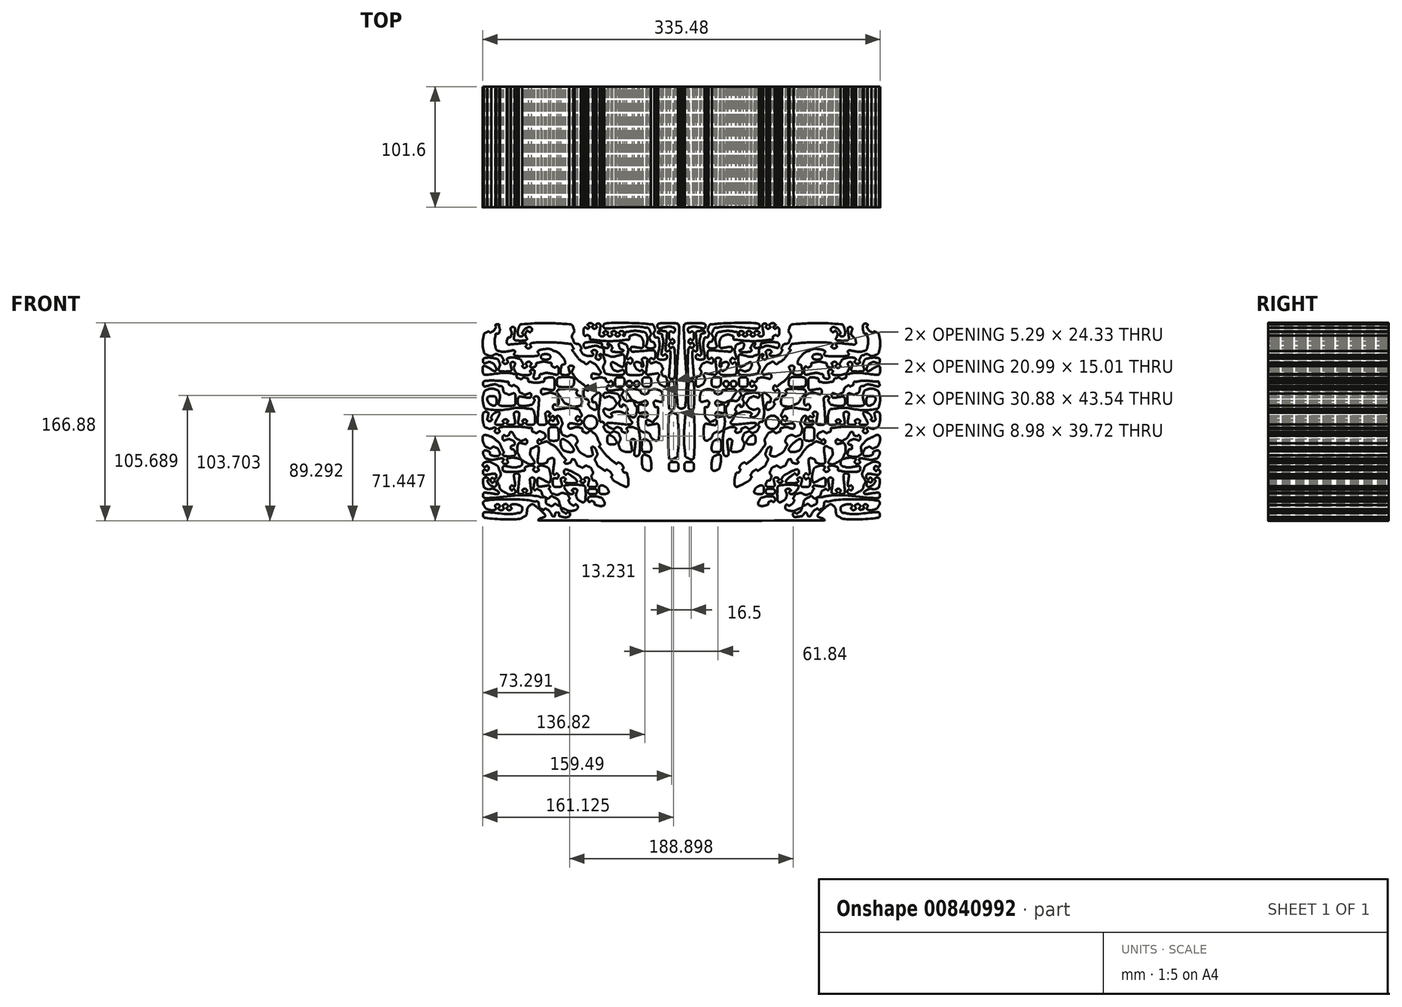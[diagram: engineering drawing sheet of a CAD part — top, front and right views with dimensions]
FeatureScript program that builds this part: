
annotation { "Feature Type Name" : "Feature", "Feature Type Description" : "" }
export const myFeature = defineFeature(function(context is Context, id is Id, definition is map)
    precondition{}
    {
        {
            var Q0;
            Q0=qCreatedBy(makeId("Front.planeOp"),FACE);
            var sketch = newSketch(context, id + "F0", { "sketchPlane" : qUnion([Q0])});
            skCircle(sketch, "E0", {"center": v(-76.75, -0.34) * mm, "radius": 5.68 * mm});
            skCircle(sketch, "E1", {"center": v(76.75, -0.34) * mm, "radius": 5.68 * mm});
            skLineSegment(sketch, "E2", {"start": v(-153.75, 82.4) * mm, "end": v(-156.25, 82.4) * mm});
            skFitSpline(sketch, "E3", {"points": [v(-156.25, 82.4) * mm, v(-156.45, 82.3) * mm, v(-156.71, 82.14) * mm, v(-156.75, 81.9) * mm]});
            skFitSpline(sketch, "E4", {"points": [v(-156.75, 81.9) * mm, v(-156.89, 81.09) * mm, v(-156.33, 80.13) * mm, v(-156.75, 79.4) * mm]});
            skFitSpline(sketch, "E5", {"points": [v(-156.75, 79.4) * mm, v(-157.58, 77.98) * mm, v(-158.77, 76.65) * mm, v(-160.25, 75.9) * mm]});
            skFitSpline(sketch, "E6", {"points": [v(-160.25, 75.9) * mm, v(-161.3, 75.39) * mm, v(-162.7, 76.4) * mm, v(-163.75, 75.9) * mm]});
            skFitSpline(sketch, "E7", {"points": [v(-163.75, 75.9) * mm, v(-165.03, 75.32) * mm, v(-166.49, 74.3) * mm, v(-166.75, 72.9) * mm]});
            skFitSpline(sketch, "E8", {"points": [v(-166.75, 72.9) * mm, v(-167.55, 68.65) * mm, v(-167.65, 64.15) * mm, v(-166.75, 59.9) * mm]});
            skFitSpline(sketch, "E9", {"points": [v(-166.75, 59.9) * mm, v(-166.4, 58.3) * mm, v(-164.84, 56.84) * mm, v(-163.25, 56.4) * mm]});
            skFitSpline(sketch, "E10", {"points": [v(-163.25, 56.4) * mm, v(-160.2, 55.59) * mm, v(-156.8, 57.23) * mm, v(-153.75, 56.4) * mm]});
            skFitSpline(sketch, "E11", {"points": [v(-153.75, 56.4) * mm, v(-152.16, 55.98) * mm, v(-151.03, 54.36) * mm, v(-150.25, 52.9) * mm]});
            skFitSpline(sketch, "E12", {"points": [v(-150.25, 52.9) * mm, v(-149.78, 52.03) * mm, v(-151, 50.56) * mm, v(-150.25, 49.9) * mm]});
            skFitSpline(sketch, "E13", {"points": [v(-150.25, 49.9) * mm, v(-149.36, 49.15) * mm, v(-147.26, 49.4) * mm, v(-146.75, 49.9) * mm]});
            skFitSpline(sketch, "E14", {"points": [v(-146.75, 49.9) * mm, v(-146.24, 50.42) * mm, v(-147.26, 52.9) * mm, v(-146.75, 53.4) * mm]});
            skFitSpline(sketch, "E15", {"points": [v(-146.75, 53.4) * mm, v(-146.24, 53.92) * mm, v(-140.62, 54.3) * mm, v(-137.75, 53.4) * mm]});
            skFitSpline(sketch, "E16", {"points": [v(-137.75, 53.4) * mm, v(-135.95, 52.85) * mm, v(-134.69, 51.05) * mm, v(-133.75, 49.4) * mm]});
            skFitSpline(sketch, "E17", {"points": [v(-133.75, 49.4) * mm, v(-133.25, 48.54) * mm, v(-134.46, 47.12) * mm, v(-133.75, 46.4) * mm]});
            skFitSpline(sketch, "E18", {"points": [v(-133.75, 46.4) * mm, v(-133.04, 45.7) * mm, v(-131.26, 45.9) * mm, v(-130.75, 46.4) * mm]});
            skFitSpline(sketch, "E19", {"points": [v(-130.75, 46.4) * mm, v(-130.24, 46.92) * mm, v(-131.26, 49.4) * mm, v(-130.75, 49.9) * mm]});
            skFitSpline(sketch, "E20", {"points": [v(-130.75, 49.9) * mm, v(-130.24, 50.42) * mm, v(-128.07, 50.73) * mm, v(-127.25, 49.9) * mm]});
            skFitSpline(sketch, "E21", {"points": [v(-127.25, 49.9) * mm, v(-126.42, 49.08) * mm, v(-127.76, 46.92) * mm, v(-127.25, 46.4) * mm]});
            skFitSpline(sketch, "E22", {"points": [v(-127.25, 46.4) * mm, v(-126.74, 45.9) * mm, v(-125.13, 45.93) * mm, v(-124.25, 46.4) * mm]});
            skFitSpline(sketch, "E23", {"points": [v(-124.25, 46.4) * mm, v(-122.8, 47.2) * mm, v(-122.34, 49.48) * mm, v(-120.75, 49.9) * mm]});
            skFitSpline(sketch, "E24", {"points": [v(-120.75, 49.9) * mm, v(-117.7, 50.73) * mm, v(-114.3, 50.73) * mm, v(-111.25, 49.9) * mm]});
            skFitSpline(sketch, "E25", {"points": [v(-111.25, 49.9) * mm, v(-109.66, 49.48) * mm, v(-109.23, 47.15) * mm, v(-107.75, 46.4) * mm]});
            skFitSpline(sketch, "E26", {"points": [v(-107.75, 46.4) * mm, v(-106.7, 45.89) * mm, v(-104.76, 46.92) * mm, v(-104.25, 46.4) * mm]});
            skFitSpline(sketch, "E27", {"points": [v(-104.25, 46.4) * mm, v(-103.74, 45.9) * mm, v(-103.74, 40.92) * mm, v(-104.25, 40.4) * mm]});
            skFitSpline(sketch, "E28", {"points": [v(-104.25, 40.4) * mm, v(-104.76, 39.9) * mm, v(-113.34, 41.32) * mm, v(-117.75, 40.4) * mm]});
            skFitSpline(sketch, "E29", {"points": [v(-117.75, 40.4) * mm, v(-119.37, 40.08) * mm, v(-119.8, 37.7) * mm, v(-121.25, 36.9) * mm]});
            skFitSpline(sketch, "E30", {"points": [v(-121.25, 36.9) * mm, v(-122.13, 36.43) * mm, v(-123.74, 36.4) * mm, v(-124.25, 36.9) * mm]});
            skFitSpline(sketch, "E31", {"points": [v(-124.25, 36.9) * mm, v(-124.76, 37.42) * mm, v(-123.74, 42.9) * mm, v(-124.25, 43.4) * mm]});
            skFitSpline(sketch, "E32", {"points": [v(-124.25, 43.4) * mm, v(-124.76, 43.92) * mm, v(-126.74, 43.92) * mm, v(-127.25, 43.4) * mm]});
            skFitSpline(sketch, "E33", {"points": [v(-127.25, 43.4) * mm, v(-127.76, 42.9) * mm, v(-126.74, 40.92) * mm, v(-127.25, 40.4) * mm]});
            skFitSpline(sketch, "E34", {"points": [v(-127.25, 40.4) * mm, v(-127.76, 39.9) * mm, v(-134.02, 39.57) * mm, v(-137.25, 40.4) * mm]});
            skFitSpline(sketch, "E35", {"points": [v(-137.25, 40.4) * mm, v(-138.85, 40.82) * mm, v(-140.18, 42.36) * mm, v(-140.75, 43.9) * mm]});
            skFitSpline(sketch, "E36", {"points": [v(-140.75, 43.9) * mm, v(-141.44, 45.79) * mm, v(-140.24, 49.4) * mm, v(-140.75, 49.9) * mm]});
            skFitSpline(sketch, "E37", {"points": [v(-140.75, 49.9) * mm, v(-141.26, 50.42) * mm, v(-143.24, 50.42) * mm, v(-143.75, 49.9) * mm]});
            skFitSpline(sketch, "E38", {"points": [v(-143.75, 49.9) * mm, v(-144.26, 49.4) * mm, v(-143.24, 43.92) * mm, v(-143.75, 43.4) * mm]});
            skFitSpline(sketch, "E39", {"points": [v(-143.75, 43.4) * mm, v(-144.26, 42.9) * mm, v(-153.24, 42.9) * mm, v(-153.75, 43.4) * mm]});
            skFitSpline(sketch, "E40", {"points": [v(-153.75, 43.4) * mm, v(-154.26, 43.92) * mm, v(-153.08, 48.17) * mm, v(-153.75, 50.4) * mm]});
            skFitSpline(sketch, "E41", {"points": [v(-153.75, 50.4) * mm, v(-154.16, 51.76) * mm, v(-155.37, 53.1) * mm, v(-156.75, 53.4) * mm]});
            skFitSpline(sketch, "E42", {"points": [v(-156.75, 53.4) * mm, v(-160, 54.16) * mm, v(-166.24, 53.92) * mm, v(-166.75, 53.4) * mm]});
            skFitSpline(sketch, "E43", {"points": [v(-166.75, 53.4) * mm, v(-167.26, 52.9) * mm, v(-167.26, 50.42) * mm, v(-166.75, 49.9) * mm]});
            skFitSpline(sketch, "E44", {"points": [v(-166.75, 49.9) * mm, v(-166.24, 49.4) * mm, v(-162.3, 50.62) * mm, v(-160.25, 49.9) * mm]});
            skFitSpline(sketch, "E45", {"points": [v(-160.25, 49.9) * mm, v(-158.7, 49.36) * mm, v(-157.51, 47.87) * mm, v(-156.75, 46.4) * mm]});
            skFitSpline(sketch, "E46", {"points": [v(-156.75, 46.4) * mm, v(-156.26, 45.47) * mm, v(-156.15, 43.62) * mm, v(-156.75, 43.21) * mm]});
            skFitSpline(sketch, "E47", {"points": [v(-156.75, 43.21) * mm, v(-157.35, 42.8) * mm, v(-166.15, 47.51) * mm, v(-166.75, 47.1) * mm]});
            skFitSpline(sketch, "E48", {"points": [v(-166.75, 47.1) * mm, v(-167.35, 46.7) * mm, v(-167.26, 40.92) * mm, v(-166.75, 40.4) * mm]});
            skFitSpline(sketch, "E49", {"points": [v(-166.75, 40.4) * mm, v(-166.24, 39.9) * mm, v(-149.36, 41.43) * mm, v(-140.75, 40.4) * mm]});
            skFitSpline(sketch, "E50", {"points": [v(-140.75, 40.4) * mm, v(-139.11, 40.21) * mm, v(-138.8, 37.45) * mm, v(-137.25, 36.9) * mm]});
            skFitSpline(sketch, "E51", {"points": [v(-137.25, 36.9) * mm, v(-135.2, 36.2) * mm, v(-132.82, 37.56) * mm, v(-130.75, 36.9) * mm]});
            skFitSpline(sketch, "E52", {"points": [v(-130.75, 36.9) * mm, v(-129.4, 36.48) * mm, v(-129.13, 34.22) * mm, v(-127.75, 33.9) * mm]});
            skFitSpline(sketch, "E53", {"points": [v(-127.75, 33.9) * mm, v(-124.33, 33.15) * mm, v(-120.67, 33.15) * mm, v(-117.25, 33.9) * mm]});
            skFitSpline(sketch, "E54", {"points": [v(-117.25, 33.9) * mm, v(-115.87, 34.22) * mm, v(-115.6, 36.48) * mm, v(-114.25, 36.9) * mm]});
            skFitSpline(sketch, "E55", {"points": [v(-114.25, 36.9) * mm, v(-112.18, 37.56) * mm, v(-108.26, 37.42) * mm, v(-107.75, 36.9) * mm]});
            skFitSpline(sketch, "E56", {"points": [v(-107.75, 36.9) * mm, v(-107.24, 36.4) * mm, v(-107.24, 27.92) * mm, v(-107.75, 27.4) * mm]});
            skFitSpline(sketch, "E57", {"points": [v(-107.75, 27.4) * mm, v(-108.26, 26.9) * mm, v(-117.24, 27.92) * mm, v(-117.75, 27.4) * mm]});
            skFitSpline(sketch, "E58", {"points": [v(-117.75, 27.4) * mm, v(-118.26, 26.9) * mm, v(-118.26, 24.42) * mm, v(-117.75, 23.9) * mm]});
            skFitSpline(sketch, "E59", {"points": [v(-117.75, 23.9) * mm, v(-117.24, 23.4) * mm, v(-110.98, 24.75) * mm, v(-107.75, 23.9) * mm]});
            skFitSpline(sketch, "E60", {"points": [v(-107.75, 23.9) * mm, v(-106.15, 23.5) * mm, v(-104.82, 21.96) * mm, v(-104.25, 20.4) * mm]});
            skFitSpline(sketch, "E61", {"points": [v(-104.25, 20.4) * mm, v(-103.56, 18.53) * mm, v(-103.74, 14.92) * mm, v(-104.25, 14.4) * mm]});
            skFitSpline(sketch, "E62", {"points": [v(-104.25, 14.4) * mm, v(-104.76, 13.9) * mm, v(-107.24, 14.92) * mm, v(-107.75, 14.4) * mm]});
            skFitSpline(sketch, "E63", {"points": [v(-107.75, 14.4) * mm, v(-108.26, 13.9) * mm, v(-108.26, 11.42) * mm, v(-107.75, 10.9) * mm]});
            skFitSpline(sketch, "E64", {"points": [v(-107.75, 10.9) * mm, v(-107.24, 10.4) * mm, v(-94.68, 11.89) * mm, v(-88.25, 10.9) * mm]});
            skFitSpline(sketch, "E65", {"points": [v(-88.25, 10.9) * mm, v(-86.62, 10.66) * mm, v(-85.53, 8.86) * mm, v(-84.75, 7.4) * mm]});
            skFitSpline(sketch, "E66", {"points": [v(-84.75, 7.4) * mm, v(-84.28, 6.53) * mm, v(-84.24, 4.92) * mm, v(-84.75, 4.4) * mm]});
            skFitSpline(sketch, "E67", {"points": [v(-84.75, 4.4) * mm, v(-85.26, 3.9) * mm, v(-87.74, 4.92) * mm, v(-88.25, 4.4) * mm]});
            skFitSpline(sketch, "E68", {"points": [v(-88.25, 4.4) * mm, v(-88.76, 3.9) * mm, v(-89, 2.06) * mm, v(-88.25, 1.4) * mm]});
            skFitSpline(sketch, "E69", {"points": [v(-88.25, 1.4) * mm, v(-87.36, 0.65) * mm, v(-85.64, 2.17) * mm, v(-84.75, 1.4) * mm]});
            skFitSpline(sketch, "E70", {"points": [v(-84.75, 1.4) * mm, v(-84, 0.76) * mm, v(-84.24, -1.08) * mm, v(-84.75, -1.6) * mm]});
            skFitSpline(sketch, "E71", {"points": [v(-84.75, -1.6) * mm, v(-85.26, -2.1) * mm, v(-94.24, -1.08) * mm, v(-94.75, -1.6) * mm]});
            skFitSpline(sketch, "E72", {"points": [v(-94.75, -1.6) * mm, v(-95.26, -2.1) * mm, v(-95.26, -4.58) * mm, v(-94.75, -5.1) * mm]});
            skFitSpline(sketch, "E73", {"points": [v(-94.75, -5.1) * mm, v(-94.24, -5.6) * mm, v(-88.3, -4.27) * mm, v(-85.25, -5.1) * mm]});
            skFitSpline(sketch, "E74", {"points": [v(-85.25, -5.1) * mm, v(-83.66, -5.52) * mm, v(-83.3, -8.05) * mm, v(-81.75, -8.6) * mm]});
            skFitSpline(sketch, "E75", {"points": [v(-81.75, -8.6) * mm, v(-79.7, -9.3) * mm, v(-77, -7.31) * mm, v(-75.25, -8.6) * mm]});
            skFitSpline(sketch, "E76", {"points": [v(-75.25, -8.6) * mm, v(-72.15, -10.85) * mm, v(-70.47, -14.66) * mm, v(-68.75, -18.1) * mm]});
            skFitSpline(sketch, "E77", {"points": [v(-68.75, -18.1) * mm, v(-68.23, -19.13) * mm, v(-69.47, -20.67) * mm, v(-68.75, -21.6) * mm]});
            skFitSpline(sketch, "E78", {"points": [v(-68.75, -21.6) * mm, v(-64.96, -26.4) * mm, v(-60.56, -30.8) * mm, v(-55.75, -34.6) * mm]});
            skFitSpline(sketch, "E79", {"points": [v(-55.75, -34.6) * mm, v(-54.83, -35.31) * mm, v(-53.3, -34.1) * mm, v(-52.25, -34.6) * mm]});
            skFitSpline(sketch, "E80", {"points": [v(-52.25, -34.6) * mm, v(-50.97, -35.18) * mm, v(-49.84, -36.3) * mm, v(-49.25, -37.6) * mm]});
            skFitSpline(sketch, "E81", {"points": [v(-49.25, -37.6) * mm, v(-48.76, -38.65) * mm, v(-49.77, -40.05) * mm, v(-49.25, -41.1) * mm]});
            skFitSpline(sketch, "E82", {"points": [v(-49.25, -41.1) * mm, v(-48.51, -42.57) * mm, v(-46.17, -43) * mm, v(-45.75, -44.6) * mm]});
            skFitSpline(sketch, "E83", {"points": [v(-45.75, -44.6) * mm, v(-44.92, -47.71) * mm, v(-45.15, -53.88) * mm, v(-45.75, -54.29) * mm]});
            skFitSpline(sketch, "E84", {"points": [v(-45.75, -54.29) * mm, v(-46.35, -54.7) * mm, v(-52.28, -52.24) * mm, v(-55.25, -50.6) * mm]});
            skFitSpline(sketch, "E85", {"points": [v(-55.25, -50.6) * mm, v(-56.7, -49.8) * mm, v(-57.97, -48.54) * mm, v(-58.75, -47.1) * mm]});
            skFitSpline(sketch, "E86", {"points": [v(-58.75, -47.1) * mm, v(-59.22, -46.21) * mm, v(-58.28, -44.97) * mm, v(-58.75, -44.1) * mm]});
            skFitSpline(sketch, "E87", {"points": [v(-58.75, -44.1) * mm, v(-59.53, -42.64) * mm, v(-60.8, -41.37) * mm, v(-62.25, -40.6) * mm]});
            skFitSpline(sketch, "E88", {"points": [v(-62.25, -40.6) * mm, v(-63.13, -40.12) * mm, v(-64.42, -41.16) * mm, v(-65.25, -40.6) * mm]});
            skFitSpline(sketch, "E89", {"points": [v(-65.25, -40.6) * mm, v(-67.78, -38.86) * mm, v(-70.6, -36.93) * mm, v(-71.75, -34.1) * mm]});
            skFitSpline(sketch, "E90", {"points": [v(-71.75, -34.1) * mm, v(-72.94, -31.16) * mm, v(-70.93, -27.65) * mm, v(-71.75, -24.6) * mm]});
            skFitSpline(sketch, "E91", {"points": [v(-71.75, -24.6) * mm, v(-72.18, -23) * mm, v(-74.58, -20.81) * mm, v(-75.25, -21.1) * mm]});
            skFitSpline(sketch, "E92", {"points": [v(-75.25, -21.1) * mm, v(-75.92, -21.37) * mm, v(-74.74, -27.58) * mm, v(-75.25, -28.1) * mm]});
            skFitSpline(sketch, "E93", {"points": [v(-75.25, -28.1) * mm, v(-75.76, -28.6) * mm, v(-79.49, -29.04) * mm, v(-81.25, -28.1) * mm]});
            skFitSpline(sketch, "E94", {"points": [v(-81.25, -28.1) * mm, v(-84.16, -26.53) * mm, v(-86.73, -24.02) * mm, v(-88.25, -21.1) * mm]});
            skFitSpline(sketch, "E95", {"points": [v(-88.25, -21.1) * mm, v(-89.25, -19.17) * mm, v(-87.6, -16.66) * mm, v(-88.25, -14.6) * mm]});
            skFitSpline(sketch, "E96", {"points": [v(-88.25, -14.6) * mm, v(-88.68, -13.24) * mm, v(-89.9, -12) * mm, v(-91.25, -11.6) * mm]});
            skFitSpline(sketch, "E97", {"points": [v(-91.25, -11.6) * mm, v(-93.48, -10.92) * mm, v(-96.01, -12.26) * mm, v(-98.25, -11.6) * mm]});
            skFitSpline(sketch, "E98", {"points": [v(-98.25, -11.6) * mm, v(-99.6, -11.18) * mm, v(-100.93, -9.97) * mm, v(-101.25, -8.6) * mm]});
            skFitSpline(sketch, "E99", {"points": [v(-101.25, -8.6) * mm, v(-102, -5.34) * mm, v(-100.4, -1.81) * mm, v(-101.25, 1.4) * mm]});
            skFitSpline(sketch, "E100", {"points": [v(-101.25, 1.4) * mm, v(-101.69, 3.05) * mm, v(-104.2, 5.33) * mm, v(-104.86, 5.02) * mm]});
            skFitSpline(sketch, "E101", {"points": [v(-104.86, 5.02) * mm, v(-105.52, 4.7) * mm, v(-103.71, -1.05) * mm, v(-104.2, -1.6) * mm]});
            skFitSpline(sketch, "E102", {"points": [v(-104.2, -1.6) * mm, v(-104.69, -2.13) * mm, v(-110.74, -2.1) * mm, v(-111.25, -1.6) * mm]});
            skFitSpline(sketch, "E103", {"points": [v(-111.25, -1.6) * mm, v(-111.76, -1.08) * mm, v(-111.76, 0.9) * mm, v(-111.25, 1.4) * mm]});
            skFitSpline(sketch, "E104", {"points": [v(-111.25, 1.4) * mm, v(-110.74, 1.92) * mm, v(-108.26, 0.9) * mm, v(-107.75, 1.4) * mm]});
            skFitSpline(sketch, "E105", {"points": [v(-107.75, 1.4) * mm, v(-107.24, 1.92) * mm, v(-107, 3.76) * mm, v(-107.75, 4.4) * mm]});
            skFitSpline(sketch, "E106", {"points": [v(-107.75, 4.4) * mm, v(-108.64, 5.17) * mm, v(-110.42, 3.58) * mm, v(-111.25, 4.4) * mm]});
            skFitSpline(sketch, "E107", {"points": [v(-111.25, 4.4) * mm, v(-112.07, 5.23) * mm, v(-110.5, 7.02) * mm, v(-111.25, 7.9) * mm]});
            skFitSpline(sketch, "E108", {"points": [v(-111.25, 7.9) * mm, v(-111.9, 8.67) * mm, v(-113.74, 8.42) * mm, v(-114.25, 7.9) * mm]});
            skFitSpline(sketch, "E109", {"points": [v(-114.25, 7.9) * mm, v(-114.76, 7.4) * mm, v(-113.74, -1.08) * mm, v(-114.25, -1.6) * mm]});
            skFitSpline(sketch, "E110", {"points": [v(-114.25, -1.6) * mm, v(-114.76, -2.1) * mm, v(-120.24, -2.1) * mm, v(-120.75, -1.6) * mm]});
            skFitSpline(sketch, "E111", {"points": [v(-120.75, -1.6) * mm, v(-121.26, -1.08) * mm, v(-120.24, 20.4) * mm, v(-120.75, 20.9) * mm]});
            skFitSpline(sketch, "E112", {"points": [v(-120.75, 20.9) * mm, v(-121.26, 21.42) * mm, v(-123.74, 21.42) * mm, v(-124.25, 20.9) * mm]});
            skFitSpline(sketch, "E113", {"points": [v(-124.25, 20.9) * mm, v(-124.76, 20.4) * mm, v(-123.76, 18.47) * mm, v(-124.25, 17.4) * mm]});
            skFitSpline(sketch, "E114", {"points": [v(-124.25, 17.4) * mm, v(-124.84, 16.13) * mm, v(-125.87, 14.73) * mm, v(-127.25, 14.4) * mm]});
            skFitSpline(sketch, "E115", {"points": [v(-127.25, 14.4) * mm, v(-130.5, 13.66) * mm, v(-136.74, 13.9) * mm, v(-137.25, 14.4) * mm]});
            skFitSpline(sketch, "E116", {"points": [v(-137.25, 14.4) * mm, v(-137.76, 14.92) * mm, v(-137.76, 20.4) * mm, v(-137.25, 20.9) * mm]});
            skFitSpline(sketch, "E117", {"points": [v(-137.25, 20.9) * mm, v(-136.74, 21.42) * mm, v(-127.76, 20.4) * mm, v(-127.25, 20.9) * mm]});
            skFitSpline(sketch, "E118", {"points": [v(-127.25, 20.9) * mm, v(-126.74, 21.42) * mm, v(-126.74, 23.4) * mm, v(-127.25, 23.9) * mm]});
            skFitSpline(sketch, "E119", {"points": [v(-127.25, 23.9) * mm, v(-127.76, 24.42) * mm, v(-131.81, 22.94) * mm, v(-133.75, 23.9) * mm]});
            skFitSpline(sketch, "E120", {"points": [v(-133.75, 23.9) * mm, v(-136.5, 25.28) * mm, v(-137.7, 28.7) * mm, v(-140.25, 30.4) * mm]});
            skFitSpline(sketch, "E121", {"points": [v(-140.25, 30.4) * mm, v(-141.37, 31.15) * mm, v(-143.05, 30.3) * mm, v(-144.25, 30.9) * mm]});
            skFitSpline(sketch, "E122", {"points": [v(-144.25, 30.9) * mm, v(-145.51, 31.54) * mm, v(-145.85, 33.72) * mm, v(-147.25, 33.9) * mm]});
            skFitSpline(sketch, "E123", {"points": [v(-147.25, 33.9) * mm, v(-153.7, 34.77) * mm, v(-166.24, 34.42) * mm, v(-166.75, 33.9) * mm]});
            skFitSpline(sketch, "E124", {"points": [v(-166.75, 33.9) * mm, v(-167.26, 33.4) * mm, v(-167.26, 30.92) * mm, v(-166.75, 30.4) * mm]});
            skFitSpline(sketch, "E125", {"points": [v(-166.75, 30.4) * mm, v(-166.24, 29.9) * mm, v(-157.86, 31.78) * mm, v(-153.75, 30.4) * mm]});
            skFitSpline(sketch, "E126", {"points": [v(-153.75, 30.4) * mm, v(-150.84, 29.44) * mm, v(-150, 25.28) * mm, v(-147.25, 23.9) * mm]});
            skFitSpline(sketch, "E127", {"points": [v(-147.25, 23.9) * mm, v(-145.31, 22.94) * mm, v(-141.26, 24.42) * mm, v(-140.75, 23.9) * mm]});
            skFitSpline(sketch, "E128", {"points": [v(-140.75, 23.9) * mm, v(-140.24, 23.4) * mm, v(-140.24, 14.92) * mm, v(-140.75, 14.4) * mm]});
            skFitSpline(sketch, "E129", {"points": [v(-140.75, 14.4) * mm, v(-141.26, 13.9) * mm, v(-153.24, 13.9) * mm, v(-153.75, 14.4) * mm]});
            skFitSpline(sketch, "E130", {"points": [v(-153.75, 14.4) * mm, v(-154.26, 14.92) * mm, v(-153, 21.16) * mm, v(-153.75, 24.4) * mm]});
            skFitSpline(sketch, "E131", {"points": [v(-153.75, 24.4) * mm, v(-154.07, 25.79) * mm, v(-155.4, 26.98) * mm, v(-156.75, 27.4) * mm]});
            skFitSpline(sketch, "E132", {"points": [v(-156.75, 27.4) * mm, v(-158.82, 28.06) * mm, v(-161.2, 28.12) * mm, v(-163.25, 27.4) * mm]});
            skFitSpline(sketch, "E133", {"points": [v(-163.25, 27.4) * mm, v(-164.8, 26.86) * mm, v(-166.34, 25.5) * mm, v(-166.75, 23.9) * mm]});
            skFitSpline(sketch, "E134", {"points": [v(-166.75, 23.9) * mm, v(-167.59, 20.68) * mm, v(-167.5, 17.16) * mm, v(-166.75, 13.9) * mm]});
            skFitSpline(sketch, "E135", {"points": [v(-166.75, 13.9) * mm, v(-166.43, 12.53) * mm, v(-165.16, 11.02) * mm, v(-163.75, 10.9) * mm]});
            skFitSpline(sketch, "E136", {"points": [v(-163.75, 10.9) * mm, v(-151.62, 9.99) * mm, v(-139.38, 11.83) * mm, v(-127.25, 10.9) * mm]});
            skFitSpline(sketch, "E137", {"points": [v(-127.25, 10.9) * mm, v(-125.84, 10.8) * mm, v(-124.58, 9.28) * mm, v(-124.25, 7.9) * mm]});
            skFitSpline(sketch, "E138", {"points": [v(-124.25, 7.9) * mm, v(-123.51, 4.83) * mm, v(-123.74, -1.08) * mm, v(-124.25, -1.6) * mm]});
            skFitSpline(sketch, "E139", {"points": [v(-124.25, -1.6) * mm, v(-124.76, -2.1) * mm, v(-130.24, -2.1) * mm, v(-130.75, -1.6) * mm]});
            skFitSpline(sketch, "E140", {"points": [v(-130.75, -1.6) * mm, v(-131.26, -1.08) * mm, v(-130.04, 0.7) * mm, v(-130.75, 1.4) * mm]});
            skFitSpline(sketch, "E141", {"points": [v(-130.75, 1.4) * mm, v(-131.46, 2.12) * mm, v(-133.24, 1.92) * mm, v(-133.75, 1.4) * mm]});
            skFitSpline(sketch, "E142", {"points": [v(-133.75, 1.4) * mm, v(-134.26, 0.9) * mm, v(-133, -0.94) * mm, v(-133.75, -1.6) * mm]});
            skFitSpline(sketch, "E143", {"points": [v(-133.75, -1.6) * mm, v(-134.64, -2.35) * mm, v(-136.74, -2.1) * mm, v(-137.25, -1.6) * mm]});
            skFitSpline(sketch, "E144", {"points": [v(-137.25, -1.6) * mm, v(-137.76, -1.08) * mm, v(-136.74, 7.4) * mm, v(-137.25, 7.9) * mm]});
            skFitSpline(sketch, "E145", {"points": [v(-137.25, 7.9) * mm, v(-137.76, 8.42) * mm, v(-140.24, 8.42) * mm, v(-140.75, 7.9) * mm]});
            skFitSpline(sketch, "E146", {"points": [v(-140.75, 7.9) * mm, v(-141.26, 7.4) * mm, v(-140.24, -1.08) * mm, v(-140.75, -1.6) * mm]});
            skFitSpline(sketch, "E147", {"points": [v(-140.75, -1.6) * mm, v(-141.26, -2.1) * mm, v(-144.96, -2.49) * mm, v(-146.75, -1.6) * mm]});
            skFitSpline(sketch, "E148", {"points": [v(-146.75, -1.6) * mm, v(-147.64, -1.14) * mm, v(-146, 0.76) * mm, v(-146.75, 1.4) * mm]});
            skFitSpline(sketch, "E149", {"points": [v(-146.75, 1.4) * mm, v(-147.64, 2.17) * mm, v(-149.74, 1.92) * mm, v(-150.25, 1.4) * mm]});
            skFitSpline(sketch, "E150", {"points": [v(-150.25, 1.4) * mm, v(-150.76, 0.9) * mm, v(-149.74, -1.08) * mm, v(-150.25, -1.6) * mm]});
            skFitSpline(sketch, "E151", {"points": [v(-150.25, -1.6) * mm, v(-150.76, -2.1) * mm, v(-156.5, -2.18) * mm, v(-156.93, -1.6) * mm]});
            skFitSpline(sketch, "E152", {"points": [v(-156.93, -1.6) * mm, v(-157.35, -1) * mm, v(-153.15, 7.32) * mm, v(-153.57, 7.9) * mm]});
            skFitSpline(sketch, "E153", {"points": [v(-153.57, 7.9) * mm, v(-154, 8.5) * mm, v(-155.81, 8.4) * mm, v(-156.75, 7.9) * mm]});
            skFitSpline(sketch, "E154", {"points": [v(-156.75, 7.9) * mm, v(-158.21, 7.14) * mm, v(-159.47, 5.86) * mm, v(-160.25, 4.4) * mm]});
            skFitSpline(sketch, "E155", {"points": [v(-160.25, 4.4) * mm, v(-160.72, 3.53) * mm, v(-159.54, 2.12) * mm, v(-160.25, 1.4) * mm]});
            skFitSpline(sketch, "E156", {"points": [v(-160.25, 1.4) * mm, v(-160.96, 0.7) * mm, v(-162.74, 0.9) * mm, v(-163.25, 1.4) * mm]});
            skFitSpline(sketch, "E157", {"points": [v(-163.25, 1.4) * mm, v(-163.76, 1.92) * mm, v(-162.74, 7.4) * mm, v(-163.25, 7.9) * mm]});
            skFitSpline(sketch, "E158", {"points": [v(-163.25, 7.9) * mm, v(-163.76, 8.42) * mm, v(-166.24, 8.42) * mm, v(-166.75, 7.9) * mm]});
            skFitSpline(sketch, "E159", {"points": [v(-166.75, 7.9) * mm, v(-167.26, 7.4) * mm, v(-167.5, 1.16) * mm, v(-166.75, -2.1) * mm]});
            skFitSpline(sketch, "E160", {"points": [v(-166.75, -2.1) * mm, v(-166.43, -3.47) * mm, v(-165.1, -4.68) * mm, v(-163.75, -5.1) * mm]});
            skFitSpline(sketch, "E161", {"points": [v(-163.75, -5.1) * mm, v(-161.51, -5.76) * mm, v(-157.26, -4.58) * mm, v(-156.75, -5.1) * mm]});
            skFitSpline(sketch, "E162", {"points": [v(-156.75, -5.1) * mm, v(-156.24, -5.6) * mm, v(-157.5, -7.7) * mm, v(-156.75, -8.6) * mm]});
            skFitSpline(sketch, "E163", {"points": [v(-156.75, -8.6) * mm, v(-156.1, -9.35) * mm, v(-154.26, -9.1) * mm, v(-153.75, -8.6) * mm]});
            skFitSpline(sketch, "E164", {"points": [v(-153.75, -8.6) * mm, v(-153.24, -8.08) * mm, v(-154.26, -5.6) * mm, v(-153.75, -5.1) * mm]});
            skFitSpline(sketch, "E165", {"points": [v(-153.75, -5.1) * mm, v(-153.24, -4.58) * mm, v(-136.36, -4.07) * mm, v(-127.75, -5.1) * mm]});
            skFitSpline(sketch, "E166", {"points": [v(-127.75, -5.1) * mm, v(-126.11, -5.29) * mm, v(-125.8, -8.05) * mm, v(-124.25, -8.6) * mm]});
            skFitSpline(sketch, "E167", {"points": [v(-124.25, -8.6) * mm, v(-122.2, -9.3) * mm, v(-119.82, -7.94) * mm, v(-117.75, -8.6) * mm]});
            skFitSpline(sketch, "E168", {"points": [v(-117.75, -8.6) * mm, v(-116.4, -9.02) * mm, v(-114.8, -10.51) * mm, v(-114.75, -11.6) * mm]});
            skFitSpline(sketch, "E169", {"points": [v(-114.75, -11.6) * mm, v(-114.7, -12.67) * mm, v(-116.42, -14.32) * mm, v(-117.75, -15.1) * mm]});
            skFitSpline(sketch, "E170", {"points": [v(-117.75, -15.1) * mm, v(-118.61, -15.6) * mm, v(-120.24, -14.58) * mm, v(-120.75, -15.1) * mm]});
            skFitSpline(sketch, "E171", {"points": [v(-120.75, -15.1) * mm, v(-121.26, -15.6) * mm, v(-121.26, -17.58) * mm, v(-120.75, -18.1) * mm]});
            skFitSpline(sketch, "E172", {"points": [v(-120.75, -18.1) * mm, v(-120.24, -18.6) * mm, v(-114, -16.5) * mm, v(-111.25, -18.1) * mm]});
            skFitSpline(sketch, "E173", {"points": [v(-111.25, -18.1) * mm, v(-105.94, -21.16) * mm, v(-102.04, -26.28) * mm, v(-98.25, -31.1) * mm]});
            skFitSpline(sketch, "E174", {"points": [v(-98.25, -31.1) * mm, v(-97.53, -32) * mm, v(-98.76, -34.08) * mm, v(-98.25, -34.6) * mm]});
            skFitSpline(sketch, "E175", {"points": [v(-98.25, -34.6) * mm, v(-97.74, -35.1) * mm, v(-95.82, -35.05) * mm, v(-94.75, -34.6) * mm]});
            skFitSpline(sketch, "E176", {"points": [v(-94.75, -34.6) * mm, v(-93.34, -33.99) * mm, v(-92.33, -31.55) * mm, v(-91.25, -31.6) * mm]});
            skFitSpline(sketch, "E177", {"points": [v(-91.25, -31.6) * mm, v(-90.17, -31.63) * mm, v(-87.8, -36.37) * mm, v(-85.25, -37.6) * mm]});
            skFitSpline(sketch, "E178", {"points": [v(-85.25, -37.6) * mm, v(-83.3, -38.53) * mm, v(-80.8, -36.88) * mm, v(-78.75, -37.6) * mm]});
            skFitSpline(sketch, "E179", {"points": [v(-78.75, -37.6) * mm, v(-77.2, -38.14) * mm, v(-75.8, -39.53) * mm, v(-75.25, -41.1) * mm]});
            skFitSpline(sketch, "E180", {"points": [v(-75.25, -41.1) * mm, v(-74.53, -43.14) * mm, v(-75.97, -45.55) * mm, v(-75.25, -47.6) * mm]});
            skFitSpline(sketch, "E181", {"points": [v(-75.25, -47.6) * mm, v(-74.7, -49.15) * mm, v(-72.53, -49.64) * mm, v(-71.75, -51.1) * mm]});
            skFitSpline(sketch, "E182", {"points": [v(-71.75, -51.1) * mm, v(-71.28, -51.97) * mm, v(-71.24, -53.58) * mm, v(-71.75, -54.1) * mm]});
            skFitSpline(sketch, "E183", {"points": [v(-71.75, -54.1) * mm, v(-72.26, -54.6) * mm, v(-77.74, -54.6) * mm, v(-78.25, -54.1) * mm]});
            skFitSpline(sketch, "E184", {"points": [v(-78.25, -54.1) * mm, v(-78.76, -53.58) * mm, v(-77.74, -48.1) * mm, v(-78.25, -47.6) * mm]});
            skFitSpline(sketch, "E185", {"points": [v(-78.25, -47.6) * mm, v(-78.76, -47.08) * mm, v(-81.24, -47.08) * mm, v(-81.75, -47.6) * mm]});
            skFitSpline(sketch, "E186", {"points": [v(-81.75, -47.6) * mm, v(-82.26, -48.1) * mm, v(-81.24, -50.08) * mm, v(-81.75, -50.6) * mm]});
            skFitSpline(sketch, "E187", {"points": [v(-81.75, -50.6) * mm, v(-82.26, -51.1) * mm, v(-84.24, -51.1) * mm, v(-84.75, -50.6) * mm]});
            skFitSpline(sketch, "E188", {"points": [v(-84.75, -50.6) * mm, v(-85.26, -50.08) * mm, v(-84.28, -48.47) * mm, v(-84.75, -47.6) * mm]});
            skFitSpline(sketch, "E189", {"points": [v(-84.75, -47.6) * mm, v(-85.53, -46.14) * mm, v(-86.8, -44.87) * mm, v(-88.25, -44.1) * mm]});
            skFitSpline(sketch, "E190", {"points": [v(-88.25, -44.1) * mm, v(-91.39, -42.42) * mm, v(-97.65, -40) * mm, v(-98.25, -40.4) * mm]});
            skFitSpline(sketch, "E191", {"points": [v(-98.25, -40.4) * mm, v(-98.85, -40.82) * mm, v(-98.76, -43.58) * mm, v(-98.25, -44.1) * mm]});
            skFitSpline(sketch, "E192", {"points": [v(-98.25, -44.1) * mm, v(-97.74, -44.6) * mm, v(-95.73, -43.45) * mm, v(-94.75, -44.1) * mm]});
            skFitSpline(sketch, "E193", {"points": [v(-94.75, -44.1) * mm, v(-92.18, -45.76) * mm, v(-87.97, -49.92) * mm, v(-88.25, -50.6) * mm]});
            skFitSpline(sketch, "E194", {"points": [v(-88.25, -50.6) * mm, v(-88.53, -51.26) * mm, v(-97.74, -51.1) * mm, v(-98.25, -50.6) * mm]});
            skFitSpline(sketch, "E195", {"points": [v(-98.25, -50.6) * mm, v(-98.76, -50.08) * mm, v(-97.54, -48.3) * mm, v(-98.25, -47.6) * mm]});
            skFitSpline(sketch, "E196", {"points": [v(-98.25, -47.6) * mm, v(-98.96, -46.88) * mm, v(-100.74, -47.08) * mm, v(-101.25, -47.6) * mm]});
            skFitSpline(sketch, "E197", {"points": [v(-101.25, -47.6) * mm, v(-101.76, -48.1) * mm, v(-100.74, -53.58) * mm, v(-101.25, -54.1) * mm]});
            skFitSpline(sketch, "E198", {"points": [v(-101.25, -54.1) * mm, v(-101.76, -54.6) * mm, v(-107.24, -54.6) * mm, v(-107.75, -54.1) * mm]});
            skFitSpline(sketch, "E199", {"points": [v(-107.75, -54.1) * mm, v(-108.26, -53.58) * mm, v(-108.26, -48.1) * mm, v(-107.75, -47.6) * mm]});
            skFitSpline(sketch, "E200", {"points": [v(-107.75, -47.6) * mm, v(-107.24, -47.08) * mm, v(-105.42, -47.6) * mm, v(-104.25, -47.6) * mm]});
            skFitSpline(sketch, "E201", {"points": [v(-107.75, -47.6) * mm, v(-106.58, -47.6) * mm, v(-105.41, -47.6) * mm, v(-104.25, -47.6) * mm]});
            skFitSpline(sketch, "E202", {"points": [v(-104.25, -47.6) * mm, v(-103.9, -46.48) * mm, v(-103.42, -44.92) * mm, v(-104.25, -44.1) * mm]});
            skFitSpline(sketch, "E203", {"points": [v(-104.25, -44.1) * mm, v(-105.07, -43.27) * mm, v(-107.24, -44.6) * mm, v(-107.75, -44.1) * mm]});
            skFitSpline(sketch, "E204", {"points": [v(-107.75, -44.1) * mm, v(-108.26, -43.58) * mm, v(-107.24, -31.6) * mm, v(-107.75, -31.1) * mm]});
            skFitSpline(sketch, "E205", {"points": [v(-107.75, -31.1) * mm, v(-108.26, -30.58) * mm, v(-110.2, -30.57) * mm, v(-111.25, -31.1) * mm]});
            skFitSpline(sketch, "E206", {"points": [v(-111.25, -31.1) * mm, v(-112.73, -31.83) * mm, v(-113.2, -34.02) * mm, v(-114.75, -34.6) * mm]});
            skFitSpline(sketch, "E207", {"points": [v(-114.75, -34.6) * mm, v(-116.63, -35.28) * mm, v(-120.24, -35.1) * mm, v(-120.75, -34.6) * mm]});
            skFitSpline(sketch, "E208", {"points": [v(-120.75, -34.6) * mm, v(-121.26, -34.08) * mm, v(-120.24, -21.6) * mm, v(-120.75, -21.1) * mm]});
            skFitSpline(sketch, "E209", {"points": [v(-120.75, -21.1) * mm, v(-121.26, -20.58) * mm, v(-122.87, -20.62) * mm, v(-123.75, -21.1) * mm]});
            skFitSpline(sketch, "E210", {"points": [v(-123.75, -21.1) * mm, v(-125.2, -21.87) * mm, v(-127.2, -22.94) * mm, v(-127.25, -24.6) * mm]});
            skFitSpline(sketch, "E211", {"points": [v(-127.25, -24.6) * mm, v(-127.34, -28.09) * mm, v(-123.66, -34) * mm, v(-124.1, -34.6) * mm]});
            skFitSpline(sketch, "E212", {"points": [v(-124.1, -34.6) * mm, v(-124.52, -35.18) * mm, v(-128.44, -35.55) * mm, v(-130.25, -34.6) * mm]});
            skFitSpline(sketch, "E213", {"points": [v(-130.25, -34.6) * mm, v(-133.16, -33.04) * mm, v(-135.96, -30.63) * mm, v(-137.25, -27.6) * mm]});
            skFitSpline(sketch, "E214", {"points": [v(-137.25, -27.6) * mm, v(-138.49, -24.68) * mm, v(-137.76, -18.6) * mm, v(-137.25, -18.1) * mm]});
            skFitSpline(sketch, "E215", {"points": [v(-137.25, -18.1) * mm, v(-136.74, -17.58) * mm, v(-131.26, -18.6) * mm, v(-130.75, -18.1) * mm]});
            skFitSpline(sketch, "E216", {"points": [v(-130.75, -18.1) * mm, v(-130.24, -17.58) * mm, v(-130.24, -15.6) * mm, v(-130.75, -15.1) * mm]});
            skFitSpline(sketch, "E217", {"points": [v(-130.75, -15.1) * mm, v(-131.26, -14.58) * mm, v(-134.96, -15.99) * mm, v(-136.75, -15.1) * mm]});
            skFitSpline(sketch, "E218", {"points": [v(-136.75, -15.1) * mm, v(-139.6, -13.67) * mm, v(-142.85, -8.57) * mm, v(-143.75, -8.6) * mm]});
            skFitSpline(sketch, "E219", {"points": [v(-143.75, -8.6) * mm, v(-144.65, -8.6) * mm, v(-145.47, -11) * mm, v(-146.75, -11.6) * mm]});
            skFitSpline(sketch, "E220", {"points": [v(-146.75, -11.6) * mm, v(-147.8, -12.08) * mm, v(-149.74, -11.08) * mm, v(-150.25, -11.6) * mm]});
            skFitSpline(sketch, "E221", {"points": [v(-150.25, -11.6) * mm, v(-150.76, -12.1) * mm, v(-150.76, -14.58) * mm, v(-150.25, -15.1) * mm]});
            skFitSpline(sketch, "E222", {"points": [v(-150.25, -15.1) * mm, v(-149.74, -15.6) * mm, v(-145.82, -14.44) * mm, v(-143.75, -15.1) * mm]});
            skFitSpline(sketch, "E223", {"points": [v(-143.75, -15.1) * mm, v(-142.4, -15.52) * mm, v(-140.8, -17.01) * mm, v(-140.75, -18.1) * mm]});
            skFitSpline(sketch, "E224", {"points": [v(-140.75, -18.1) * mm, v(-140.7, -19.17) * mm, v(-143.8, -20.51) * mm, v(-143.75, -21.6) * mm]});
            skFitSpline(sketch, "E225", {"points": [v(-143.75, -21.6) * mm, v(-143.7, -22.67) * mm, v(-141.34, -23.3) * mm, v(-140.75, -24.6) * mm]});
            skFitSpline(sketch, "E226", {"points": [v(-140.75, -24.6) * mm, v(-140.26, -25.65) * mm, v(-140.24, -27.58) * mm, v(-140.75, -28.1) * mm]});
            skFitSpline(sketch, "E227", {"points": [v(-140.75, -28.1) * mm, v(-141.26, -28.6) * mm, v(-149.74, -28.6) * mm, v(-150.25, -28.1) * mm]});
            skFitSpline(sketch, "E228", {"points": [v(-150.25, -28.1) * mm, v(-150.76, -27.58) * mm, v(-149.73, -25.63) * mm, v(-150.25, -24.6) * mm]});
            skFitSpline(sketch, "E229", {"points": [v(-150.25, -24.6) * mm, v(-151.97, -21.16) * mm, v(-153.75, -17.49) * mm, v(-156.75, -15.1) * mm]});
            skFitSpline(sketch, "E230", {"points": [v(-156.75, -15.1) * mm, v(-159.52, -12.87) * mm, v(-166.15, -11) * mm, v(-166.75, -11.4) * mm]});
            skFitSpline(sketch, "E231", {"points": [v(-166.75, -11.4) * mm, v(-167.35, -11.82) * mm, v(-167.47, -15.98) * mm, v(-166.75, -18.1) * mm]});
            skFitSpline(sketch, "E232", {"points": [v(-166.75, -18.1) * mm, v(-166.21, -19.65) * mm, v(-164.8, -21.05) * mm, v(-163.25, -21.6) * mm]});
            skFitSpline(sketch, "E233", {"points": [v(-163.25, -21.6) * mm, v(-161.2, -22.3) * mm, v(-158.82, -20.94) * mm, v(-156.75, -21.6) * mm]});
            skFitSpline(sketch, "E234", {"points": [v(-156.75, -21.6) * mm, v(-155.4, -22.02) * mm, v(-154.34, -23.3) * mm, v(-153.75, -24.6) * mm]});
            skFitSpline(sketch, "E235", {"points": [v(-153.75, -24.6) * mm, v(-153.26, -25.65) * mm, v(-153.24, -27.58) * mm, v(-153.75, -28.1) * mm]});
            skFitSpline(sketch, "E236", {"points": [v(-153.75, -28.1) * mm, v(-154.26, -28.6) * mm, v(-157.87, -28.78) * mm, v(-159.75, -28.1) * mm]});
            skFitSpline(sketch, "E237", {"points": [v(-159.75, -28.1) * mm, v(-161.3, -27.52) * mm, v(-161.77, -25.33) * mm, v(-163.25, -24.6) * mm]});
            skFitSpline(sketch, "E238", {"points": [v(-163.25, -24.6) * mm, v(-164.3, -24.07) * mm, v(-166.24, -24.08) * mm, v(-166.75, -24.6) * mm]});
            skFitSpline(sketch, "E239", {"points": [v(-166.75, -24.6) * mm, v(-167.26, -25.1) * mm, v(-167.24, -27.03) * mm, v(-166.75, -28.1) * mm]});
            skFitSpline(sketch, "E240", {"points": [v(-166.75, -28.1) * mm, v(-166.16, -29.37) * mm, v(-165.14, -30.84) * mm, v(-163.75, -31.1) * mm]});
            skFitSpline(sketch, "E241", {"points": [v(-163.75, -31.1) * mm, v(-159.32, -31.9) * mm, v(-150.76, -30.58) * mm, v(-150.25, -31.1) * mm]});
            skFitSpline(sketch, "E242", {"points": [v(-150.25, -31.1) * mm, v(-149.74, -31.6) * mm, v(-151.07, -33.77) * mm, v(-150.25, -34.6) * mm]});
            skFitSpline(sketch, "E243", {"points": [v(-150.25, -34.6) * mm, v(-149.42, -35.42) * mm, v(-147.26, -35.1) * mm, v(-146.75, -34.6) * mm]});
            skFitSpline(sketch, "E244", {"points": [v(-146.75, -34.6) * mm, v(-146.24, -34.08) * mm, v(-147.26, -31.6) * mm, v(-146.75, -31.1) * mm]});
            skFitSpline(sketch, "E245", {"points": [v(-146.75, -31.1) * mm, v(-146.24, -30.58) * mm, v(-140.3, -30.24) * mm, v(-137.25, -31.1) * mm]});
            skFitSpline(sketch, "E246", {"points": [v(-137.25, -31.1) * mm, v(-135.77, -31.5) * mm, v(-134.2, -33.51) * mm, v(-134.25, -34.6) * mm]});
            skFitSpline(sketch, "E247", {"points": [v(-134.25, -34.6) * mm, v(-134.3, -35.67) * mm, v(-135.86, -37.33) * mm, v(-137.25, -37.6) * mm]});
            skFitSpline(sketch, "E248", {"points": [v(-137.25, -37.6) * mm, v(-141.5, -38.39) * mm, v(-149.74, -37.08) * mm, v(-150.25, -37.6) * mm]});
            skFitSpline(sketch, "E249", {"points": [v(-150.25, -37.6) * mm, v(-150.76, -38.1) * mm, v(-150.76, -40.58) * mm, v(-150.25, -41.1) * mm]});
            skFitSpline(sketch, "E250", {"points": [v(-150.25, -41.1) * mm, v(-149.74, -41.6) * mm, v(-139.17, -42.04) * mm, v(-133.75, -41.1) * mm]});
            skFitSpline(sketch, "E251", {"points": [v(-133.75, -41.1) * mm, v(-132.12, -40.8) * mm, v(-131.8, -38.16) * mm, v(-130.25, -37.6) * mm]});
            skFitSpline(sketch, "E252", {"points": [v(-130.25, -37.6) * mm, v(-128.37, -36.9) * mm, v(-124.76, -37.08) * mm, v(-124.25, -37.6) * mm]});
            skFitSpline(sketch, "E253", {"points": [v(-124.25, -37.6) * mm, v(-123.74, -38.1) * mm, v(-125.07, -40.27) * mm, v(-124.25, -41.1) * mm]});
            skFitSpline(sketch, "E254", {"points": [v(-124.25, -41.1) * mm, v(-123.42, -41.92) * mm, v(-121.26, -41.6) * mm, v(-120.75, -41.1) * mm]});
            skFitSpline(sketch, "E255", {"points": [v(-120.75, -41.1) * mm, v(-120.24, -40.58) * mm, v(-121.26, -38.1) * mm, v(-120.75, -37.6) * mm]});
            skFitSpline(sketch, "E256", {"points": [v(-120.75, -37.6) * mm, v(-120.24, -37.08) * mm, v(-116.63, -36.9) * mm, v(-114.75, -37.6) * mm]});
            skFitSpline(sketch, "E257", {"points": [v(-114.75, -37.6) * mm, v(-113.2, -38.16) * mm, v(-111.67, -39.5) * mm, v(-111.25, -41.1) * mm]});
            skFitSpline(sketch, "E258", {"points": [v(-111.25, -41.1) * mm, v(-110.42, -44.2) * mm, v(-110.66, -50.35) * mm, v(-111.25, -50.77) * mm]});
            skFitSpline(sketch, "E259", {"points": [v(-111.25, -50.77) * mm, v(-111.84, -51.19) * mm, v(-120.16, -47) * mm, v(-120.75, -47.41) * mm]});
            skFitSpline(sketch, "E260", {"points": [v(-120.75, -47.41) * mm, v(-121.34, -47.83) * mm, v(-121.26, -53.58) * mm, v(-120.75, -54.1) * mm]});
            skFitSpline(sketch, "E261", {"points": [v(-120.75, -54.1) * mm, v(-120.24, -54.6) * mm, v(-111.76, -53.58) * mm, v(-111.25, -54.1) * mm]});
            skFitSpline(sketch, "E262", {"points": [v(-111.25, -54.1) * mm, v(-110.74, -54.6) * mm, v(-111.72, -56.21) * mm, v(-111.25, -57.1) * mm]});
            skFitSpline(sketch, "E263", {"points": [v(-111.25, -57.1) * mm, v(-110.47, -58.54) * mm, v(-109.35, -60.18) * mm, v(-107.75, -60.6) * mm]});
            skFitSpline(sketch, "E264", {"points": [v(-107.75, -60.6) * mm, v(-104.52, -61.43) * mm, v(-101, -59.84) * mm, v(-97.75, -60.6) * mm]});
            skFitSpline(sketch, "E265", {"points": [v(-97.75, -60.6) * mm, v(-96.37, -60.9) * mm, v(-95.34, -62.3) * mm, v(-94.75, -63.6) * mm]});
            skFitSpline(sketch, "E266", {"points": [v(-94.75, -63.6) * mm, v(-94.26, -64.65) * mm, v(-95.24, -66.03) * mm, v(-94.75, -67.1) * mm]});
            skFitSpline(sketch, "E267", {"points": [v(-94.75, -67.1) * mm, v(-94.16, -68.37) * mm, v(-93.03, -69.5) * mm, v(-91.75, -70.1) * mm]});
            skFitSpline(sketch, "E268", {"points": [v(-91.75, -70.1) * mm, v(-90.7, -70.58) * mm, v(-89.07, -69.27) * mm, v(-88.25, -70.1) * mm]});
            skFitSpline(sketch, "E269", {"points": [v(-88.25, -70.1) * mm, v(-87.42, -70.92) * mm, v(-87.74, -73.08) * mm, v(-88.25, -73.6) * mm]});
            skFitSpline(sketch, "E270", {"points": [v(-88.25, -73.6) * mm, v(-88.76, -74.1) * mm, v(-94.93, -75.04) * mm, v(-97.75, -73.6) * mm]});
            skFitSpline(sketch, "E271", {"points": [v(-97.75, -73.6) * mm, v(-101.94, -71.44) * mm, v(-103.72, -66.03) * mm, v(-107.75, -63.6) * mm]});
            skFitSpline(sketch, "E272", {"points": [v(-107.75, -63.6) * mm, v(-109.6, -62.47) * mm, v(-112.31, -64.56) * mm, v(-114.25, -63.6) * mm]});
            skFitSpline(sketch, "E273", {"points": [v(-114.25, -63.6) * mm, v(-117, -62.22) * mm, v(-118.18, -58.76) * mm, v(-120.75, -57.1) * mm]});
            skFitSpline(sketch, "E274", {"points": [v(-120.75, -57.1) * mm, v(-121.73, -56.45) * mm, v(-123.74, -57.6) * mm, v(-124.25, -57.1) * mm]});
            skFitSpline(sketch, "E275", {"points": [v(-124.25, -57.1) * mm, v(-124.76, -56.58) * mm, v(-123.74, -48.1) * mm, v(-124.25, -47.6) * mm]});
            skFitSpline(sketch, "E276", {"points": [v(-124.25, -47.6) * mm, v(-124.76, -47.08) * mm, v(-126.74, -47.08) * mm, v(-127.25, -47.6) * mm]});
            skFitSpline(sketch, "E277", {"points": [v(-127.25, -47.6) * mm, v(-127.76, -48.1) * mm, v(-126.74, -59.58) * mm, v(-127.25, -60.1) * mm]});
            skFitSpline(sketch, "E278", {"points": [v(-127.25, -60.1) * mm, v(-127.76, -60.6) * mm, v(-130.24, -60.6) * mm, v(-130.75, -60.1) * mm]});
            skFitSpline(sketch, "E279", {"points": [v(-130.75, -60.1) * mm, v(-131.26, -59.58) * mm, v(-130.04, -57.8) * mm, v(-130.75, -57.1) * mm]});
            skFitSpline(sketch, "E280", {"points": [v(-130.75, -57.1) * mm, v(-131.46, -56.38) * mm, v(-133.24, -56.58) * mm, v(-133.75, -57.1) * mm]});
            skFitSpline(sketch, "E281", {"points": [v(-133.75, -57.1) * mm, v(-134.26, -57.6) * mm, v(-133, -59.44) * mm, v(-133.75, -60.1) * mm]});
            skFitSpline(sketch, "E282", {"points": [v(-133.75, -60.1) * mm, v(-134.64, -60.85) * mm, v(-136.74, -60.6) * mm, v(-137.25, -60.1) * mm]});
            skFitSpline(sketch, "E283", {"points": [v(-137.25, -60.1) * mm, v(-137.76, -59.58) * mm, v(-136.74, -44.6) * mm, v(-137.25, -44.1) * mm]});
            skFitSpline(sketch, "E284", {"points": [v(-137.25, -44.1) * mm, v(-137.76, -43.58) * mm, v(-140.24, -43.58) * mm, v(-140.75, -44.1) * mm]});
            skFitSpline(sketch, "E285", {"points": [v(-140.75, -44.1) * mm, v(-141.26, -44.6) * mm, v(-140.24, -53.58) * mm, v(-140.75, -54.1) * mm]});
            skFitSpline(sketch, "E286", {"points": [v(-140.75, -54.1) * mm, v(-141.26, -54.6) * mm, v(-143.04, -53.38) * mm, v(-143.75, -54.1) * mm]});
            skFitSpline(sketch, "E287", {"points": [v(-143.75, -54.1) * mm, v(-144.46, -54.8) * mm, v(-144.46, -56.38) * mm, v(-143.75, -57.1) * mm]});
            skFitSpline(sketch, "E288", {"points": [v(-143.75, -57.1) * mm, v(-143.04, -57.8) * mm, v(-141.46, -56.38) * mm, v(-140.75, -57.1) * mm]});
            skFitSpline(sketch, "E289", {"points": [v(-140.75, -57.1) * mm, v(-140.04, -57.8) * mm, v(-140.24, -59.58) * mm, v(-140.75, -60.1) * mm]});
            skFitSpline(sketch, "E290", {"points": [v(-140.75, -60.1) * mm, v(-141.26, -60.6) * mm, v(-145.31, -61.06) * mm, v(-147.25, -60.1) * mm]});
            skFitSpline(sketch, "E291", {"points": [v(-147.25, -60.1) * mm, v(-150, -58.72) * mm, v(-152.78, -56.5) * mm, v(-153.75, -53.6) * mm]});
            skFitSpline(sketch, "E292", {"points": [v(-153.75, -53.6) * mm, v(-155.12, -49.48) * mm, v(-152.44, -44.72) * mm, v(-153.75, -40.6) * mm]});
            skFitSpline(sketch, "E293", {"points": [v(-153.75, -40.6) * mm, v(-154.6, -37.9) * mm, v(-157.18, -35.78) * mm, v(-159.75, -34.6) * mm]});
            skFitSpline(sketch, "E294", {"points": [v(-159.75, -34.6) * mm, v(-161.87, -33.61) * mm, v(-166.24, -34.08) * mm, v(-166.75, -34.6) * mm]});
            skFitSpline(sketch, "E295", {"points": [v(-166.75, -34.6) * mm, v(-167.26, -35.1) * mm, v(-167.5, -36.94) * mm, v(-166.75, -37.6) * mm]});
            skFitSpline(sketch, "E296", {"points": [v(-166.75, -37.6) * mm, v(-165.86, -38.35) * mm, v(-164.14, -36.83) * mm, v(-163.25, -37.6) * mm]});
            skFitSpline(sketch, "E297", {"points": [v(-163.25, -37.6) * mm, v(-162.5, -38.24) * mm, v(-162.74, -40.08) * mm, v(-163.25, -40.6) * mm]});
            skFitSpline(sketch, "E298", {"points": [v(-163.25, -40.6) * mm, v(-163.76, -41.1) * mm, v(-166.24, -40.08) * mm, v(-166.75, -40.6) * mm]});
            skFitSpline(sketch, "E299", {"points": [v(-166.75, -40.6) * mm, v(-167.26, -41.1) * mm, v(-167.26, -43.58) * mm, v(-166.75, -44.1) * mm]});
            skFitSpline(sketch, "E300", {"points": [v(-166.75, -44.1) * mm, v(-166.24, -44.6) * mm, v(-157.26, -43.58) * mm, v(-156.75, -44.1) * mm]});
            skFitSpline(sketch, "E301", {"points": [v(-156.75, -44.1) * mm, v(-156.24, -44.6) * mm, v(-156.24, -47.08) * mm, v(-156.75, -47.6) * mm]});
            skFitSpline(sketch, "E302", {"points": [v(-156.75, -47.6) * mm, v(-157.26, -48.1) * mm, v(-159.74, -47.08) * mm, v(-160.25, -47.6) * mm]});
            skFitSpline(sketch, "E303", {"points": [v(-160.25, -47.6) * mm, v(-160.76, -48.1) * mm, v(-161, -49.94) * mm, v(-160.25, -50.6) * mm]});
            skFitSpline(sketch, "E304", {"points": [v(-160.25, -50.6) * mm, v(-159.36, -51.35) * mm, v(-157.57, -49.77) * mm, v(-156.75, -50.6) * mm]});
            skFitSpline(sketch, "E305", {"points": [v(-156.75, -50.6) * mm, v(-155.92, -51.42) * mm, v(-156.24, -53.58) * mm, v(-156.75, -54.1) * mm]});
            skFitSpline(sketch, "E306", {"points": [v(-156.75, -54.1) * mm, v(-157.26, -54.6) * mm, v(-158.87, -54.56) * mm, v(-159.75, -54.1) * mm]});
            skFitSpline(sketch, "E307", {"points": [v(-159.75, -54.1) * mm, v(-161.2, -53.3) * mm, v(-162.47, -52.04) * mm, v(-163.25, -50.6) * mm]});
            skFitSpline(sketch, "E308", {"points": [v(-163.25, -50.6) * mm, v(-163.72, -49.71) * mm, v(-162.5, -48.24) * mm, v(-163.25, -47.6) * mm]});
            skFitSpline(sketch, "E309", {"points": [v(-163.25, -47.6) * mm, v(-164.14, -46.83) * mm, v(-166.24, -47.08) * mm, v(-166.75, -47.6) * mm]});
            skFitSpline(sketch, "E310", {"points": [v(-166.75, -47.6) * mm, v(-167.26, -48.1) * mm, v(-167.25, -51.98) * mm, v(-166.75, -54.1) * mm]});
            skFitSpline(sketch, "E311", {"points": [v(-166.75, -54.1) * mm, v(-166.53, -55) * mm, v(-165.65, -55.8) * mm, v(-164.75, -56.1) * mm]});
            skFitSpline(sketch, "E312", {"points": [v(-164.75, -56.1) * mm, v(-162.34, -56.85) * mm, v(-159.6, -56.2) * mm, v(-157.25, -57.1) * mm]});
            skFitSpline(sketch, "E313", {"points": [v(-157.25, -57.1) * mm, v(-155.93, -57.6) * mm, v(-153.97, -59.42) * mm, v(-154.25, -60.1) * mm]});
            skFitSpline(sketch, "E314", {"points": [v(-154.25, -60.1) * mm, v(-154.53, -60.76) * mm, v(-166.24, -59.58) * mm, v(-166.75, -60.1) * mm]});
            skFitSpline(sketch, "E315", {"points": [v(-166.75, -60.1) * mm, v(-167.26, -60.6) * mm, v(-167.26, -63.08) * mm, v(-166.75, -63.6) * mm]});
            skFitSpline(sketch, "E316", {"points": [v(-166.75, -63.6) * mm, v(-166.24, -64.1) * mm, v(-133.97, -61.7) * mm, v(-117.75, -63.6) * mm]});
            skFitSpline(sketch, "E317", {"points": [v(-117.75, -63.6) * mm, v(-114.7, -63.95) * mm, v(-114, -68.72) * mm, v(-111.25, -70.1) * mm]});
            skFitSpline(sketch, "E318", {"points": [v(-111.25, -70.1) * mm, v(-109.31, -71.06) * mm, v(-106.69, -69.12) * mm, v(-104.75, -70.1) * mm]});
            skFitSpline(sketch, "E319", {"points": [v(-104.75, -70.1) * mm, v(-102, -71.46) * mm, v(-100.82, -74.92) * mm, v(-98.25, -76.6) * mm]});
            skFitSpline(sketch, "E320", {"points": [v(-98.25, -76.6) * mm, v(-97.27, -77.23) * mm, v(-95.64, -75.83) * mm, v(-94.75, -76.6) * mm]});
            skFitSpline(sketch, "E321", {"points": [v(-94.75, -76.6) * mm, v(-94, -77.24) * mm, v(-94.24, -79.08) * mm, v(-94.75, -79.6) * mm]});
            skFitSpline(sketch, "E322", {"points": [v(-94.75, -79.6) * mm, v(-95.26, -80.1) * mm, v(-99.51, -80.26) * mm, v(-101.75, -79.6) * mm]});
            skFitSpline(sketch, "E323", {"points": [v(-101.75, -79.6) * mm, v(-103.1, -79.18) * mm, v(-103.34, -76.6) * mm, v(-104.75, -76.6) * mm]});
            skFitSpline(sketch, "E324", {"points": [v(-104.75, -76.6) * mm, v(-106.16, -76.6) * mm, v(-107.02, -79.6) * mm, v(-107.75, -79.6) * mm]});
            skFitSpline(sketch, "E325", {"points": [v(-107.75, -79.6) * mm, v(-108.48, -79.6) * mm, v(-111.36, -75.1) * mm, v(-113.75, -73.6) * mm]});
            skFitSpline(sketch, "E326", {"points": [v(-113.75, -73.6) * mm, v(-114.74, -72.97) * mm, v(-116.27, -74.23) * mm, v(-117.25, -73.6) * mm]});
            skFitSpline(sketch, "E327", {"points": [v(-117.25, -73.6) * mm, v(-119.82, -71.92) * mm, v(-120.71, -67.49) * mm, v(-123.75, -67.1) * mm]});
            skFitSpline(sketch, "E328", {"points": [v(-123.75, -67.1) * mm, v(-137.96, -65.22) * mm, v(-166.24, -66.58) * mm, v(-166.75, -67.1) * mm]});
            skFitSpline(sketch, "E329", {"points": [v(-166.75, -67.1) * mm, v(-167.26, -67.6) * mm, v(-167.22, -69.21) * mm, v(-166.75, -70.1) * mm]});
            skFitSpline(sketch, "E330", {"points": [v(-166.75, -70.1) * mm, v(-165.97, -71.54) * mm, v(-164.8, -73.05) * mm, v(-163.25, -73.6) * mm]});
            skFitSpline(sketch, "E331", {"points": [v(-163.25, -73.6) * mm, v(-161.2, -74.3) * mm, v(-157.26, -74.1) * mm, v(-156.75, -73.6) * mm]});
            skFitSpline(sketch, "E332", {"points": [v(-156.75, -73.6) * mm, v(-156.24, -73.08) * mm, v(-157.26, -70.6) * mm, v(-156.75, -70.1) * mm]});
            skFitSpline(sketch, "E333", {"points": [v(-156.75, -70.1) * mm, v(-156.24, -69.58) * mm, v(-154.4, -69.33) * mm, v(-153.75, -70.1) * mm]});
            skFitSpline(sketch, "E334", {"points": [v(-153.75, -70.1) * mm, v(-153, -70.98) * mm, v(-154.57, -72.77) * mm, v(-153.75, -73.6) * mm]});
            skFitSpline(sketch, "E335", {"points": [v(-153.75, -73.6) * mm, v(-152.92, -74.42) * mm, v(-150.76, -74.1) * mm, v(-150.25, -73.6) * mm]});
            skFitSpline(sketch, "E336", {"points": [v(-150.25, -73.6) * mm, v(-149.74, -73.08) * mm, v(-150.76, -70.6) * mm, v(-150.25, -70.1) * mm]});
            skFitSpline(sketch, "E337", {"points": [v(-150.25, -70.1) * mm, v(-149.74, -69.58) * mm, v(-147.57, -69.27) * mm, v(-146.75, -70.1) * mm]});
            skFitSpline(sketch, "E338", {"points": [v(-146.75, -70.1) * mm, v(-145.92, -70.92) * mm, v(-147.5, -72.7) * mm, v(-146.75, -73.6) * mm]});
            skFitSpline(sketch, "E339", {"points": [v(-146.75, -73.6) * mm, v(-146.1, -74.35) * mm, v(-144.26, -74.1) * mm, v(-143.75, -73.6) * mm]});
            skFitSpline(sketch, "E340", {"points": [v(-143.75, -73.6) * mm, v(-143.24, -73.08) * mm, v(-144.26, -70.6) * mm, v(-143.75, -70.1) * mm]});
            skFitSpline(sketch, "E341", {"points": [v(-143.75, -70.1) * mm, v(-143.24, -69.58) * mm, v(-139.32, -69.44) * mm, v(-137.25, -70.1) * mm]});
            skFitSpline(sketch, "E342", {"points": [v(-137.25, -70.1) * mm, v(-135.9, -70.52) * mm, v(-134.3, -72.01) * mm, v(-134.25, -73.1) * mm]});
            skFitSpline(sketch, "E343", {"points": [v(-134.25, -73.1) * mm, v(-134.2, -74.17) * mm, v(-135.72, -76.43) * mm, v(-137.25, -76.6) * mm]});
            skFitSpline(sketch, "E344", {"points": [v(-137.25, -76.6) * mm, v(-147.03, -77.64) * mm, v(-166.24, -76.08) * mm, v(-166.75, -76.6) * mm]});
            skFitSpline(sketch, "E345", {"points": [v(-166.75, -76.6) * mm, v(-167.26, -77.1) * mm, v(-167.26, -79.58) * mm, v(-166.75, -80.1) * mm]});
            skFitSpline(sketch, "E346", {"points": [v(-166.75, -80.1) * mm, v(-166.24, -80.6) * mm, v(-136.73, -81.7) * mm, v(-133.75, -80.1) * mm]});
            skFitSpline(sketch, "E347", {"points": [v(-133.75, -80.1) * mm, v(-130.77, -78.47) * mm, v(-129.99, -72.97) * mm, v(-127.25, -70.1) * mm]});
            skFitSpline(sketch, "E348", {"points": [v(-127.25, -70.1) * mm, v(-126.56, -69.37) * mm, v(-125.05, -69.49) * mm, v(-124.25, -70.1) * mm]});
            skFitSpline(sketch, "E349", {"points": [v(-124.25, -70.1) * mm, v(-120.81, -72.68) * mm, v(-115.04, -78.5) * mm, v(-115.12, -79.22) * mm]});
            skFitSpline(sketch, "E350", {"points": [v(-115.12, -79.22) * mm, v(-115.21, -79.94) * mm, v(-119, -81.27) * mm, v(-120.75, -82.6) * mm]});
            skFitSpline(sketch, "E351", {"points": [v(-120.75, -82.6) * mm, v(-120.94, -82.73) * mm, v(-120.49, -83.1) * mm, v(-120.25, -83.1) * mm]});
            skFitSpline(sketch, "E352", {"points": [v(-120.25, -83.1) * mm, v(-40.08, -83.26) * mm, v(40.08, -83.26) * mm, v(120.25, -83.1) * mm]});
            skFitSpline(sketch, "E353", {"points": [v(120.25, -83.1) * mm, v(120.49, -83.1) * mm, v(120.94, -82.73) * mm, v(120.75, -82.6) * mm]});
            skFitSpline(sketch, "E354", {"points": [v(120.75, -82.6) * mm, v(119, -81.27) * mm, v(115.21, -79.94) * mm, v(115.12, -79.22) * mm]});
            skFitSpline(sketch, "E355", {"points": [v(115.12, -79.22) * mm, v(115.04, -78.5) * mm, v(120.81, -72.68) * mm, v(124.25, -70.1) * mm]});
            skFitSpline(sketch, "E356", {"points": [v(124.25, -70.1) * mm, v(125.05, -69.49) * mm, v(126.56, -69.37) * mm, v(127.25, -70.1) * mm]});
            skFitSpline(sketch, "E357", {"points": [v(127.25, -70.1) * mm, v(129.99, -72.97) * mm, v(130.77, -78.47) * mm, v(133.75, -80.1) * mm]});
            skFitSpline(sketch, "E358", {"points": [v(133.75, -80.1) * mm, v(136.73, -81.7) * mm, v(166.24, -80.6) * mm, v(166.75, -80.1) * mm]});
            skFitSpline(sketch, "E359", {"points": [v(166.75, -80.1) * mm, v(167.26, -79.58) * mm, v(167.26, -77.1) * mm, v(166.75, -76.6) * mm]});
            skFitSpline(sketch, "E360", {"points": [v(166.75, -76.6) * mm, v(166.24, -76.08) * mm, v(147.03, -77.64) * mm, v(137.25, -76.6) * mm]});
            skFitSpline(sketch, "E361", {"points": [v(137.25, -76.6) * mm, v(135.72, -76.43) * mm, v(134.2, -74.17) * mm, v(134.25, -73.1) * mm]});
            skFitSpline(sketch, "E362", {"points": [v(134.25, -73.1) * mm, v(134.3, -72.01) * mm, v(135.9, -70.52) * mm, v(137.25, -70.1) * mm]});
            skFitSpline(sketch, "E363", {"points": [v(137.25, -70.1) * mm, v(139.32, -69.44) * mm, v(143.24, -69.58) * mm, v(143.75, -70.1) * mm]});
            skFitSpline(sketch, "E364", {"points": [v(143.75, -70.1) * mm, v(144.26, -70.6) * mm, v(143, -72.7) * mm, v(143.75, -73.6) * mm]});
            skFitSpline(sketch, "E365", {"points": [v(143.75, -73.6) * mm, v(144.4, -74.35) * mm, v(146.24, -74.1) * mm, v(146.75, -73.6) * mm]});
            skFitSpline(sketch, "E366", {"points": [v(146.75, -73.6) * mm, v(147.26, -73.08) * mm, v(146.24, -70.6) * mm, v(146.75, -70.1) * mm]});
            skFitSpline(sketch, "E367", {"points": [v(146.75, -70.1) * mm, v(147.26, -69.58) * mm, v(149.42, -69.27) * mm, v(150.25, -70.1) * mm]});
            skFitSpline(sketch, "E368", {"points": [v(150.25, -70.1) * mm, v(151.07, -70.92) * mm, v(149.74, -73.08) * mm, v(150.25, -73.6) * mm]});
            skFitSpline(sketch, "E369", {"points": [v(150.25, -73.6) * mm, v(150.76, -74.1) * mm, v(152.27, -73.8) * mm, v(153.25, -73.6) * mm]});
            skFitSpline(sketch, "E370", {"points": [v(-61.75, 75.9) * mm, v(-62.87, 76.23) * mm, v(-64.36, 76.67) * mm, v(-65.25, 75.9) * mm]});
            skFitSpline(sketch, "E371", {"points": [v(-65.25, 75.9) * mm, v(-66, 75.26) * mm, v(-64.5, 73.56) * mm, v(-65.25, 72.9) * mm]});
            skFitSpline(sketch, "E372", {"points": [v(-65.25, 72.9) * mm, v(-66.14, 72.15) * mm, v(-68.24, 72.4) * mm, v(-68.75, 72.9) * mm]});
            skFitSpline(sketch, "E373", {"points": [v(-68.75, 72.9) * mm, v(-69.26, 73.42) * mm, v(-68.24, 81.9) * mm, v(-68.75, 82.4) * mm]});
            skFitSpline(sketch, "E374", {"points": [v(-68.75, 82.4) * mm, v(-69.26, 82.92) * mm, v(-71.24, 82.92) * mm, v(-71.75, 82.4) * mm]});
            skFitSpline(sketch, "E375", {"points": [v(-71.75, 82.4) * mm, v(-72.26, 81.9) * mm, v(-71.24, 79.92) * mm, v(-71.75, 79.4) * mm]});
            skFitSpline(sketch, "E376", {"points": [v(-71.75, 79.4) * mm, v(-72.26, 78.9) * mm, v(-74.04, 78.7) * mm, v(-74.75, 79.4) * mm]});
            skFitSpline(sketch, "E377", {"points": [v(-74.75, 79.4) * mm, v(-75.46, 80.12) * mm, v(-73.94, 81.82) * mm, v(-74.75, 82.4) * mm]});
            skFitSpline(sketch, "E378", {"points": [v(-74.75, 82.4) * mm, v(-75.86, 83.22) * mm, v(-78.43, 82.98) * mm, v(-78.87, 82.4) * mm]});
            skFitSpline(sketch, "E379", {"points": [v(-78.87, 82.4) * mm, v(-79.32, 81.84) * mm, v(-77.41, 80.15) * mm, v(-78.12, 79.4) * mm]});
            skFitSpline(sketch, "E380", {"points": [v(-78.12, 79.4) * mm, v(-78.96, 78.54) * mm, v(-81.24, 79.92) * mm, v(-81.75, 79.4) * mm]});
            skFitSpline(sketch, "E381", {"points": [v(-81.75, 79.4) * mm, v(-82.26, 78.9) * mm, v(-82.26, 73.42) * mm, v(-81.75, 72.9) * mm]});
            skFitSpline(sketch, "E382", {"points": [v(-81.75, 72.9) * mm, v(-81.24, 72.4) * mm, v(-79.63, 73.38) * mm, v(-78.75, 72.9) * mm]});
            skFitSpline(sketch, "E383", {"points": [v(-78.75, 72.9) * mm, v(-77.3, 72.13) * mm, v(-76.9, 69.58) * mm, v(-75.25, 69.4) * mm]});
            skFitSpline(sketch, "E384", {"points": [v(-75.25, 69.4) * mm, v(-65.47, 68.37) * mm, v(-55.53, 68.37) * mm, v(-45.75, 69.4) * mm]});
            skFitSpline(sketch, "E385", {"points": [v(-45.75, 69.4) * mm, v(-44.1, 69.58) * mm, v(-43.8, 72.34) * mm, v(-42.25, 72.9) * mm]});
            skFitSpline(sketch, "E386", {"points": [v(-42.25, 72.9) * mm, v(-40.37, 73.6) * mm, v(-38.13, 73.6) * mm, v(-36.25, 72.9) * mm]});
            skFitSpline(sketch, "E387", {"points": [v(-36.25, 72.9) * mm, v(-34.7, 72.34) * mm, v(-33.3, 70.97) * mm, v(-32.75, 69.4) * mm]});
            skFitSpline(sketch, "E388", {"points": [v(-32.75, 69.4) * mm, v(-32.03, 67.36) * mm, v(-32.24, 63.42) * mm, v(-32.75, 62.9) * mm]});
            skFitSpline(sketch, "E389", {"points": [v(-32.75, 62.9) * mm, v(-33.26, 62.4) * mm, v(-41.74, 63.42) * mm, v(-42.25, 62.9) * mm]});
            skFitSpline(sketch, "E390", {"points": [v(-42.25, 62.9) * mm, v(-42.76, 62.4) * mm, v(-42.76, 60.42) * mm, v(-42.25, 59.9) * mm]});
            skFitSpline(sketch, "E391", {"points": [v(-42.25, 59.9) * mm, v(-41.74, 59.4) * mm, v(-23.26, 60.42) * mm, v(-22.75, 59.9) * mm]});
            skFitSpline(sketch, "E392", {"points": [v(-22.75, 59.9) * mm, v(-22.24, 59.4) * mm, v(-22.24, 53.92) * mm, v(-22.75, 53.4) * mm]});
            skFitSpline(sketch, "E393", {"points": [v(-22.75, 53.4) * mm, v(-23.26, 52.9) * mm, v(-25.74, 53.92) * mm, v(-26.25, 53.4) * mm]});
            skFitSpline(sketch, "E394", {"points": [v(-26.25, 53.4) * mm, v(-26.76, 52.9) * mm, v(-26.76, 50.42) * mm, v(-26.25, 49.9) * mm]});
            skFitSpline(sketch, "E395", {"points": [v(-26.25, 49.9) * mm, v(-25.74, 49.4) * mm, v(-21.8, 50.62) * mm, v(-19.75, 49.9) * mm]});
            skFitSpline(sketch, "E396", {"points": [v(-19.75, 49.9) * mm, v(-18.2, 49.36) * mm, v(-16.82, 47.96) * mm, v(-16.25, 46.4) * mm]});
            skFitSpline(sketch, "E397", {"points": [v(-16.25, 46.4) * mm, v(-15.56, 44.53) * mm, v(-16.94, 42.29) * mm, v(-16.25, 40.4) * mm]});
            skFitSpline(sketch, "E398", {"points": [v(-16.25, 40.4) * mm, v(-15.68, 38.86) * mm, v(-13.3, 38.47) * mm, v(-12.75, 36.9) * mm]});
            skFitSpline(sketch, "E399", {"points": [v(-12.75, 36.9) * mm, v(-12.03, 34.86) * mm, v(-12.24, 30.92) * mm, v(-12.75, 30.4) * mm]});
            skFitSpline(sketch, "E400", {"points": [v(-12.75, 30.4) * mm, v(-13.26, 29.9) * mm, v(-14.87, 29.93) * mm, v(-15.75, 30.4) * mm]});
            skFitSpline(sketch, "E401", {"points": [v(-15.75, 30.4) * mm, v(-17.2, 31.2) * mm, v(-18.7, 32.35) * mm, v(-19.25, 33.9) * mm]});
            skFitSpline(sketch, "E402", {"points": [v(-19.25, 33.9) * mm, v(-19.97, 35.95) * mm, v(-18.74, 39.9) * mm, v(-19.25, 40.4) * mm]});
            skFitSpline(sketch, "E403", {"points": [v(-19.25, 40.4) * mm, v(-19.76, 40.92) * mm, v(-28.74, 39.9) * mm, v(-29.25, 40.4) * mm]});
            skFitSpline(sketch, "E404", {"points": [v(-29.25, 40.4) * mm, v(-29.76, 40.92) * mm, v(-28.74, 52.9) * mm, v(-29.25, 53.4) * mm]});
            skFitSpline(sketch, "E405", {"points": [v(-29.25, 53.4) * mm, v(-29.76, 53.92) * mm, v(-32.24, 53.92) * mm, v(-32.75, 53.4) * mm]});
            skFitSpline(sketch, "E406", {"points": [v(-32.75, 53.4) * mm, v(-33.26, 52.9) * mm, v(-32.06, 47.02) * mm, v(-32.75, 46.78) * mm]});
            skFitSpline(sketch, "E407", {"points": [v(-32.75, 46.78) * mm, v(-33.44, 46.54) * mm, v(-34.05, 49.33) * mm, v(-35.25, 49.9) * mm]});
            skFitSpline(sketch, "E408", {"points": [v(-35.25, 49.9) * mm, v(-36.45, 50.49) * mm, v(-38.74, 50.42) * mm, v(-39.25, 49.9) * mm]});
            skFitSpline(sketch, "E409", {"points": [v(-39.25, 49.9) * mm, v(-39.76, 49.4) * mm, v(-39.72, 47.79) * mm, v(-39.25, 46.9) * mm]});
            skFitSpline(sketch, "E410", {"points": [v(-39.25, 46.9) * mm, v(-38.47, 45.46) * mm, v(-37.2, 44.2) * mm, v(-35.75, 43.4) * mm]});
            skFitSpline(sketch, "E411", {"points": [v(-35.75, 43.4) * mm, v(-34.87, 42.93) * mm, v(-33.46, 44.12) * mm, v(-32.75, 43.4) * mm]});
            skFitSpline(sketch, "E412", {"points": [v(-32.75, 43.4) * mm, v(-32.04, 42.7) * mm, v(-32.24, 40.92) * mm, v(-32.75, 40.4) * mm]});
            skFitSpline(sketch, "E413", {"points": [v(-32.75, 40.4) * mm, v(-33.26, 39.9) * mm, v(-45.24, 39.9) * mm, v(-45.75, 40.4) * mm]});
            skFitSpline(sketch, "E414", {"points": [v(-45.75, 40.4) * mm, v(-46.26, 40.92) * mm, v(-46.26, 49.4) * mm, v(-45.75, 49.9) * mm]});
            skFitSpline(sketch, "E415", {"points": [v(-45.75, 49.9) * mm, v(-45.24, 50.42) * mm, v(-43.07, 49.08) * mm, v(-42.25, 49.9) * mm]});
            skFitSpline(sketch, "E416", {"points": [v(-42.25, 49.9) * mm, v(-41.42, 50.73) * mm, v(-41.42, 52.58) * mm, v(-42.25, 53.4) * mm]});
            skFitSpline(sketch, "E417", {"points": [v(-42.25, 53.4) * mm, v(-43.07, 54.23) * mm, v(-45.24, 52.9) * mm, v(-45.75, 53.4) * mm]});
            skFitSpline(sketch, "E418", {"points": [v(-45.75, 53.4) * mm, v(-46.26, 53.92) * mm, v(-44.88, 60.2) * mm, v(-45.75, 63.4) * mm]});
            skFitSpline(sketch, "E419", {"points": [v(-45.75, 63.4) * mm, v(-46.15, 64.9) * mm, v(-47.85, 65.77) * mm, v(-49.25, 66.4) * mm]});
            skFitSpline(sketch, "E420", {"points": [v(-49.25, 66.4) * mm, v(-50.16, 66.83) * mm, v(-51.74, 66.92) * mm, v(-52.25, 66.4) * mm]});
            skFitSpline(sketch, "E421", {"points": [v(-52.25, 66.4) * mm, v(-52.76, 65.9) * mm, v(-52.74, 63.97) * mm, v(-52.25, 62.9) * mm]});
            skFitSpline(sketch, "E422", {"points": [v(-52.25, 62.9) * mm, v(-51.66, 61.62) * mm, v(-48.97, 60.58) * mm, v(-49.25, 59.9) * mm]});
            skFitSpline(sketch, "E423", {"points": [v(-49.25, 59.9) * mm, v(-49.53, 59.24) * mm, v(-58.24, 59.4) * mm, v(-58.75, 59.9) * mm]});
            skFitSpline(sketch, "E424", {"points": [v(-58.75, 59.9) * mm, v(-59.26, 60.42) * mm, v(-58.26, 62.35) * mm, v(-58.75, 63.4) * mm]});
            skFitSpline(sketch, "E425", {"points": [v(-58.75, 63.4) * mm, v(-59.34, 64.7) * mm, v(-60.6, 65.59) * mm, v(-61.75, 66.4) * mm]});
            skFitSpline(sketch, "E426", {"points": [v(-61.75, 66.4) * mm, v(-61.94, 66.55) * mm, v(-62.26, 66.14) * mm, v(-62.25, 65.9) * mm]});
            skFitSpline(sketch, "E427", {"points": [v(-62.25, 65.9) * mm, v(-62.22, 64.89) * mm, v(-61.19, 63.47) * mm, v(-61.65, 62.9) * mm]});
            skFitSpline(sketch, "E428", {"points": [v(-61.65, 62.9) * mm, v(-62.11, 62.35) * mm, v(-64.17, 62.38) * mm, v(-65.25, 62.9) * mm]});
            skFitSpline(sketch, "E429", {"points": [v(-65.25, 62.9) * mm, v(-66.73, 63.64) * mm, v(-67.14, 66.07) * mm, v(-68.75, 66.4) * mm]});
            skFitSpline(sketch, "E430", {"points": [v(-68.75, 66.4) * mm, v(-72.99, 67.3) * mm, v(-81.24, 66.92) * mm, v(-81.75, 66.4) * mm]});
            skFitSpline(sketch, "E431", {"points": [v(-81.75, 66.4) * mm, v(-82.26, 65.9) * mm, v(-82.26, 63.42) * mm, v(-81.75, 62.9) * mm]});
            skFitSpline(sketch, "E432", {"points": [v(-81.75, 62.9) * mm, v(-81.24, 62.4) * mm, v(-72.86, 64.28) * mm, v(-68.75, 62.9) * mm]});
            skFitSpline(sketch, "E433", {"points": [v(-68.75, 62.9) * mm, v(-65.84, 61.94) * mm, v(-65.16, 57.35) * mm, v(-62.25, 56.4) * mm]});
            skFitSpline(sketch, "E434", {"points": [v(-62.25, 56.4) * mm, v(-57.96, 55.02) * mm, v(-49.22, 56.94) * mm, v(-48.72, 56.4) * mm]});
            skFitSpline(sketch, "E435", {"points": [v(-48.72, 56.4) * mm, v(-48.22, 55.88) * mm, v(-48.68, 47.15) * mm, v(-49.29, 46.75) * mm]});
            skFitSpline(sketch, "E436", {"points": [v(-49.29, 46.75) * mm, v(-49.9, 46.34) * mm, v(-58.16, 50.5) * mm, v(-58.75, 50.09) * mm]});
            skFitSpline(sketch, "E437", {"points": [v(-58.75, 50.09) * mm, v(-59.34, 49.67) * mm, v(-59.25, 47.53) * mm, v(-58.75, 46.4) * mm]});
            skFitSpline(sketch, "E438", {"points": [v(-58.75, 46.4) * mm, v(-58.17, 45.12) * mm, v(-57.1, 43.82) * mm, v(-55.75, 43.4) * mm]});
            skFitSpline(sketch, "E439", {"points": [v(-55.75, 43.4) * mm, v(-53.51, 42.74) * mm, v(-49.26, 43.92) * mm, v(-48.75, 43.4) * mm]});
            skFitSpline(sketch, "E440", {"points": [v(-48.75, 43.4) * mm, v(-48.24, 42.9) * mm, v(-48.24, 40.92) * mm, v(-48.75, 40.4) * mm]});
            skFitSpline(sketch, "E441", {"points": [v(-48.75, 40.4) * mm, v(-49.26, 39.9) * mm, v(-57.82, 39.6) * mm, v(-62.25, 40.4) * mm]});
            skFitSpline(sketch, "E442", {"points": [v(-62.25, 40.4) * mm, v(-63.64, 40.66) * mm, v(-64.93, 42.03) * mm, v(-65.25, 43.4) * mm]});
            skFitSpline(sketch, "E443", {"points": [v(-65.25, 43.4) * mm, v(-66, 46.66) * mm, v(-64.41, 50.18) * mm, v(-65.25, 53.4) * mm]});
            skFitSpline(sketch, "E444", {"points": [v(-65.25, 53.4) * mm, v(-65.66, 55) * mm, v(-68.08, 57.19) * mm, v(-68.75, 56.9) * mm]});
            skFitSpline(sketch, "E445", {"points": [v(-68.75, 56.9) * mm, v(-69.42, 56.63) * mm, v(-68, 54.3) * mm, v(-68.75, 53.4) * mm]});
            skFitSpline(sketch, "E446", {"points": [v(-68.75, 53.4) * mm, v(-69.4, 52.65) * mm, v(-71.24, 52.9) * mm, v(-71.75, 53.4) * mm]});
            skFitSpline(sketch, "E447", {"points": [v(-71.75, 53.4) * mm, v(-72.26, 53.92) * mm, v(-71.24, 59.4) * mm, v(-71.75, 59.9) * mm]});
            skFitSpline(sketch, "E448", {"points": [v(-71.75, 59.9) * mm, v(-72.26, 60.42) * mm, v(-74.89, 60.47) * mm, v(-75.35, 59.9) * mm]});
            skFitSpline(sketch, "E449", {"points": [v(-75.35, 59.9) * mm, v(-75.81, 59.35) * mm, v(-74.19, 56.97) * mm, v(-74.65, 56.4) * mm]});
            skFitSpline(sketch, "E450", {"points": [v(-74.65, 56.4) * mm, v(-75.11, 55.85) * mm, v(-79.17, 55.69) * mm, v(-81.25, 56.4) * mm]});
            skFitSpline(sketch, "E451", {"points": [v(-81.25, 56.4) * mm, v(-82.8, 56.95) * mm, v(-83.97, 58.46) * mm, v(-84.75, 59.9) * mm]});
            skFitSpline(sketch, "E452", {"points": [v(-84.75, 59.9) * mm, v(-85.22, 60.79) * mm, v(-84.19, 62.08) * mm, v(-84.75, 62.9) * mm]});
            skFitSpline(sketch, "E453", {"points": [v(-84.75, 62.9) * mm, v(-86.48, 65.44) * mm, v(-90.13, 66.56) * mm, v(-91.25, 69.4) * mm]});
            skFitSpline(sketch, "E454", {"points": [v(-91.25, 69.4) * mm, v(-92.48, 72.54) * mm, v(-90.38, 76.25) * mm, v(-91.25, 79.5) * mm]});
            skFitSpline(sketch, "E455", {"points": [v(-91.25, 79.5) * mm, v(-91.64, 80.96) * mm, v(-93.23, 82.3) * mm, v(-94.75, 82.4) * mm]});
            skFitSpline(sketch, "E456", {"points": [v(-94.75, 82.4) * mm, v(-107.89, 83.3) * mm, v(-121.12, 83.34) * mm, v(-134.25, 82.4) * mm]});
            skFitSpline(sketch, "E457", {"points": [v(-134.25, 82.4) * mm, v(-135.66, 82.3) * mm, v(-136.82, 80.76) * mm, v(-137.25, 79.4) * mm]});
            skFitSpline(sketch, "E458", {"points": [v(-137.25, 79.4) * mm, v(-137.9, 77.34) * mm, v(-137.76, 73.42) * mm, v(-137.25, 72.9) * mm]});
            skFitSpline(sketch, "E459", {"points": [v(-137.25, 72.9) * mm, v(-136.74, 72.4) * mm, v(-134.26, 72.4) * mm, v(-133.75, 72.9) * mm]});
            skFitSpline(sketch, "E460", {"points": [v(-133.75, 72.9) * mm, v(-133.24, 73.42) * mm, v(-134.22, 75.03) * mm, v(-133.75, 75.9) * mm]});
            skFitSpline(sketch, "E461", {"points": [v(-133.75, 75.9) * mm, v(-132.97, 77.36) * mm, v(-131.73, 78.67) * mm, v(-130.25, 79.4) * mm]});
            skFitSpline(sketch, "E462", {"points": [v(-130.25, 79.4) * mm, v(-129.2, 79.93) * mm, v(-127.26, 79.92) * mm, v(-126.75, 79.4) * mm]});
            skFitSpline(sketch, "E463", {"points": [v(-126.75, 79.4) * mm, v(-126.24, 78.9) * mm, v(-126.03, 77.14) * mm, v(-126.75, 76.5) * mm]});
            skFitSpline(sketch, "E464", {"points": [v(-126.75, 76.5) * mm, v(-127.76, 75.6) * mm, v(-130.09, 77) * mm, v(-130.75, 75.83) * mm]});
            skFitSpline(sketch, "E465", {"points": [v(-130.75, 75.83) * mm, v(-131.8, 73.96) * mm, v(-130.24, 69.92) * mm, v(-130.75, 69.4) * mm]});
            skFitSpline(sketch, "E466", {"points": [v(-130.75, 69.4) * mm, v(-131.26, 68.9) * mm, v(-140.24, 68.9) * mm, v(-140.75, 69.4) * mm]});
            skFitSpline(sketch, "E467", {"points": [v(-140.75, 69.4) * mm, v(-141.26, 69.92) * mm, v(-140.24, 78.9) * mm, v(-140.75, 79.4) * mm]});
            skFitSpline(sketch, "E468", {"points": [v(-140.75, 79.4) * mm, v(-141.26, 79.92) * mm, v(-143.24, 79.92) * mm, v(-143.75, 79.4) * mm]});
            skFitSpline(sketch, "E469", {"points": [v(-143.75, 79.4) * mm, v(-144.26, 78.9) * mm, v(-143.1, 74.98) * mm, v(-143.75, 72.9) * mm]});
            skFitSpline(sketch, "E470", {"points": [v(-143.75, 72.9) * mm, v(-144.18, 71.56) * mm, v(-146.2, 71.2) * mm, v(-146.75, 69.9) * mm]});
            skFitSpline(sketch, "E471", {"points": [v(-146.75, 69.9) * mm, v(-147.27, 68.68) * mm, v(-147.26, 66.42) * mm, v(-146.75, 65.9) * mm]});
            skFitSpline(sketch, "E472", {"points": [v(-146.75, 65.9) * mm, v(-146.24, 65.4) * mm, v(-131.26, 66.42) * mm, v(-130.75, 65.9) * mm]});
            skFitSpline(sketch, "E473", {"points": [v(-130.75, 65.9) * mm, v(-130.24, 65.4) * mm, v(-131.5, 63.56) * mm, v(-130.75, 62.9) * mm]});
            skFitSpline(sketch, "E474", {"points": [v(-130.75, 62.9) * mm, v(-129.86, 62.15) * mm, v(-127.76, 62.4) * mm, v(-127.25, 62.9) * mm]});
            skFitSpline(sketch, "E475", {"points": [v(-127.25, 62.9) * mm, v(-126.74, 63.42) * mm, v(-127.76, 65.4) * mm, v(-127.25, 65.9) * mm]});
            skFitSpline(sketch, "E476", {"points": [v(-127.25, 65.9) * mm, v(-126.74, 66.42) * mm, v(-105.53, 66.96) * mm, v(-94.75, 65.9) * mm]});
            skFitSpline(sketch, "E477", {"points": [v(-94.75, 65.9) * mm, v(-93.1, 65.75) * mm, v(-91.99, 63.88) * mm, v(-91.25, 62.4) * mm]});
            skFitSpline(sketch, "E478", {"points": [v(-91.25, 62.4) * mm, v(-90.87, 61.65) * mm, v(-92.26, 60.59) * mm, v(-91.75, 59.9) * mm]});
            skFitSpline(sketch, "E479", {"points": [v(-91.75, 59.9) * mm, v(-88.9, 56.16) * mm, v(-85.78, 52.35) * mm, v(-81.75, 49.9) * mm]});
            skFitSpline(sketch, "E480", {"points": [v(-81.75, 49.9) * mm, v(-79.9, 48.79) * mm, v(-77.19, 50.88) * mm, v(-75.25, 49.9) * mm]});
            skFitSpline(sketch, "E481", {"points": [v(-75.25, 49.9) * mm, v(-72.5, 48.54) * mm, v(-70.48, 45.94) * mm, v(-68.75, 43.4) * mm]});
            skFitSpline(sketch, "E482", {"points": [v(-68.75, 43.4) * mm, v(-68.19, 42.58) * mm, v(-68.24, 40.92) * mm, v(-68.75, 40.4) * mm]});
            skFitSpline(sketch, "E483", {"points": [v(-68.75, 40.4) * mm, v(-69.26, 39.9) * mm, v(-74.74, 40.92) * mm, v(-75.25, 40.4) * mm]});
            skFitSpline(sketch, "E484", {"points": [v(-75.25, 40.4) * mm, v(-75.76, 39.9) * mm, v(-75.76, 37.42) * mm, v(-75.25, 36.9) * mm]});
            skFitSpline(sketch, "E485", {"points": [v(-75.25, 36.9) * mm, v(-74.74, 36.4) * mm, v(-68.5, 37.66) * mm, v(-65.25, 36.9) * mm]});
            skFitSpline(sketch, "E486", {"points": [v(-65.25, 36.9) * mm, v(-63.87, 36.6) * mm, v(-63.53, 34.5) * mm, v(-62.25, 33.9) * mm]});
            skFitSpline(sketch, "E487", {"points": [v(-62.25, 33.9) * mm, v(-61.2, 33.42) * mm, v(-59.57, 34.73) * mm, v(-58.75, 33.9) * mm]});
            skFitSpline(sketch, "E488", {"points": [v(-58.75, 33.9) * mm, v(-57.92, 33.08) * mm, v(-58.24, 30.92) * mm, v(-58.75, 30.4) * mm]});
            skFitSpline(sketch, "E489", {"points": [v(-58.75, 30.4) * mm, v(-59.26, 29.9) * mm, v(-61.74, 30.92) * mm, v(-62.25, 30.4) * mm]});
            skFitSpline(sketch, "E490", {"points": [v(-62.25, 30.4) * mm, v(-62.76, 29.9) * mm, v(-62.76, 27.42) * mm, v(-62.25, 26.9) * mm]});
            skFitSpline(sketch, "E491", {"points": [v(-62.25, 26.9) * mm, v(-61.74, 26.4) * mm, v(-49.76, 27.42) * mm, v(-49.25, 26.9) * mm]});
            skFitSpline(sketch, "E492", {"points": [v(-49.25, 26.9) * mm, v(-48.74, 26.4) * mm, v(-50.5, 22.47) * mm, v(-49.25, 20.9) * mm]});
            skFitSpline(sketch, "E493", {"points": [v(-49.25, 20.9) * mm, v(-46.77, 17.8) * mm, v(-41.31, 17.8) * mm, v(-39.25, 14.4) * mm]});
            skFitSpline(sketch, "E494", {"points": [v(-39.25, 14.4) * mm, v(-37.52, 11.56) * mm, v(-38.74, 4.92) * mm, v(-39.25, 4.4) * mm]});
            skFitSpline(sketch, "E495", {"points": [v(-39.25, 4.4) * mm, v(-39.76, 3.9) * mm, v(-41.37, 3.93) * mm, v(-42.25, 4.4) * mm]});
            skFitSpline(sketch, "E496", {"points": [v(-42.25, 4.4) * mm, v(-43.7, 5.2) * mm, v(-45.01, 6.43) * mm, v(-45.75, 7.9) * mm]});
            skFitSpline(sketch, "E497", {"points": [v(-45.75, 7.9) * mm, v(-46.27, 8.95) * mm, v(-45.26, 10.35) * mm, v(-45.75, 11.4) * mm]});
            skFitSpline(sketch, "E498", {"points": [v(-45.75, 11.4) * mm, v(-46.34, 12.7) * mm, v(-47.4, 14) * mm, v(-48.75, 14.4) * mm]});
            skFitSpline(sketch, "E499", {"points": [v(-48.75, 14.4) * mm, v(-49.55, 14.65) * mm, v(-49.92, 12.9) * mm, v(-50.75, 12.9) * mm]});
            skFitSpline(sketch, "E500", {"points": [v(-50.75, 12.9) * mm, v(-51.46, 12.9) * mm, v(-52.12, 13.71) * mm, v(-52.25, 14.4) * mm]});
            skFitSpline(sketch, "E501", {"points": [v(-52.25, 14.4) * mm, v(-52.65, 16.54) * mm, v(-51.6, 18.84) * mm, v(-52.25, 20.9) * mm]});
            skFitSpline(sketch, "E502", {"points": [v(-52.25, 20.9) * mm, v(-52.68, 22.26) * mm, v(-53.87, 23.6) * mm, v(-55.25, 23.9) * mm]});
            skFitSpline(sketch, "E503", {"points": [v(-55.25, 23.9) * mm, v(-58.5, 24.66) * mm, v(-64.74, 24.42) * mm, v(-65.25, 23.9) * mm]});
            skFitSpline(sketch, "E504", {"points": [v(-65.25, 23.9) * mm, v(-65.76, 23.4) * mm, v(-65.76, 21.42) * mm, v(-65.25, 20.9) * mm]});
            skFitSpline(sketch, "E505", {"points": [v(-65.25, 20.9) * mm, v(-64.74, 20.4) * mm, v(-61.1, 21.65) * mm, v(-59.25, 20.9) * mm]});
            skFitSpline(sketch, "E506", {"points": [v(-59.25, 20.9) * mm, v(-57.5, 20.2) * mm, v(-56.24, 18.51) * mm, v(-55.25, 16.9) * mm]});
            skFitSpline(sketch, "E507", {"points": [v(-55.25, 16.9) * mm, v(-54.81, 16.2) * mm, v(-54.79, 15.1) * mm, v(-55.25, 14.4) * mm]});
            skFitSpline(sketch, "E508", {"points": [v(-55.25, 14.4) * mm, v(-56.23, 12.93) * mm, v(-57.58, 11.5) * mm, v(-59.25, 10.9) * mm]});
            skFitSpline(sketch, "E509", {"points": [v(-59.25, 10.9) * mm, v(-61.14, 10.25) * mm, v(-64.74, 11.42) * mm, v(-65.25, 10.9) * mm]});
            skFitSpline(sketch, "E510", {"points": [v(-65.25, 10.9) * mm, v(-65.76, 10.4) * mm, v(-65.72, 8.79) * mm, v(-65.25, 7.9) * mm]});
            skFitSpline(sketch, "E511", {"points": [v(-65.25, 7.9) * mm, v(-64.47, 6.46) * mm, v(-63.2, 5.2) * mm, v(-61.75, 4.4) * mm]});
            skFitSpline(sketch, "E512", {"points": [v(-61.75, 4.4) * mm, v(-60.87, 3.93) * mm, v(-59.26, 3.9) * mm, v(-58.75, 4.4) * mm]});
            skFitSpline(sketch, "E513", {"points": [v(-58.75, 4.4) * mm, v(-58.24, 4.92) * mm, v(-59.26, 6.9) * mm, v(-58.75, 7.4) * mm]});
            skFitSpline(sketch, "E514", {"points": [v(-58.75, 7.4) * mm, v(-58.24, 7.92) * mm, v(-51.85, 8.63) * mm, v(-48.75, 7.4) * mm]});
            skFitSpline(sketch, "E515", {"points": [v(-48.75, 7.4) * mm, v(-45.9, 6.29) * mm, v(-44.04, 3.4) * mm, v(-42.25, 0.9) * mm]});
            skFitSpline(sketch, "E516", {"points": [v(-42.25, 0.9) * mm, v(-41.76, 0.23) * mm, v(-41.74, -1.08) * mm, v(-42.25, -1.6) * mm]});
            skFitSpline(sketch, "E517", {"points": [v(-42.25, -1.6) * mm, v(-42.76, -2.1) * mm, v(-62.47, -0.92) * mm, v(-62.75, -1.6) * mm]});
            skFitSpline(sketch, "E518", {"points": [v(-62.75, -1.6) * mm, v(-63.03, -2.26) * mm, v(-60.82, -4.57) * mm, v(-59.25, -5.1) * mm]});
            skFitSpline(sketch, "E519", {"points": [v(-59.25, -5.1) * mm, v(-57.04, -5.83) * mm, v(-54.46, -4.35) * mm, v(-52.25, -5.1) * mm]});
            skFitSpline(sketch, "E520", {"points": [v(-52.25, -5.1) * mm, v(-50.68, -5.61) * mm, v(-50.2, -7.8) * mm, v(-48.75, -8.6) * mm]});
            skFitSpline(sketch, "E521", {"points": [v(-48.75, -8.6) * mm, v(-47.87, -9.06) * mm, v(-46.26, -9.1) * mm, v(-45.75, -8.6) * mm]});
            skFitSpline(sketch, "E522", {"points": [v(-45.75, -8.6) * mm, v(-45.24, -8.08) * mm, v(-46.26, -5.6) * mm, v(-45.75, -5.1) * mm]});
            skFitSpline(sketch, "E523", {"points": [v(-45.75, -5.1) * mm, v(-45.24, -4.58) * mm, v(-41.3, -4.38) * mm, v(-39.25, -5.1) * mm]});
            skFitSpline(sketch, "E524", {"points": [v(-39.25, -5.1) * mm, v(-37.7, -5.64) * mm, v(-35.96, -6.95) * mm, v(-35.75, -8.6) * mm]});
            skFitSpline(sketch, "E525", {"points": [v(-35.75, -8.6) * mm, v(-34.91, -15.04) * mm, v(-35.66, -27.5) * mm, v(-36.26, -28.1) * mm]});
            skFitSpline(sketch, "E526", {"points": [v(-36.26, -28.1) * mm, v(-36.87, -28.68) * mm, v(-38.74, -28.6) * mm, v(-39.25, -28.1) * mm]});
            skFitSpline(sketch, "E527", {"points": [v(-39.25, -28.1) * mm, v(-39.76, -27.58) * mm, v(-38.74, -15.6) * mm, v(-39.25, -15.1) * mm]});
            skFitSpline(sketch, "E528", {"points": [v(-39.25, -15.1) * mm, v(-39.76, -14.58) * mm, v(-41.74, -14.58) * mm, v(-42.25, -15.1) * mm]});
            skFitSpline(sketch, "E529", {"points": [v(-42.25, -15.1) * mm, v(-42.76, -15.6) * mm, v(-41.74, -24.08) * mm, v(-42.25, -24.6) * mm]});
            skFitSpline(sketch, "E530", {"points": [v(-42.25, -24.6) * mm, v(-42.76, -25.1) * mm, v(-46.7, -25.3) * mm, v(-48.75, -24.6) * mm]});
            skFitSpline(sketch, "E531", {"points": [v(-48.75, -24.6) * mm, v(-50.3, -24.05) * mm, v(-51.82, -22.68) * mm, v(-52.25, -21.1) * mm]});
            skFitSpline(sketch, "E532", {"points": [v(-52.25, -21.1) * mm, v(-53.07, -18.03) * mm, v(-51.51, -14.67) * mm, v(-52.25, -11.6) * mm]});
            skFitSpline(sketch, "E533", {"points": [v(-52.25, -11.6) * mm, v(-52.58, -10.22) * mm, v(-53.9, -9.02) * mm, v(-55.25, -8.6) * mm]});
            skFitSpline(sketch, "E534", {"points": [v(-55.25, -8.6) * mm, v(-57.32, -7.94) * mm, v(-59.7, -9.3) * mm, v(-61.75, -8.6) * mm]});
            skFitSpline(sketch, "E535", {"points": [v(-61.75, -8.6) * mm, v(-63.3, -8.05) * mm, v(-64.51, -6.57) * mm, v(-65.25, -5.1) * mm]});
            skFitSpline(sketch, "E536", {"points": [v(-65.25, -5.1) * mm, v(-65.77, -4.05) * mm, v(-64.73, -2.63) * mm, v(-65.25, -1.6) * mm]});
            skFitSpline(sketch, "E537", {"points": [v(-65.25, -1.6) * mm, v(-65.99, -0.12) * mm, v(-68.53, 0.27) * mm, v(-68.75, 1.9) * mm]});
            skFitSpline(sketch, "E538", {"points": [v(-68.75, 1.9) * mm, v(-69.75, 9.17) * mm, v(-68.24, 23.4) * mm, v(-68.75, 23.9) * mm]});
            skFitSpline(sketch, "E539", {"points": [v(-68.75, 23.9) * mm, v(-69.26, 24.42) * mm, v(-70.73, 24.48) * mm, v(-71.4, 23.9) * mm]});
            skFitSpline(sketch, "E540", {"points": [v(-71.4, 23.9) * mm, v(-73.1, 22.46) * mm, v(-75.38, 19.94) * mm, v(-75.25, 18.4) * mm]});
            skFitSpline(sketch, "E541", {"points": [v(-75.25, 18.4) * mm, v(-75.12, 16.88) * mm, v(-72.45, 16.4) * mm, v(-71.75, 14.9) * mm]});
            skFitSpline(sketch, "E542", {"points": [v(-71.75, 14.9) * mm, v(-71.19, 13.7) * mm, v(-71.24, 11.42) * mm, v(-71.75, 10.9) * mm]});
            skFitSpline(sketch, "E543", {"points": [v(-71.75, 10.9) * mm, v(-72.26, 10.4) * mm, v(-73.87, 10.43) * mm, v(-74.75, 10.9) * mm]});
            skFitSpline(sketch, "E544", {"points": [v(-74.75, 10.9) * mm, v(-76.2, 11.7) * mm, v(-77.47, 12.96) * mm, v(-78.25, 14.4) * mm]});
            skFitSpline(sketch, "E545", {"points": [v(-78.25, 14.4) * mm, v(-78.72, 15.29) * mm, v(-77.78, 16.53) * mm, v(-78.25, 17.4) * mm]});
            skFitSpline(sketch, "E546", {"points": [v(-78.25, 17.4) * mm, v(-79.03, 18.86) * mm, v(-81.18, 19.36) * mm, v(-81.75, 20.9) * mm]});
            skFitSpline(sketch, "E547", {"points": [v(-81.75, 20.9) * mm, v(-82.44, 22.79) * mm, v(-82.26, 26.4) * mm, v(-81.75, 26.9) * mm]});
            skFitSpline(sketch, "E548", {"points": [v(-81.75, 26.9) * mm, v(-81.24, 27.42) * mm, v(-78.76, 26.4) * mm, v(-78.25, 26.9) * mm]});
            skFitSpline(sketch, "E549", {"points": [v(-78.25, 26.9) * mm, v(-77.74, 27.42) * mm, v(-77.74, 29.9) * mm, v(-78.25, 30.4) * mm]});
            skFitSpline(sketch, "E550", {"points": [v(-78.25, 30.4) * mm, v(-78.76, 30.92) * mm, v(-80.46, 29.8) * mm, v(-81.25, 30.4) * mm]});
            skFitSpline(sketch, "E551", {"points": [v(-81.25, 30.4) * mm, v(-84.99, 33.28) * mm, v(-88.8, 36.38) * mm, v(-91.25, 40.4) * mm]});
            skFitSpline(sketch, "E552", {"points": [v(-91.25, 40.4) * mm, v(-92.37, 42.26) * mm, v(-90.74, 46.4) * mm, v(-91.25, 46.9) * mm]});
            skFitSpline(sketch, "E553", {"points": [v(-91.25, 46.9) * mm, v(-91.76, 47.42) * mm, v(-94.24, 47.42) * mm, v(-94.75, 46.9) * mm]});
            skFitSpline(sketch, "E554", {"points": [v(-94.75, 46.9) * mm, v(-95.26, 46.4) * mm, v(-94.24, 40.92) * mm, v(-94.75, 40.4) * mm]});
            skFitSpline(sketch, "E555", {"points": [v(-94.75, 40.4) * mm, v(-95.26, 39.9) * mm, v(-100.74, 39.9) * mm, v(-101.25, 40.4) * mm]});
            skFitSpline(sketch, "E556", {"points": [v(-101.25, 40.4) * mm, v(-101.76, 40.92) * mm, v(-101.82, 44.5) * mm, v(-101.25, 46.4) * mm]});
            skFitSpline(sketch, "E557", {"points": [v(-101.25, 46.4) * mm, v(-100.77, 48) * mm, v(-98.15, 49.03) * mm, v(-98.25, 50.4) * mm]});
            skFitSpline(sketch, "E558", {"points": [v(-98.25, 50.4) * mm, v(-98.35, 51.79) * mm, v(-103.62, 58.17) * mm, v(-107.75, 59.9) * mm]});
            skFitSpline(sketch, "E559", {"points": [v(-107.75, 59.9) * mm, v(-111.74, 61.6) * mm, v(-120.24, 60.42) * mm, v(-120.75, 59.9) * mm]});
            skFitSpline(sketch, "E560", {"points": [v(-120.75, 59.9) * mm, v(-121.26, 59.4) * mm, v(-120.24, 56.92) * mm, v(-120.75, 56.4) * mm]});
            skFitSpline(sketch, "E561", {"points": [v(-120.75, 56.4) * mm, v(-121.26, 55.9) * mm, v(-140.24, 55.9) * mm, v(-140.75, 56.4) * mm]});
            skFitSpline(sketch, "E562", {"points": [v(-140.75, 56.4) * mm, v(-141.26, 56.92) * mm, v(-140.24, 59.4) * mm, v(-140.75, 59.9) * mm]});
            skFitSpline(sketch, "E563", {"points": [v(-140.75, 59.9) * mm, v(-141.26, 60.42) * mm, v(-149.5, 59.11) * mm, v(-153.75, 59.9) * mm]});
            skFitSpline(sketch, "E564", {"points": [v(-153.75, 59.9) * mm, v(-155.14, 60.17) * mm, v(-156.43, 61.53) * mm, v(-156.75, 62.9) * mm]});
            skFitSpline(sketch, "E565", {"points": [v(-156.75, 62.9) * mm, v(-157.5, 66.16) * mm, v(-157.5, 69.66) * mm, v(-156.75, 72.9) * mm]});
            skFitSpline(sketch, "E566", {"points": [v(-156.75, 72.9) * mm, v(-156.43, 74.29) * mm, v(-154.18, 74.56) * mm, v(-153.75, 75.9) * mm]});
            skFitSpline(sketch, "E567", {"points": [v(-153.75, 75.9) * mm, v(-153.1, 77.98) * mm, v(-153.75, 80.24) * mm, v(-153.75, 82.4) * mm]});
            skFitSpline(sketch, "E568", {"points": [v(-61.75, 75.9) * mm, v(-62.04, 74.96) * mm, v(-62.46, 73.62) * mm, v(-61.75, 72.9) * mm]});
            skFitSpline(sketch, "E569", {"points": [v(-61.75, 72.9) * mm, v(-61.04, 72.2) * mm, v(-59.26, 72.4) * mm, v(-58.75, 72.9) * mm]});
            skFitSpline(sketch, "E570", {"points": [v(-58.75, 72.9) * mm, v(-58.24, 73.42) * mm, v(-59.26, 75.4) * mm, v(-58.75, 75.9) * mm]});
            skFitSpline(sketch, "E571", {"points": [v(-58.75, 75.9) * mm, v(-58.24, 76.42) * mm, v(-56.14, 76.67) * mm, v(-55.25, 75.9) * mm]});
            skFitSpline(sketch, "E572", {"points": [v(-55.25, 75.9) * mm, v(-54.5, 75.26) * mm, v(-55.96, 73.62) * mm, v(-55.25, 72.9) * mm]});
            skFitSpline(sketch, "E573", {"points": [v(-55.25, 72.9) * mm, v(-54.54, 72.2) * mm, v(-52.76, 72.4) * mm, v(-52.25, 72.9) * mm]});
            skFitSpline(sketch, "E574", {"points": [v(-52.25, 72.9) * mm, v(-51.74, 73.42) * mm, v(-52.76, 75.4) * mm, v(-52.25, 75.9) * mm]});
            skFitSpline(sketch, "E575", {"points": [v(-52.25, 75.9) * mm, v(-51.74, 76.42) * mm, v(-49.64, 76.67) * mm, v(-48.75, 75.9) * mm]});
            skFitSpline(sketch, "E576", {"points": [v(-48.75, 75.9) * mm, v(-48, 75.26) * mm, v(-49.42, 73.19) * mm, v(-48.75, 72.9) * mm]});
            skFitSpline(sketch, "E577", {"points": [v(-48.75, 72.9) * mm, v(-48.08, 72.63) * mm, v(-47.14, 75.66) * mm, v(-45.75, 75.9) * mm]});
            skFitSpline(sketch, "E578", {"points": [v(-45.75, 75.9) * mm, v(-41.32, 76.71) * mm, v(-36.68, 76.71) * mm, v(-32.25, 75.9) * mm]});
            skFitSpline(sketch, "E579", {"points": [v(-32.25, 75.9) * mm, v(-30.86, 75.66) * mm, v(-29.57, 74.29) * mm, v(-29.25, 72.9) * mm]});
            skFitSpline(sketch, "E580", {"points": [v(-29.25, 72.9) * mm, v(-28.5, 69.66) * mm, v(-29.76, 63.42) * mm, v(-29.25, 62.9) * mm]});
            skFitSpline(sketch, "E581", {"points": [v(-29.25, 62.9) * mm, v(-28.74, 62.4) * mm, v(-23.26, 62.4) * mm, v(-22.75, 62.9) * mm]});
            skFitSpline(sketch, "E582", {"points": [v(-22.75, 62.9) * mm, v(-22.24, 63.42) * mm, v(-22.28, 65.03) * mm, v(-22.75, 65.9) * mm]});
            skFitSpline(sketch, "E583", {"points": [v(-22.75, 65.9) * mm, v(-23.53, 67.36) * mm, v(-25.7, 67.85) * mm, v(-26.25, 69.4) * mm]});
            skFitSpline(sketch, "E584", {"points": [v(-26.25, 69.4) * mm, v(-26.97, 71.45) * mm, v(-25.53, 73.86) * mm, v(-26.25, 75.9) * mm]});
            skFitSpline(sketch, "E585", {"points": [v(-26.25, 75.9) * mm, v(-26.8, 77.47) * mm, v(-28.1, 79.26) * mm, v(-29.75, 79.4) * mm]});
            skFitSpline(sketch, "E586", {"points": [v(-29.75, 79.4) * mm, v(-41.54, 80.47) * mm, v(-64.74, 78.9) * mm, v(-65.25, 79.4) * mm]});
            skFitSpline(sketch, "E587", {"points": [v(-65.25, 79.4) * mm, v(-65.76, 79.92) * mm, v(-65.76, 81.9) * mm, v(-65.25, 82.4) * mm]});
            skFitSpline(sketch, "E588", {"points": [v(-65.25, 82.4) * mm, v(-64.74, 82.92) * mm, v(-38.88, 83.34) * mm, v(-25.75, 82.4) * mm]});
            skFitSpline(sketch, "E589", {"points": [v(-25.75, 82.4) * mm, v(-24.34, 82.3) * mm, v(-23.18, 80.76) * mm, v(-22.75, 79.4) * mm]});
            skFitSpline(sketch, "E590", {"points": [v(-22.75, 79.4) * mm, v(-22.1, 77.34) * mm, v(-23.47, 74.95) * mm, v(-22.75, 72.9) * mm]});
            skFitSpline(sketch, "E591", {"points": [v(-22.75, 72.9) * mm, v(-22.2, 71.35) * mm, v(-19.5, 71.04) * mm, v(-19.25, 69.4) * mm]});
            skFitSpline(sketch, "E592", {"points": [v(-19.25, 69.4) * mm, v(-18.44, 64.13) * mm, v(-20.27, 53.93) * mm, v(-19.77, 53.4) * mm]});
            skFitSpline(sketch, "E593", {"points": [v(-19.77, 53.4) * mm, v(-19.26, 52.89) * mm, v(-13.26, 52.9) * mm, v(-12.75, 53.4) * mm]});
            skFitSpline(sketch, "E594", {"points": [v(-12.75, 53.4) * mm, v(-12.24, 53.92) * mm, v(-12, 55.76) * mm, v(-12.75, 56.4) * mm]});
            skFitSpline(sketch, "E595", {"points": [v(-12.75, 56.4) * mm, v(-13.64, 57.17) * mm, v(-15.74, 55.9) * mm, v(-16.25, 56.4) * mm]});
            skFitSpline(sketch, "E596", {"points": [v(-16.25, 56.4) * mm, v(-16.76, 56.92) * mm, v(-15.3, 67.16) * mm, v(-16.25, 72.4) * mm]});
            skFitSpline(sketch, "E597", {"points": [v(-16.25, 72.4) * mm, v(-16.54, 74.03) * mm, v(-20.03, 75.24) * mm, v(-19.75, 75.9) * mm]});
            skFitSpline(sketch, "E598", {"points": [v(-19.75, 75.9) * mm, v(-19.47, 76.58) * mm, v(-13.26, 76.42) * mm, v(-12.75, 75.9) * mm]});
            skFitSpline(sketch, "E599", {"points": [v(-12.75, 75.9) * mm, v(-12.24, 75.4) * mm, v(-13.26, 60.42) * mm, v(-12.75, 59.9) * mm]});
            skFitSpline(sketch, "E600", {"points": [v(-12.75, 59.9) * mm, v(-12.24, 59.4) * mm, v(-10.26, 60.42) * mm, v(-9.75, 59.9) * mm]});
            skFitSpline(sketch, "E601", {"points": [v(-9.75, 59.9) * mm, v(-9.24, 59.4) * mm, v(-10.26, 37.42) * mm, v(-9.75, 36.9) * mm]});
            skFitSpline(sketch, "E602", {"points": [v(-9.75, 36.9) * mm, v(-9.24, 36.4) * mm, v(-6.75, 36.4) * mm, v(-6.24, 36.9) * mm]});
            skFitSpline(sketch, "E603", {"points": [v(-6.24, 36.9) * mm, v(-5.73, 37.43) * mm, v(-6.18, 62.34) * mm, v(-6.76, 62.9) * mm]});
            skFitSpline(sketch, "E604", {"points": [v(-6.76, 62.9) * mm, v(-7.34, 63.48) * mm, v(-9.1, 62.15) * mm, v(-9.75, 62.9) * mm]});
            skFitSpline(sketch, "E605", {"points": [v(-9.75, 62.9) * mm, v(-10.5, 63.8) * mm, v(-10.5, 65.52) * mm, v(-9.75, 66.4) * mm]});
            skFitSpline(sketch, "E606", {"points": [v(-9.75, 66.4) * mm, v(-9.1, 67.17) * mm, v(-7.46, 65.7) * mm, v(-6.75, 66.4) * mm]});
            skFitSpline(sketch, "E607", {"points": [v(-6.75, 66.4) * mm, v(-6.04, 67.12) * mm, v(-6.04, 68.7) * mm, v(-6.75, 69.4) * mm]});
            skFitSpline(sketch, "E608", {"points": [v(-6.75, 69.4) * mm, v(-7.46, 70.12) * mm, v(-9.24, 68.9) * mm, v(-9.75, 69.4) * mm]});
            skFitSpline(sketch, "E609", {"points": [v(-9.75, 69.4) * mm, v(-10.26, 69.92) * mm, v(-10.26, 75.4) * mm, v(-9.75, 75.9) * mm]});
            skFitSpline(sketch, "E610", {"points": [v(-9.75, 75.9) * mm, v(-9.24, 76.42) * mm, v(-6.61, 75.35) * mm, v(-6.15, 75.9) * mm]});
            skFitSpline(sketch, "E611", {"points": [v(-6.15, 75.9) * mm, v(-5.69, 76.47) * mm, v(-5.7, 79.11) * mm, v(-6.85, 79.4) * mm]});
            skFitSpline(sketch, "E612", {"points": [v(-6.85, 79.4) * mm, v(-11.01, 80.48) * mm, v(-19.24, 78.9) * mm, v(-19.75, 79.4) * mm]});
            skFitSpline(sketch, "E613", {"points": [v(-19.75, 79.4) * mm, v(-20.26, 79.92) * mm, v(-20.26, 81.9) * mm, v(-19.75, 82.4) * mm]});
            skFitSpline(sketch, "E614", {"points": [v(-19.75, 82.4) * mm, v(-19.24, 82.92) * mm, v(-3.26, 82.92) * mm, v(-2.75, 82.4) * mm]});
            skFitSpline(sketch, "E615", {"points": [v(-2.75, 82.4) * mm, v(-2.23, 81.9) * mm, v(-4.05, 37.06) * mm, v(-3.25, 14.4) * mm]});
            skFitSpline(sketch, "E616", {"points": [v(-3.25, 14.4) * mm, v(-3.2, 13) * mm, v(-1.33, 11.45) * mm, v(-0.25, 11.4) * mm]});
            skFitSpline(sketch, "E617", {"points": [v(-0.25, 11.4) * mm, v(0.83, 11.37) * mm, v(3.19, 12.87) * mm, v(3.25, 14.4) * mm]});
            skFitSpline(sketch, "E618", {"points": [v(3.25, 14.4) * mm, v(4.2, 37.06) * mm, v(2.23, 81.9) * mm, v(2.75, 82.4) * mm]});
            skFitSpline(sketch, "E619", {"points": [v(2.75, 82.4) * mm, v(3.26, 82.92) * mm, v(19.24, 82.92) * mm, v(19.75, 82.4) * mm]});
            skFitSpline(sketch, "E620", {"points": [v(19.75, 82.4) * mm, v(20.26, 81.9) * mm, v(20.26, 79.92) * mm, v(19.75, 79.4) * mm]});
            skFitSpline(sketch, "E621", {"points": [v(19.75, 79.4) * mm, v(19.24, 78.9) * mm, v(11.01, 80.48) * mm, v(6.85, 79.4) * mm]});
            skFitSpline(sketch, "E622", {"points": [v(6.85, 79.4) * mm, v(5.7, 79.11) * mm, v(5.69, 76.47) * mm, v(6.15, 75.9) * mm]});
            skFitSpline(sketch, "E623", {"points": [v(6.15, 75.9) * mm, v(6.61, 75.35) * mm, v(9.24, 76.42) * mm, v(9.75, 75.9) * mm]});
            skFitSpline(sketch, "E624", {"points": [v(9.75, 75.9) * mm, v(10.26, 75.4) * mm, v(10.26, 69.92) * mm, v(9.75, 69.4) * mm]});
            skFitSpline(sketch, "E625", {"points": [v(9.75, 69.4) * mm, v(9.24, 68.9) * mm, v(7.46, 70.12) * mm, v(6.75, 69.4) * mm]});
            skFitSpline(sketch, "E626", {"points": [v(6.75, 69.4) * mm, v(6.04, 68.7) * mm, v(6.04, 67.12) * mm, v(6.75, 66.4) * mm]});
            skFitSpline(sketch, "E627", {"points": [v(6.75, 66.4) * mm, v(7.46, 65.7) * mm, v(9.1, 67.17) * mm, v(9.75, 66.4) * mm]});
            skFitSpline(sketch, "E628", {"points": [v(9.75, 66.4) * mm, v(10.5, 65.52) * mm, v(10.5, 63.8) * mm, v(9.75, 62.9) * mm]});
            skFitSpline(sketch, "E629", {"points": [v(9.75, 62.9) * mm, v(9.1, 62.15) * mm, v(7.34, 63.48) * mm, v(6.76, 62.9) * mm]});
            skFitSpline(sketch, "E630", {"points": [v(6.76, 62.9) * mm, v(6.18, 62.34) * mm, v(5.73, 37.43) * mm, v(6.24, 36.9) * mm]});
            skFitSpline(sketch, "E631", {"points": [v(6.24, 36.9) * mm, v(6.75, 36.4) * mm, v(9.24, 36.4) * mm, v(9.75, 36.9) * mm]});
            skFitSpline(sketch, "E632", {"points": [v(9.75, 36.9) * mm, v(10.26, 37.42) * mm, v(9.24, 59.4) * mm, v(9.75, 59.9) * mm]});
            skFitSpline(sketch, "E633", {"points": [v(9.75, 59.9) * mm, v(10.26, 60.42) * mm, v(12.24, 59.4) * mm, v(12.75, 59.9) * mm]});
            skFitSpline(sketch, "E634", {"points": [v(12.75, 59.9) * mm, v(13.26, 60.42) * mm, v(12.24, 75.4) * mm, v(12.75, 75.9) * mm]});
            skFitSpline(sketch, "E635", {"points": [v(12.75, 75.9) * mm, v(13.26, 76.42) * mm, v(19.47, 76.58) * mm, v(19.75, 75.9) * mm]});
            skFitSpline(sketch, "E636", {"points": [v(19.75, 75.9) * mm, v(20.03, 75.24) * mm, v(16.54, 74.03) * mm, v(16.25, 72.4) * mm]});
            skFitSpline(sketch, "E637", {"points": [v(16.25, 72.4) * mm, v(15.3, 67.16) * mm, v(16.76, 56.92) * mm, v(16.25, 56.4) * mm]});
            skFitSpline(sketch, "E638", {"points": [v(16.25, 56.4) * mm, v(15.74, 55.9) * mm, v(13.26, 56.92) * mm, v(12.75, 56.4) * mm]});
            skFitSpline(sketch, "E639", {"points": [v(12.75, 56.4) * mm, v(12.24, 55.9) * mm, v(12.24, 53.92) * mm, v(12.75, 53.4) * mm]});
            skFitSpline(sketch, "E640", {"points": [v(12.75, 53.4) * mm, v(13.26, 52.9) * mm, v(18.74, 52.9) * mm, v(19.25, 53.4) * mm]});
            skFitSpline(sketch, "E641", {"points": [v(19.25, 53.4) * mm, v(19.76, 53.92) * mm, v(18.3, 64.16) * mm, v(19.25, 69.4) * mm]});
            skFitSpline(sketch, "E642", {"points": [v(19.25, 69.4) * mm, v(19.54, 71.03) * mm, v(22.2, 71.35) * mm, v(22.75, 72.9) * mm]});
            skFitSpline(sketch, "E643", {"points": [v(22.75, 72.9) * mm, v(23.47, 74.95) * mm, v(22.1, 77.34) * mm, v(22.75, 79.4) * mm]});
            skFitSpline(sketch, "E644", {"points": [v(22.75, 79.4) * mm, v(23.18, 80.76) * mm, v(24.34, 82.3) * mm, v(25.75, 82.4) * mm]});
            skFitSpline(sketch, "E645", {"points": [v(25.75, 82.4) * mm, v(38.88, 83.34) * mm, v(64.74, 82.92) * mm, v(65.25, 82.4) * mm]});
            skFitSpline(sketch, "E646", {"points": [v(65.25, 82.4) * mm, v(65.76, 81.9) * mm, v(65.76, 79.92) * mm, v(65.25, 79.4) * mm]});
            skFitSpline(sketch, "E647", {"points": [v(65.25, 79.4) * mm, v(64.74, 78.9) * mm, v(41.54, 80.47) * mm, v(29.75, 79.4) * mm]});
            skFitSpline(sketch, "E648", {"points": [v(29.75, 79.4) * mm, v(28.1, 79.26) * mm, v(26.8, 77.47) * mm, v(26.25, 75.9) * mm]});
            skFitSpline(sketch, "E649", {"points": [v(26.25, 75.9) * mm, v(25.53, 73.86) * mm, v(26.97, 71.45) * mm, v(26.25, 69.4) * mm]});
            skFitSpline(sketch, "E650", {"points": [v(26.25, 69.4) * mm, v(25.7, 67.85) * mm, v(23.53, 67.36) * mm, v(22.75, 65.9) * mm]});
            skFitSpline(sketch, "E651", {"points": [v(22.75, 65.9) * mm, v(22.28, 65.03) * mm, v(22.24, 63.42) * mm, v(22.75, 62.9) * mm]});
            skFitSpline(sketch, "E652", {"points": [v(22.75, 62.9) * mm, v(23.26, 62.4) * mm, v(28.74, 62.4) * mm, v(29.25, 62.9) * mm]});
            skFitSpline(sketch, "E653", {"points": [v(29.25, 62.9) * mm, v(29.76, 63.42) * mm, v(28.5, 69.66) * mm, v(29.25, 72.9) * mm]});
            skFitSpline(sketch, "E654", {"points": [v(29.25, 72.9) * mm, v(29.57, 74.29) * mm, v(30.86, 75.66) * mm, v(32.25, 75.9) * mm]});
            skFitSpline(sketch, "E655", {"points": [v(32.25, 75.9) * mm, v(36.68, 76.71) * mm, v(41.32, 76.71) * mm, v(45.75, 75.9) * mm]});
            skFitSpline(sketch, "E656", {"points": [v(45.75, 75.9) * mm, v(47.14, 75.66) * mm, v(48.08, 72.63) * mm, v(48.75, 72.9) * mm]});
            skFitSpline(sketch, "E657", {"points": [v(48.75, 72.9) * mm, v(49.42, 73.19) * mm, v(48.24, 75.4) * mm, v(48.75, 75.9) * mm]});
            skFitSpline(sketch, "E658", {"points": [v(48.75, 75.9) * mm, v(49.26, 76.42) * mm, v(51.36, 76.67) * mm, v(52.25, 75.9) * mm]});
            skFitSpline(sketch, "E659", {"points": [v(52.25, 75.9) * mm, v(53, 75.26) * mm, v(51.54, 73.62) * mm, v(52.25, 72.9) * mm]});
            skFitSpline(sketch, "E660", {"points": [v(52.25, 72.9) * mm, v(52.96, 72.2) * mm, v(54.74, 72.4) * mm, v(55.25, 72.9) * mm]});
            skFitSpline(sketch, "E661", {"points": [v(55.25, 72.9) * mm, v(55.76, 73.42) * mm, v(54.74, 75.4) * mm, v(55.25, 75.9) * mm]});
            skFitSpline(sketch, "E662", {"points": [v(55.25, 75.9) * mm, v(55.76, 76.42) * mm, v(57.86, 76.67) * mm, v(58.75, 75.9) * mm]});
            skFitSpline(sketch, "E663", {"points": [v(58.75, 75.9) * mm, v(59.5, 75.26) * mm, v(58.04, 73.62) * mm, v(58.75, 72.9) * mm]});
            skFitSpline(sketch, "E664", {"points": [v(58.75, 72.9) * mm, v(59.46, 72.2) * mm, v(61.24, 72.4) * mm, v(61.75, 72.9) * mm]});
            skFitSpline(sketch, "E665", {"points": [v(61.75, 72.9) * mm, v(62.26, 73.42) * mm, v(61.24, 75.4) * mm, v(61.75, 75.9) * mm]});
            skFitSpline(sketch, "E666", {"points": [v(61.75, 75.9) * mm, v(62.26, 76.42) * mm, v(64.36, 76.67) * mm, v(65.25, 75.9) * mm]});
            skFitSpline(sketch, "E667", {"points": [v(65.25, 75.9) * mm, v(66, 75.26) * mm, v(64.5, 73.56) * mm, v(65.25, 72.9) * mm]});
            skFitSpline(sketch, "E668", {"points": [v(65.25, 72.9) * mm, v(66.14, 72.15) * mm, v(68.24, 72.4) * mm, v(68.75, 72.9) * mm]});
            skFitSpline(sketch, "E669", {"points": [v(68.75, 72.9) * mm, v(69.26, 73.42) * mm, v(68.24, 81.9) * mm, v(68.75, 82.4) * mm]});
            skFitSpline(sketch, "E670", {"points": [v(68.75, 82.4) * mm, v(69.26, 82.92) * mm, v(71.24, 82.92) * mm, v(71.75, 82.4) * mm]});
            skFitSpline(sketch, "E671", {"points": [v(71.75, 82.4) * mm, v(72.26, 81.9) * mm, v(71.04, 80.12) * mm, v(71.75, 79.4) * mm]});
            skFitSpline(sketch, "E672", {"points": [v(71.75, 79.4) * mm, v(72.46, 78.7) * mm, v(74.24, 78.9) * mm, v(74.75, 79.4) * mm]});
            skFitSpline(sketch, "E673", {"points": [v(74.75, 79.4) * mm, v(75.26, 79.92) * mm, v(73.94, 81.82) * mm, v(74.75, 82.4) * mm]});
            skFitSpline(sketch, "E674", {"points": [v(74.75, 82.4) * mm, v(75.86, 83.22) * mm, v(77.85, 83.32) * mm, v(78.87, 82.4) * mm]});
            skFitSpline(sketch, "E675", {"points": [v(78.87, 82.4) * mm, v(79.65, 81.72) * mm, v(77.41, 80.15) * mm, v(78.12, 79.4) * mm]});
            skFitSpline(sketch, "E676", {"points": [v(78.12, 79.4) * mm, v(78.96, 78.54) * mm, v(81.24, 79.92) * mm, v(81.75, 79.4) * mm]});
            skFitSpline(sketch, "E677", {"points": [v(81.75, 79.4) * mm, v(82.26, 78.9) * mm, v(82.26, 73.42) * mm, v(81.75, 72.9) * mm]});
            skFitSpline(sketch, "E678", {"points": [v(81.75, 72.9) * mm, v(81.24, 72.4) * mm, v(79.63, 73.38) * mm, v(78.75, 72.9) * mm]});
            skFitSpline(sketch, "E679", {"points": [v(78.75, 72.9) * mm, v(77.3, 72.13) * mm, v(76.9, 69.58) * mm, v(75.25, 69.4) * mm]});
            skFitSpline(sketch, "E680", {"points": [v(75.25, 69.4) * mm, v(65.47, 68.37) * mm, v(55.53, 68.37) * mm, v(45.75, 69.4) * mm]});
            skFitSpline(sketch, "E681", {"points": [v(45.75, 69.4) * mm, v(44.1, 69.58) * mm, v(43.8, 72.34) * mm, v(42.25, 72.9) * mm]});
            skFitSpline(sketch, "E682", {"points": [v(42.25, 72.9) * mm, v(40.37, 73.6) * mm, v(38.13, 73.6) * mm, v(36.25, 72.9) * mm]});
            skFitSpline(sketch, "E683", {"points": [v(36.25, 72.9) * mm, v(34.7, 72.34) * mm, v(33.3, 70.97) * mm, v(32.75, 69.4) * mm]});
            skFitSpline(sketch, "E684", {"points": [v(32.75, 69.4) * mm, v(32.03, 67.36) * mm, v(32.24, 63.42) * mm, v(32.75, 62.9) * mm]});
            skFitSpline(sketch, "E685", {"points": [v(32.75, 62.9) * mm, v(33.26, 62.4) * mm, v(41.74, 63.42) * mm, v(42.25, 62.9) * mm]});
            skFitSpline(sketch, "E686", {"points": [v(42.25, 62.9) * mm, v(42.76, 62.4) * mm, v(42.76, 60.42) * mm, v(42.25, 59.9) * mm]});
            skFitSpline(sketch, "E687", {"points": [v(42.25, 59.9) * mm, v(41.74, 59.4) * mm, v(23.26, 60.42) * mm, v(22.75, 59.9) * mm]});
            skFitSpline(sketch, "E688", {"points": [v(22.75, 59.9) * mm, v(22.24, 59.4) * mm, v(22.24, 53.92) * mm, v(22.75, 53.4) * mm]});
            skFitSpline(sketch, "E689", {"points": [v(22.75, 53.4) * mm, v(23.26, 52.9) * mm, v(25.42, 54.23) * mm, v(26.25, 53.4) * mm]});
            skFitSpline(sketch, "E690", {"points": [v(26.25, 53.4) * mm, v(27.07, 52.58) * mm, v(26.76, 50.42) * mm, v(26.25, 49.9) * mm]});
            skFitSpline(sketch, "E691", {"points": [v(26.25, 49.9) * mm, v(25.74, 49.4) * mm, v(21.8, 50.62) * mm, v(19.75, 49.9) * mm]});
            skFitSpline(sketch, "E692", {"points": [v(19.75, 49.9) * mm, v(18.2, 49.36) * mm, v(16.82, 47.96) * mm, v(16.25, 46.4) * mm]});
            skFitSpline(sketch, "E693", {"points": [v(16.25, 46.4) * mm, v(15.56, 44.53) * mm, v(16.94, 42.29) * mm, v(16.25, 40.4) * mm]});
            skFitSpline(sketch, "E694", {"points": [v(16.25, 40.4) * mm, v(15.68, 38.86) * mm, v(13.3, 38.47) * mm, v(12.75, 36.9) * mm]});
            skFitSpline(sketch, "E695", {"points": [v(12.75, 36.9) * mm, v(12.03, 34.86) * mm, v(12.24, 30.92) * mm, v(12.75, 30.4) * mm]});
            skFitSpline(sketch, "E696", {"points": [v(12.75, 30.4) * mm, v(13.26, 29.9) * mm, v(14.87, 29.93) * mm, v(15.75, 30.4) * mm]});
            skFitSpline(sketch, "E697", {"points": [v(15.75, 30.4) * mm, v(17.2, 31.2) * mm, v(18.7, 32.35) * mm, v(19.25, 33.9) * mm]});
            skFitSpline(sketch, "E698", {"points": [v(19.25, 33.9) * mm, v(19.97, 35.95) * mm, v(18.74, 39.9) * mm, v(19.25, 40.4) * mm]});
            skFitSpline(sketch, "E699", {"points": [v(19.25, 40.4) * mm, v(19.76, 40.92) * mm, v(28.74, 39.9) * mm, v(29.25, 40.4) * mm]});
            skFitSpline(sketch, "E700", {"points": [v(29.25, 40.4) * mm, v(29.76, 40.92) * mm, v(28.74, 52.9) * mm, v(29.25, 53.4) * mm]});
            skFitSpline(sketch, "E701", {"points": [v(29.25, 53.4) * mm, v(29.76, 53.92) * mm, v(32.24, 53.92) * mm, v(32.75, 53.4) * mm]});
            skFitSpline(sketch, "E702", {"points": [v(32.75, 53.4) * mm, v(33.26, 52.9) * mm, v(32.06, 47.02) * mm, v(32.75, 46.78) * mm]});
            skFitSpline(sketch, "E703", {"points": [v(32.75, 46.78) * mm, v(33.44, 46.54) * mm, v(34.05, 49.33) * mm, v(35.25, 49.9) * mm]});
            skFitSpline(sketch, "E704", {"points": [v(35.25, 49.9) * mm, v(36.45, 50.49) * mm, v(38.74, 50.42) * mm, v(39.25, 49.9) * mm]});
            skFitSpline(sketch, "E705", {"points": [v(39.25, 49.9) * mm, v(39.76, 49.4) * mm, v(39.72, 47.79) * mm, v(39.25, 46.9) * mm]});
            skFitSpline(sketch, "E706", {"points": [v(39.25, 46.9) * mm, v(38.47, 45.46) * mm, v(37.2, 44.2) * mm, v(35.75, 43.4) * mm]});
            skFitSpline(sketch, "E707", {"points": [v(35.75, 43.4) * mm, v(34.87, 42.93) * mm, v(33.26, 43.92) * mm, v(32.75, 43.4) * mm]});
            skFitSpline(sketch, "E708", {"points": [v(32.75, 43.4) * mm, v(32.24, 42.9) * mm, v(32.24, 40.92) * mm, v(32.75, 40.4) * mm]});
            skFitSpline(sketch, "E709", {"points": [v(32.75, 40.4) * mm, v(33.26, 39.9) * mm, v(45.24, 39.9) * mm, v(45.75, 40.4) * mm]});
            skFitSpline(sketch, "E710", {"points": [v(45.75, 40.4) * mm, v(46.26, 40.92) * mm, v(46.26, 49.4) * mm, v(45.75, 49.9) * mm]});
            skFitSpline(sketch, "E711", {"points": [v(45.75, 49.9) * mm, v(45.24, 50.42) * mm, v(43.07, 49.08) * mm, v(42.25, 49.9) * mm]});
            skFitSpline(sketch, "E712", {"points": [v(42.25, 49.9) * mm, v(41.42, 50.73) * mm, v(41.42, 52.58) * mm, v(42.25, 53.4) * mm]});
            skFitSpline(sketch, "E713", {"points": [v(42.25, 53.4) * mm, v(43.07, 54.23) * mm, v(45.24, 52.9) * mm, v(45.75, 53.4) * mm]});
            skFitSpline(sketch, "E714", {"points": [v(45.75, 53.4) * mm, v(46.26, 53.92) * mm, v(44.88, 60.2) * mm, v(45.75, 63.4) * mm]});
            skFitSpline(sketch, "E715", {"points": [v(45.75, 63.4) * mm, v(46.15, 64.9) * mm, v(47.85, 65.77) * mm, v(49.25, 66.4) * mm]});
            skFitSpline(sketch, "E716", {"points": [v(49.25, 66.4) * mm, v(50.16, 66.83) * mm, v(51.74, 66.92) * mm, v(52.25, 66.4) * mm]});
            skFitSpline(sketch, "E717", {"points": [v(52.25, 66.4) * mm, v(52.76, 65.9) * mm, v(52.74, 63.97) * mm, v(52.25, 62.9) * mm]});
            skFitSpline(sketch, "E718", {"points": [v(52.25, 62.9) * mm, v(51.66, 61.62) * mm, v(48.97, 60.58) * mm, v(49.25, 59.9) * mm]});
            skFitSpline(sketch, "E719", {"points": [v(49.25, 59.9) * mm, v(49.53, 59.24) * mm, v(58.24, 59.4) * mm, v(58.75, 59.9) * mm]});
            skFitSpline(sketch, "E720", {"points": [v(58.75, 59.9) * mm, v(59.26, 60.42) * mm, v(58.26, 62.35) * mm, v(58.75, 63.4) * mm]});
            skFitSpline(sketch, "E721", {"points": [v(58.75, 63.4) * mm, v(59.34, 64.7) * mm, v(61.08, 66.69) * mm, v(61.75, 66.4) * mm]});
            skFitSpline(sketch, "E722", {"points": [v(61.75, 66.4) * mm, v(62.42, 66.13) * mm, v(61.24, 63.42) * mm, v(61.75, 62.9) * mm]});
            skFitSpline(sketch, "E723", {"points": [v(61.75, 62.9) * mm, v(62.26, 62.4) * mm, v(64.2, 62.39) * mm, v(65.25, 62.9) * mm]});
            skFitSpline(sketch, "E724", {"points": [v(65.25, 62.9) * mm, v(66.73, 63.65) * mm, v(67.14, 66.07) * mm, v(68.75, 66.4) * mm]});
            skFitSpline(sketch, "E725", {"points": [v(68.75, 66.4) * mm, v(72.99, 67.3) * mm, v(81.24, 66.92) * mm, v(81.75, 66.4) * mm]});
            skFitSpline(sketch, "E726", {"points": [v(81.75, 66.4) * mm, v(82.26, 65.9) * mm, v(82.26, 63.42) * mm, v(81.75, 62.9) * mm]});
            skFitSpline(sketch, "E727", {"points": [v(81.75, 62.9) * mm, v(81.24, 62.4) * mm, v(72.86, 64.28) * mm, v(68.75, 62.9) * mm]});
            skFitSpline(sketch, "E728", {"points": [v(68.75, 62.9) * mm, v(65.84, 61.94) * mm, v(65.16, 57.35) * mm, v(62.25, 56.4) * mm]});
            skFitSpline(sketch, "E729", {"points": [v(62.25, 56.4) * mm, v(57.96, 55.02) * mm, v(49.22, 56.94) * mm, v(48.72, 56.4) * mm]});
            skFitSpline(sketch, "E730", {"points": [v(48.72, 56.4) * mm, v(48.22, 55.88) * mm, v(48.68, 47.15) * mm, v(49.29, 46.75) * mm]});
            skFitSpline(sketch, "E731", {"points": [v(49.29, 46.75) * mm, v(49.9, 46.34) * mm, v(58.16, 50.5) * mm, v(58.75, 50.09) * mm]});
            skFitSpline(sketch, "E732", {"points": [v(58.75, 50.09) * mm, v(59.34, 49.67) * mm, v(59.25, 47.53) * mm, v(58.75, 46.4) * mm]});
            skFitSpline(sketch, "E733", {"points": [v(58.75, 46.4) * mm, v(58.17, 45.12) * mm, v(57.1, 43.82) * mm, v(55.75, 43.4) * mm]});
            skFitSpline(sketch, "E734", {"points": [v(55.75, 43.4) * mm, v(53.51, 42.74) * mm, v(49.26, 43.92) * mm, v(48.75, 43.4) * mm]});
            skFitSpline(sketch, "E735", {"points": [v(48.75, 43.4) * mm, v(48.24, 42.9) * mm, v(48.24, 40.92) * mm, v(48.75, 40.4) * mm]});
            skFitSpline(sketch, "E736", {"points": [v(48.75, 40.4) * mm, v(49.26, 39.9) * mm, v(57.82, 39.6) * mm, v(62.25, 40.4) * mm]});
            skFitSpline(sketch, "E737", {"points": [v(62.25, 40.4) * mm, v(63.64, 40.66) * mm, v(64.93, 42.03) * mm, v(65.25, 43.4) * mm]});
            skFitSpline(sketch, "E738", {"points": [v(65.25, 43.4) * mm, v(66, 46.66) * mm, v(64.41, 50.18) * mm, v(65.25, 53.4) * mm]});
            skFitSpline(sketch, "E739", {"points": [v(65.25, 53.4) * mm, v(65.66, 55) * mm, v(68.08, 57.19) * mm, v(68.75, 56.9) * mm]});
            skFitSpline(sketch, "E740", {"points": [v(68.75, 56.9) * mm, v(69.42, 56.63) * mm, v(68, 54.3) * mm, v(68.75, 53.4) * mm]});
            skFitSpline(sketch, "E741", {"points": [v(68.75, 53.4) * mm, v(69.4, 52.65) * mm, v(71.24, 52.9) * mm, v(71.75, 53.4) * mm]});
            skFitSpline(sketch, "E742", {"points": [v(71.75, 53.4) * mm, v(72.26, 53.92) * mm, v(71.24, 59.4) * mm, v(71.75, 59.9) * mm]});
            skFitSpline(sketch, "E743", {"points": [v(71.75, 59.9) * mm, v(72.26, 60.42) * mm, v(74.58, 60.83) * mm, v(75.35, 59.9) * mm]});
            skFitSpline(sketch, "E744", {"points": [v(75.35, 59.9) * mm, v(76.1, 59) * mm, v(74.19, 56.97) * mm, v(74.65, 56.4) * mm]});
            skFitSpline(sketch, "E745", {"points": [v(74.65, 56.4) * mm, v(75.11, 55.85) * mm, v(79.17, 55.69) * mm, v(81.25, 56.4) * mm]});
            skFitSpline(sketch, "E746", {"points": [v(81.25, 56.4) * mm, v(82.8, 56.95) * mm, v(83.97, 58.46) * mm, v(84.75, 59.9) * mm]});
            skFitSpline(sketch, "E747", {"points": [v(84.75, 59.9) * mm, v(85.22, 60.79) * mm, v(84.19, 62.08) * mm, v(84.75, 62.9) * mm]});
            skFitSpline(sketch, "E748", {"points": [v(84.75, 62.9) * mm, v(86.48, 65.44) * mm, v(90.13, 66.56) * mm, v(91.25, 69.4) * mm]});
            skFitSpline(sketch, "E749", {"points": [v(91.25, 69.4) * mm, v(92.48, 72.54) * mm, v(90.38, 76.25) * mm, v(91.25, 79.5) * mm]});
            skFitSpline(sketch, "E750", {"points": [v(91.25, 79.5) * mm, v(91.64, 80.96) * mm, v(93.23, 82.3) * mm, v(94.75, 82.4) * mm]});
            skFitSpline(sketch, "E751", {"points": [v(94.75, 82.4) * mm, v(107.89, 83.3) * mm, v(121.12, 83.34) * mm, v(134.25, 82.4) * mm]});
            skFitSpline(sketch, "E752", {"points": [v(134.25, 82.4) * mm, v(135.66, 82.3) * mm, v(136.82, 80.76) * mm, v(137.25, 79.4) * mm]});
            skFitSpline(sketch, "E753", {"points": [v(137.25, 79.4) * mm, v(137.9, 77.34) * mm, v(137.76, 73.42) * mm, v(137.25, 72.9) * mm]});
            skFitSpline(sketch, "E754", {"points": [v(137.25, 72.9) * mm, v(136.74, 72.4) * mm, v(134.26, 72.4) * mm, v(133.75, 72.9) * mm]});
            skFitSpline(sketch, "E755", {"points": [v(133.75, 72.9) * mm, v(133.24, 73.42) * mm, v(134.22, 75.03) * mm, v(133.75, 75.9) * mm]});
            skFitSpline(sketch, "E756", {"points": [v(133.75, 75.9) * mm, v(132.97, 77.36) * mm, v(131.73, 78.67) * mm, v(130.25, 79.4) * mm]});
            skFitSpline(sketch, "E757", {"points": [v(130.25, 79.4) * mm, v(129.2, 79.93) * mm, v(127.26, 79.92) * mm, v(126.75, 79.4) * mm]});
            skFitSpline(sketch, "E758", {"points": [v(126.75, 79.4) * mm, v(126.24, 78.9) * mm, v(126.03, 77.14) * mm, v(126.75, 76.5) * mm]});
            skFitSpline(sketch, "E759", {"points": [v(126.75, 76.5) * mm, v(127.76, 75.6) * mm, v(130.09, 77) * mm, v(130.75, 75.83) * mm]});
            skFitSpline(sketch, "E760", {"points": [v(130.75, 75.83) * mm, v(131.8, 73.96) * mm, v(130.24, 69.92) * mm, v(130.75, 69.4) * mm]});
            skFitSpline(sketch, "E761", {"points": [v(130.75, 69.4) * mm, v(131.26, 68.9) * mm, v(140.24, 68.9) * mm, v(140.75, 69.4) * mm]});
            skFitSpline(sketch, "E762", {"points": [v(140.75, 69.4) * mm, v(141.26, 69.92) * mm, v(140.24, 78.9) * mm, v(140.75, 79.4) * mm]});
            skFitSpline(sketch, "E763", {"points": [v(140.75, 79.4) * mm, v(141.26, 79.92) * mm, v(143.24, 79.92) * mm, v(143.75, 79.4) * mm]});
            skFitSpline(sketch, "E764", {"points": [v(143.75, 79.4) * mm, v(144.26, 78.9) * mm, v(143.1, 74.98) * mm, v(143.75, 72.9) * mm]});
            skFitSpline(sketch, "E765", {"points": [v(143.75, 72.9) * mm, v(144.18, 71.56) * mm, v(145.75, 70.9) * mm, v(146.75, 69.9) * mm]});
            skFitSpline(sketch, "E766", {"points": [v(143.75, 72.9) * mm, v(144.75, 71.9) * mm, v(145.75, 70.9) * mm, v(146.75, 69.9) * mm]});
            skFitSpline(sketch, "E767", {"points": [v(146.75, 69.9) * mm, v(146.94, 68.6) * mm, v(147.26, 66.42) * mm, v(146.75, 65.9) * mm]});
            skFitSpline(sketch, "E768", {"points": [v(146.75, 65.9) * mm, v(146.24, 65.4) * mm, v(131.26, 66.42) * mm, v(130.75, 65.9) * mm]});
            skFitSpline(sketch, "E769", {"points": [v(130.75, 65.9) * mm, v(130.24, 65.4) * mm, v(131.26, 63.42) * mm, v(130.75, 62.9) * mm]});
            skFitSpline(sketch, "E770", {"points": [v(130.75, 62.9) * mm, v(130.24, 62.4) * mm, v(128.14, 62.15) * mm, v(127.25, 62.9) * mm]});
            skFitSpline(sketch, "E771", {"points": [v(127.25, 62.9) * mm, v(126.5, 63.56) * mm, v(127.76, 65.4) * mm, v(127.25, 65.9) * mm]});
            skFitSpline(sketch, "E772", {"points": [v(127.25, 65.9) * mm, v(126.74, 66.42) * mm, v(105.53, 66.96) * mm, v(94.75, 65.9) * mm]});
            skFitSpline(sketch, "E773", {"points": [v(94.75, 65.9) * mm, v(93.1, 65.75) * mm, v(91.99, 63.88) * mm, v(91.25, 62.4) * mm]});
            skFitSpline(sketch, "E774", {"points": [v(91.25, 62.4) * mm, v(90.87, 61.65) * mm, v(92.26, 60.59) * mm, v(91.75, 59.9) * mm]});
            skFitSpline(sketch, "E775", {"points": [v(91.75, 59.9) * mm, v(88.9, 56.16) * mm, v(85.78, 52.35) * mm, v(81.75, 49.9) * mm]});
            skFitSpline(sketch, "E776", {"points": [v(81.75, 49.9) * mm, v(79.9, 48.79) * mm, v(77.19, 50.88) * mm, v(75.25, 49.9) * mm]});
            skFitSpline(sketch, "E777", {"points": [v(75.25, 49.9) * mm, v(72.5, 48.54) * mm, v(70.48, 45.94) * mm, v(68.75, 43.4) * mm]});
            skFitSpline(sketch, "E778", {"points": [v(68.75, 43.4) * mm, v(68.19, 42.58) * mm, v(68.24, 40.92) * mm, v(68.75, 40.4) * mm]});
            skFitSpline(sketch, "E779", {"points": [v(68.75, 40.4) * mm, v(69.26, 39.9) * mm, v(74.74, 40.92) * mm, v(75.25, 40.4) * mm]});
            skFitSpline(sketch, "E780", {"points": [v(75.25, 40.4) * mm, v(75.76, 39.9) * mm, v(75.76, 37.42) * mm, v(75.25, 36.9) * mm]});
            skFitSpline(sketch, "E781", {"points": [v(75.25, 36.9) * mm, v(74.74, 36.4) * mm, v(68.5, 37.66) * mm, v(65.25, 36.9) * mm]});
            skFitSpline(sketch, "E782", {"points": [v(65.25, 36.9) * mm, v(63.87, 36.6) * mm, v(63.53, 34.5) * mm, v(62.25, 33.9) * mm]});
            skFitSpline(sketch, "E783", {"points": [v(62.25, 33.9) * mm, v(61.2, 33.42) * mm, v(59.57, 34.73) * mm, v(58.75, 33.9) * mm]});
            skFitSpline(sketch, "E784", {"points": [v(58.75, 33.9) * mm, v(57.92, 33.08) * mm, v(57.92, 31.23) * mm, v(58.75, 30.4) * mm]});
            skFitSpline(sketch, "E785", {"points": [v(58.75, 30.4) * mm, v(59.57, 29.58) * mm, v(61.42, 31.23) * mm, v(62.25, 30.4) * mm]});
            skFitSpline(sketch, "E786", {"points": [v(62.25, 30.4) * mm, v(63.07, 29.58) * mm, v(62.76, 27.42) * mm, v(62.25, 26.9) * mm]});
            skFitSpline(sketch, "E787", {"points": [v(62.25, 26.9) * mm, v(61.74, 26.4) * mm, v(49.76, 27.42) * mm, v(49.25, 26.9) * mm]});
            skFitSpline(sketch, "E788", {"points": [v(49.25, 26.9) * mm, v(48.74, 26.4) * mm, v(50.5, 22.47) * mm, v(49.25, 20.9) * mm]});
            skFitSpline(sketch, "E789", {"points": [v(49.25, 20.9) * mm, v(46.77, 17.8) * mm, v(41.31, 17.8) * mm, v(39.25, 14.4) * mm]});
            skFitSpline(sketch, "E790", {"points": [v(39.25, 14.4) * mm, v(37.52, 11.56) * mm, v(38.74, 4.92) * mm, v(39.25, 4.4) * mm]});
            skFitSpline(sketch, "E791", {"points": [v(39.25, 4.4) * mm, v(39.76, 3.9) * mm, v(41.37, 3.93) * mm, v(42.25, 4.4) * mm]});
            skFitSpline(sketch, "E792", {"points": [v(42.25, 4.4) * mm, v(43.7, 5.2) * mm, v(45.01, 6.43) * mm, v(45.75, 7.9) * mm]});
            skFitSpline(sketch, "E793", {"points": [v(45.75, 7.9) * mm, v(46.27, 8.95) * mm, v(45.26, 10.35) * mm, v(45.75, 11.4) * mm]});
            skFitSpline(sketch, "E794", {"points": [v(45.75, 11.4) * mm, v(46.34, 12.7) * mm, v(47.4, 13.96) * mm, v(48.75, 14.4) * mm]});
            skFitSpline(sketch, "E795", {"points": [v(48.75, 14.4) * mm, v(49.42, 14.63) * mm, v(49.54, 12.9) * mm, v(50.25, 12.9) * mm]});
            skFitSpline(sketch, "E796", {"points": [v(50.25, 12.9) * mm, v(51.08, 12.9) * mm, v(52.05, 13.6) * mm, v(52.25, 14.4) * mm]});
            skFitSpline(sketch, "E797", {"points": [v(52.25, 14.4) * mm, v(52.78, 16.51) * mm, v(51.6, 18.84) * mm, v(52.25, 20.9) * mm]});
            skFitSpline(sketch, "E798", {"points": [v(52.25, 20.9) * mm, v(52.68, 22.26) * mm, v(53.87, 23.6) * mm, v(55.25, 23.9) * mm]});
            skFitSpline(sketch, "E799", {"points": [v(55.25, 23.9) * mm, v(58.5, 24.66) * mm, v(64.74, 24.42) * mm, v(65.25, 23.9) * mm]});
            skFitSpline(sketch, "E800", {"points": [v(65.25, 23.9) * mm, v(65.76, 23.4) * mm, v(65.76, 21.42) * mm, v(65.25, 20.9) * mm]});
            skFitSpline(sketch, "E801", {"points": [v(65.25, 20.9) * mm, v(64.74, 20.4) * mm, v(61.1, 21.65) * mm, v(59.25, 20.9) * mm]});
            skFitSpline(sketch, "E802", {"points": [v(59.25, 20.9) * mm, v(57.5, 20.2) * mm, v(56.24, 18.51) * mm, v(55.25, 16.9) * mm]});
            skFitSpline(sketch, "E803", {"points": [v(55.25, 16.9) * mm, v(54.81, 16.2) * mm, v(54.79, 15.1) * mm, v(55.25, 14.4) * mm]});
            skFitSpline(sketch, "E804", {"points": [v(55.25, 14.4) * mm, v(56.23, 12.93) * mm, v(57.58, 11.5) * mm, v(59.25, 10.9) * mm]});
            skFitSpline(sketch, "E805", {"points": [v(59.25, 10.9) * mm, v(61.14, 10.25) * mm, v(64.74, 11.42) * mm, v(65.25, 10.9) * mm]});
            skFitSpline(sketch, "E806", {"points": [v(65.25, 10.9) * mm, v(65.76, 10.4) * mm, v(65.72, 8.79) * mm, v(65.25, 7.9) * mm]});
            skFitSpline(sketch, "E807", {"points": [v(65.25, 7.9) * mm, v(64.47, 6.46) * mm, v(63.2, 5.2) * mm, v(61.75, 4.4) * mm]});
            skFitSpline(sketch, "E808", {"points": [v(61.75, 4.4) * mm, v(60.87, 3.93) * mm, v(59.26, 3.9) * mm, v(58.75, 4.4) * mm]});
            skFitSpline(sketch, "E809", {"points": [v(58.75, 4.4) * mm, v(58.24, 4.92) * mm, v(59.26, 6.9) * mm, v(58.75, 7.4) * mm]});
            skFitSpline(sketch, "E810", {"points": [v(58.75, 7.4) * mm, v(58.24, 7.92) * mm, v(51.85, 8.63) * mm, v(48.75, 7.4) * mm]});
            skFitSpline(sketch, "E811", {"points": [v(48.75, 7.4) * mm, v(45.9, 6.29) * mm, v(44.04, 3.4) * mm, v(42.25, 0.9) * mm]});
            skFitSpline(sketch, "E812", {"points": [v(42.25, 0.9) * mm, v(41.76, 0.23) * mm, v(41.74, -1.08) * mm, v(42.25, -1.6) * mm]});
            skFitSpline(sketch, "E813", {"points": [v(42.25, -1.6) * mm, v(42.76, -2.1) * mm, v(62.47, -0.92) * mm, v(62.75, -1.6) * mm]});
            skFitSpline(sketch, "E814", {"points": [v(62.75, -1.6) * mm, v(63.03, -2.26) * mm, v(60.82, -4.57) * mm, v(59.25, -5.1) * mm]});
            skFitSpline(sketch, "E815", {"points": [v(59.25, -5.1) * mm, v(57.04, -5.83) * mm, v(54.46, -4.35) * mm, v(52.25, -5.1) * mm]});
            skFitSpline(sketch, "E816", {"points": [v(52.25, -5.1) * mm, v(50.68, -5.61) * mm, v(50.2, -7.8) * mm, v(48.75, -8.6) * mm]});
            skFitSpline(sketch, "E817", {"points": [v(48.75, -8.6) * mm, v(47.87, -9.06) * mm, v(46.26, -9.1) * mm, v(45.75, -8.6) * mm]});
            skFitSpline(sketch, "E818", {"points": [v(45.75, -8.6) * mm, v(45.24, -8.08) * mm, v(46.26, -5.6) * mm, v(45.75, -5.1) * mm]});
            skFitSpline(sketch, "E819", {"points": [v(45.75, -5.1) * mm, v(45.24, -4.58) * mm, v(41.3, -4.38) * mm, v(39.25, -5.1) * mm]});
            skFitSpline(sketch, "E820", {"points": [v(39.25, -5.1) * mm, v(37.7, -5.64) * mm, v(35.96, -6.95) * mm, v(35.75, -8.6) * mm]});
            skFitSpline(sketch, "E821", {"points": [v(35.75, -8.6) * mm, v(34.91, -15.04) * mm, v(35.66, -27.5) * mm, v(36.26, -28.1) * mm]});
            skFitSpline(sketch, "E822", {"points": [v(36.26, -28.1) * mm, v(36.87, -28.68) * mm, v(38.74, -28.6) * mm, v(39.25, -28.1) * mm]});
            skFitSpline(sketch, "E823", {"points": [v(39.25, -28.1) * mm, v(39.76, -27.58) * mm, v(38.74, -15.6) * mm, v(39.25, -15.1) * mm]});
            skFitSpline(sketch, "E824", {"points": [v(39.25, -15.1) * mm, v(39.76, -14.58) * mm, v(41.74, -14.58) * mm, v(42.25, -15.1) * mm]});
            skFitSpline(sketch, "E825", {"points": [v(42.25, -15.1) * mm, v(42.76, -15.6) * mm, v(41.74, -24.08) * mm, v(42.25, -24.6) * mm]});
            skFitSpline(sketch, "E826", {"points": [v(42.25, -24.6) * mm, v(42.76, -25.1) * mm, v(46.7, -25.3) * mm, v(48.75, -24.6) * mm]});
            skFitSpline(sketch, "E827", {"points": [v(48.75, -24.6) * mm, v(50.3, -24.05) * mm, v(51.82, -22.68) * mm, v(52.25, -21.1) * mm]});
            skFitSpline(sketch, "E828", {"points": [v(52.25, -21.1) * mm, v(53.07, -18.03) * mm, v(51.51, -14.67) * mm, v(52.25, -11.6) * mm]});
            skFitSpline(sketch, "E829", {"points": [v(52.25, -11.6) * mm, v(52.58, -10.22) * mm, v(53.9, -9.02) * mm, v(55.25, -8.6) * mm]});
            skFitSpline(sketch, "E830", {"points": [v(55.25, -8.6) * mm, v(57.32, -7.94) * mm, v(59.7, -9.3) * mm, v(61.75, -8.6) * mm]});
            skFitSpline(sketch, "E831", {"points": [v(61.75, -8.6) * mm, v(63.3, -8.05) * mm, v(64.51, -6.57) * mm, v(65.25, -5.1) * mm]});
            skFitSpline(sketch, "E832", {"points": [v(65.25, -5.1) * mm, v(65.77, -4.05) * mm, v(64.73, -2.63) * mm, v(65.25, -1.6) * mm]});
            skFitSpline(sketch, "E833", {"points": [v(65.25, -1.6) * mm, v(65.99, -0.12) * mm, v(68.53, 0.27) * mm, v(68.75, 1.9) * mm]});
            skFitSpline(sketch, "E834", {"points": [v(68.75, 1.9) * mm, v(69.75, 9.17) * mm, v(68.24, 23.4) * mm, v(68.75, 23.9) * mm]});
            skFitSpline(sketch, "E835", {"points": [v(68.75, 23.9) * mm, v(69.26, 24.42) * mm, v(70.73, 24.48) * mm, v(71.4, 23.9) * mm]});
            skFitSpline(sketch, "E836", {"points": [v(71.4, 23.9) * mm, v(73.1, 22.46) * mm, v(75.38, 19.94) * mm, v(75.25, 18.4) * mm]});
            skFitSpline(sketch, "E837", {"points": [v(75.25, 18.4) * mm, v(75.12, 16.88) * mm, v(72.45, 16.4) * mm, v(71.75, 14.9) * mm]});
            skFitSpline(sketch, "E838", {"points": [v(71.75, 14.9) * mm, v(71.19, 13.7) * mm, v(71.24, 11.42) * mm, v(71.75, 10.9) * mm]});
            skFitSpline(sketch, "E839", {"points": [v(71.75, 10.9) * mm, v(72.26, 10.4) * mm, v(73.87, 10.43) * mm, v(74.75, 10.9) * mm]});
            skFitSpline(sketch, "E840", {"points": [v(74.75, 10.9) * mm, v(76.2, 11.7) * mm, v(77.47, 12.96) * mm, v(78.25, 14.4) * mm]});
            skFitSpline(sketch, "E841", {"points": [v(78.25, 14.4) * mm, v(78.72, 15.29) * mm, v(77.78, 16.53) * mm, v(78.25, 17.4) * mm]});
            skFitSpline(sketch, "E842", {"points": [v(78.25, 17.4) * mm, v(79.03, 18.86) * mm, v(81.18, 19.36) * mm, v(81.75, 20.9) * mm]});
            skFitSpline(sketch, "E843", {"points": [v(81.75, 20.9) * mm, v(82.44, 22.79) * mm, v(82.26, 26.4) * mm, v(81.75, 26.9) * mm]});
            skFitSpline(sketch, "E844", {"points": [v(81.75, 26.9) * mm, v(81.24, 27.42) * mm, v(79.07, 26.08) * mm, v(78.25, 26.9) * mm]});
            skFitSpline(sketch, "E845", {"points": [v(78.25, 26.9) * mm, v(77.42, 27.73) * mm, v(77.74, 29.9) * mm, v(78.25, 30.4) * mm]});
            skFitSpline(sketch, "E846", {"points": [v(78.25, 30.4) * mm, v(78.76, 30.92) * mm, v(80.46, 29.8) * mm, v(81.25, 30.4) * mm]});
            skFitSpline(sketch, "E847", {"points": [v(81.25, 30.4) * mm, v(84.99, 33.28) * mm, v(88.8, 36.38) * mm, v(91.25, 40.4) * mm]});
            skFitSpline(sketch, "E848", {"points": [v(91.25, 40.4) * mm, v(92.37, 42.26) * mm, v(90.74, 46.4) * mm, v(91.25, 46.9) * mm]});
            skFitSpline(sketch, "E849", {"points": [v(91.25, 46.9) * mm, v(91.76, 47.42) * mm, v(94.24, 47.42) * mm, v(94.75, 46.9) * mm]});
            skFitSpline(sketch, "E850", {"points": [v(94.75, 46.9) * mm, v(95.26, 46.4) * mm, v(94.24, 40.92) * mm, v(94.75, 40.4) * mm]});
            skFitSpline(sketch, "E851", {"points": [v(94.75, 40.4) * mm, v(95.26, 39.9) * mm, v(100.74, 39.9) * mm, v(101.25, 40.4) * mm]});
            skFitSpline(sketch, "E852", {"points": [v(101.25, 40.4) * mm, v(101.76, 40.92) * mm, v(101.82, 44.5) * mm, v(101.25, 46.4) * mm]});
            skFitSpline(sketch, "E853", {"points": [v(101.25, 46.4) * mm, v(100.77, 48) * mm, v(98.15, 49.03) * mm, v(98.25, 50.4) * mm]});
            skFitSpline(sketch, "E854", {"points": [v(98.25, 50.4) * mm, v(98.35, 51.79) * mm, v(103.62, 58.17) * mm, v(107.75, 59.9) * mm]});
            skFitSpline(sketch, "E855", {"points": [v(107.75, 59.9) * mm, v(111.74, 61.6) * mm, v(120.24, 60.42) * mm, v(120.75, 59.9) * mm]});
            skFitSpline(sketch, "E856", {"points": [v(120.75, 59.9) * mm, v(121.26, 59.4) * mm, v(120.24, 56.92) * mm, v(120.75, 56.4) * mm]});
            skFitSpline(sketch, "E857", {"points": [v(120.75, 56.4) * mm, v(121.26, 55.9) * mm, v(140.24, 55.9) * mm, v(140.75, 56.4) * mm]});
            skFitSpline(sketch, "E858", {"points": [v(140.75, 56.4) * mm, v(141.26, 56.92) * mm, v(140.24, 59.4) * mm, v(140.75, 59.9) * mm]});
            skFitSpline(sketch, "E859", {"points": [v(140.75, 59.9) * mm, v(141.26, 60.42) * mm, v(149.5, 59.11) * mm, v(153.75, 59.9) * mm]});
            skFitSpline(sketch, "E860", {"points": [v(153.75, 59.9) * mm, v(155.14, 60.17) * mm, v(156.43, 61.53) * mm, v(156.75, 62.9) * mm]});
            skFitSpline(sketch, "E861", {"points": [v(156.75, 62.9) * mm, v(157.5, 66.16) * mm, v(157.5, 69.66) * mm, v(156.75, 72.9) * mm]});
            skFitSpline(sketch, "E862", {"points": [v(156.75, 72.9) * mm, v(156.43, 74.29) * mm, v(154.18, 74.56) * mm, v(153.75, 75.9) * mm]});
            skFitSpline(sketch, "E863", {"points": [v(153.75, 75.9) * mm, v(153.1, 77.98) * mm, v(153.24, 81.9) * mm, v(153.75, 82.4) * mm]});
            skFitSpline(sketch, "E864", {"points": [v(153.75, 82.4) * mm, v(154.26, 82.92) * mm, v(156.24, 82.92) * mm, v(156.75, 82.4) * mm]});
            skFitSpline(sketch, "E865", {"points": [v(156.75, 82.4) * mm, v(157.26, 81.9) * mm, v(156.28, 80.29) * mm, v(156.75, 79.4) * mm]});
            skFitSpline(sketch, "E866", {"points": [v(156.75, 79.4) * mm, v(157.53, 77.96) * mm, v(158.77, 76.65) * mm, v(160.25, 75.9) * mm]});
            skFitSpline(sketch, "E867", {"points": [v(160.25, 75.9) * mm, v(161.3, 75.39) * mm, v(162.7, 76.4) * mm, v(163.75, 75.9) * mm]});
            skFitSpline(sketch, "E868", {"points": [v(163.75, 75.9) * mm, v(165.03, 75.32) * mm, v(166.49, 74.3) * mm, v(166.75, 72.9) * mm]});
            skFitSpline(sketch, "E869", {"points": [v(166.75, 72.9) * mm, v(167.55, 68.65) * mm, v(167.65, 64.15) * mm, v(166.75, 59.9) * mm]});
            skFitSpline(sketch, "E870", {"points": [v(166.75, 59.9) * mm, v(166.4, 58.3) * mm, v(164.84, 56.84) * mm, v(163.25, 56.4) * mm]});
            skFitSpline(sketch, "E871", {"points": [v(163.25, 56.4) * mm, v(160.2, 55.59) * mm, v(156.8, 57.23) * mm, v(153.75, 56.4) * mm]});
            skFitSpline(sketch, "E872", {"points": [v(153.75, 56.4) * mm, v(152.16, 55.98) * mm, v(151.03, 54.36) * mm, v(150.25, 52.9) * mm]});
            skFitSpline(sketch, "E873", {"points": [v(150.25, 52.9) * mm, v(149.78, 52.03) * mm, v(150.76, 50.42) * mm, v(150.25, 49.9) * mm]});
            skFitSpline(sketch, "E874", {"points": [v(150.25, 49.9) * mm, v(149.74, 49.4) * mm, v(147.57, 49.08) * mm, v(146.75, 49.9) * mm]});
            skFitSpline(sketch, "E875", {"points": [v(146.75, 49.9) * mm, v(145.92, 50.73) * mm, v(147.26, 52.9) * mm, v(146.75, 53.4) * mm]});
            skFitSpline(sketch, "E876", {"points": [v(146.75, 53.4) * mm, v(146.24, 53.92) * mm, v(140.62, 54.3) * mm, v(137.75, 53.4) * mm]});
            skFitSpline(sketch, "E877", {"points": [v(137.75, 53.4) * mm, v(135.95, 52.85) * mm, v(134.69, 51.05) * mm, v(133.75, 49.4) * mm]});
            skFitSpline(sketch, "E878", {"points": [v(133.75, 49.4) * mm, v(133.25, 48.54) * mm, v(134.26, 46.92) * mm, v(133.75, 46.4) * mm]});
            skFitSpline(sketch, "E879", {"points": [v(133.75, 46.4) * mm, v(133.24, 45.9) * mm, v(131.4, 45.65) * mm, v(130.75, 46.4) * mm]});
            skFitSpline(sketch, "E880", {"points": [v(130.75, 46.4) * mm, v(130, 47.3) * mm, v(131.57, 49.08) * mm, v(130.75, 49.9) * mm]});
            skFitSpline(sketch, "E881", {"points": [v(130.75, 49.9) * mm, v(129.92, 50.73) * mm, v(127.76, 50.42) * mm, v(127.25, 49.9) * mm]});
            skFitSpline(sketch, "E882", {"points": [v(127.25, 49.9) * mm, v(126.74, 49.4) * mm, v(127.76, 46.92) * mm, v(127.25, 46.4) * mm]});
            skFitSpline(sketch, "E883", {"points": [v(127.25, 46.4) * mm, v(126.74, 45.9) * mm, v(125.13, 45.93) * mm, v(124.25, 46.4) * mm]});
            skFitSpline(sketch, "E884", {"points": [v(124.25, 46.4) * mm, v(122.8, 47.2) * mm, v(122.34, 49.48) * mm, v(120.75, 49.9) * mm]});
            skFitSpline(sketch, "E885", {"points": [v(120.75, 49.9) * mm, v(117.7, 50.73) * mm, v(114.3, 50.73) * mm, v(111.25, 49.9) * mm]});
            skFitSpline(sketch, "E886", {"points": [v(111.25, 49.9) * mm, v(109.66, 49.48) * mm, v(109.23, 47.15) * mm, v(107.75, 46.4) * mm]});
            skFitSpline(sketch, "E887", {"points": [v(107.75, 46.4) * mm, v(106.7, 45.89) * mm, v(104.76, 46.92) * mm, v(104.25, 46.4) * mm]});
            skFitSpline(sketch, "E888", {"points": [v(104.25, 46.4) * mm, v(103.74, 45.9) * mm, v(103.74, 40.92) * mm, v(104.25, 40.4) * mm]});
            skFitSpline(sketch, "E889", {"points": [v(104.25, 40.4) * mm, v(104.76, 39.9) * mm, v(113.34, 41.32) * mm, v(117.75, 40.4) * mm]});
            skFitSpline(sketch, "E890", {"points": [v(117.75, 40.4) * mm, v(119.37, 40.08) * mm, v(119.8, 37.7) * mm, v(121.25, 36.9) * mm]});
            skFitSpline(sketch, "E891", {"points": [v(121.25, 36.9) * mm, v(122.13, 36.43) * mm, v(123.74, 36.4) * mm, v(124.25, 36.9) * mm]});
            skFitSpline(sketch, "E892", {"points": [v(124.25, 36.9) * mm, v(124.76, 37.42) * mm, v(123.74, 42.9) * mm, v(124.25, 43.4) * mm]});
            skFitSpline(sketch, "E893", {"points": [v(124.25, 43.4) * mm, v(124.76, 43.92) * mm, v(126.54, 44.12) * mm, v(127.25, 43.4) * mm]});
            skFitSpline(sketch, "E894", {"points": [v(127.25, 43.4) * mm, v(127.96, 42.7) * mm, v(126.74, 40.92) * mm, v(127.25, 40.4) * mm]});
            skFitSpline(sketch, "E895", {"points": [v(127.25, 40.4) * mm, v(127.76, 39.9) * mm, v(134.02, 39.57) * mm, v(137.25, 40.4) * mm]});
            skFitSpline(sketch, "E896", {"points": [v(137.25, 40.4) * mm, v(138.85, 40.82) * mm, v(140.18, 42.36) * mm, v(140.75, 43.9) * mm]});
            skFitSpline(sketch, "E897", {"points": [v(140.75, 43.9) * mm, v(141.44, 45.79) * mm, v(140.24, 49.4) * mm, v(140.75, 49.9) * mm]});
            skFitSpline(sketch, "E898", {"points": [v(140.75, 49.9) * mm, v(141.26, 50.42) * mm, v(143.24, 50.42) * mm, v(143.75, 49.9) * mm]});
            skFitSpline(sketch, "E899", {"points": [v(143.75, 49.9) * mm, v(144.26, 49.4) * mm, v(143.24, 43.92) * mm, v(143.75, 43.4) * mm]});
            skFitSpline(sketch, "E900", {"points": [v(143.75, 43.4) * mm, v(144.26, 42.9) * mm, v(153.24, 42.9) * mm, v(153.75, 43.4) * mm]});
            skFitSpline(sketch, "E901", {"points": [v(153.75, 43.4) * mm, v(154.26, 43.92) * mm, v(153.08, 48.17) * mm, v(153.75, 50.4) * mm]});
            skFitSpline(sketch, "E902", {"points": [v(153.75, 50.4) * mm, v(154.16, 51.76) * mm, v(155.37, 53.1) * mm, v(156.75, 53.4) * mm]});
            skFitSpline(sketch, "E903", {"points": [v(156.75, 53.4) * mm, v(160, 54.16) * mm, v(166.24, 53.92) * mm, v(166.75, 53.4) * mm]});
            skFitSpline(sketch, "E904", {"points": [v(166.75, 53.4) * mm, v(167.26, 52.9) * mm, v(167.26, 50.42) * mm, v(166.75, 49.9) * mm]});
            skFitSpline(sketch, "E905", {"points": [v(166.75, 49.9) * mm, v(166.24, 49.4) * mm, v(162.3, 50.62) * mm, v(160.25, 49.9) * mm]});
            skFitSpline(sketch, "E906", {"points": [v(160.25, 49.9) * mm, v(158.7, 49.36) * mm, v(157.51, 47.87) * mm, v(156.75, 46.4) * mm]});
            skFitSpline(sketch, "E907", {"points": [v(156.75, 46.4) * mm, v(156.26, 45.47) * mm, v(156.15, 43.62) * mm, v(156.75, 43.21) * mm]});
            skFitSpline(sketch, "E908", {"points": [v(156.75, 43.21) * mm, v(157.35, 42.8) * mm, v(166.15, 47.51) * mm, v(166.75, 47.1) * mm]});
            skFitSpline(sketch, "E909", {"points": [v(166.75, 47.1) * mm, v(167.35, 46.7) * mm, v(167.26, 40.92) * mm, v(166.75, 40.4) * mm]});
            skFitSpline(sketch, "E910", {"points": [v(166.75, 40.4) * mm, v(166.24, 39.9) * mm, v(149.36, 41.43) * mm, v(140.75, 40.4) * mm]});
            skFitSpline(sketch, "E911", {"points": [v(140.75, 40.4) * mm, v(139.11, 40.21) * mm, v(138.8, 37.45) * mm, v(137.25, 36.9) * mm]});
            skFitSpline(sketch, "E912", {"points": [v(137.25, 36.9) * mm, v(135.2, 36.2) * mm, v(132.84, 37.48) * mm, v(130.75, 36.9) * mm]});
            skFitSpline(sketch, "E913", {"points": [v(130.75, 36.9) * mm, v(129.01, 36.43) * mm, v(128, 34.3) * mm, v(126.25, 33.9) * mm]});
            skFitSpline(sketch, "E914", {"points": [v(126.25, 33.9) * mm, v(123.32, 33.26) * mm, v(120.16, 33.18) * mm, v(117.25, 33.9) * mm]});
            skFitSpline(sketch, "E915", {"points": [v(117.25, 33.9) * mm, v(115.88, 34.25) * mm, v(115.6, 36.48) * mm, v(114.25, 36.9) * mm]});
            skFitSpline(sketch, "E916", {"points": [v(114.25, 36.9) * mm, v(112.18, 37.56) * mm, v(108.26, 37.42) * mm, v(107.75, 36.9) * mm]});
            skFitSpline(sketch, "E917", {"points": [v(107.75, 36.9) * mm, v(107.24, 36.4) * mm, v(107.24, 27.92) * mm, v(107.75, 27.4) * mm]});
            skFitSpline(sketch, "E918", {"points": [v(107.75, 27.4) * mm, v(108.26, 26.9) * mm, v(117.24, 27.92) * mm, v(117.75, 27.4) * mm]});
            skFitSpline(sketch, "E919", {"points": [v(117.75, 27.4) * mm, v(118.26, 26.9) * mm, v(118.26, 24.42) * mm, v(117.75, 23.9) * mm]});
            skFitSpline(sketch, "E920", {"points": [v(117.75, 23.9) * mm, v(117.24, 23.4) * mm, v(110.98, 24.75) * mm, v(107.75, 23.9) * mm]});
            skFitSpline(sketch, "E921", {"points": [v(107.75, 23.9) * mm, v(106.15, 23.5) * mm, v(104.82, 21.96) * mm, v(104.25, 20.4) * mm]});
            skFitSpline(sketch, "E922", {"points": [v(104.25, 20.4) * mm, v(103.56, 18.53) * mm, v(103.74, 14.92) * mm, v(104.25, 14.4) * mm]});
            skFitSpline(sketch, "E923", {"points": [v(104.25, 14.4) * mm, v(104.76, 13.9) * mm, v(106.92, 15.23) * mm, v(107.75, 14.4) * mm]});
            skFitSpline(sketch, "E924", {"points": [v(107.75, 14.4) * mm, v(108.57, 13.58) * mm, v(108.26, 11.42) * mm, v(107.75, 10.9) * mm]});
            skFitSpline(sketch, "E925", {"points": [v(107.75, 10.9) * mm, v(107.24, 10.4) * mm, v(94.68, 11.89) * mm, v(88.25, 10.9) * mm]});
            skFitSpline(sketch, "E926", {"points": [v(88.25, 10.9) * mm, v(86.62, 10.66) * mm, v(85.53, 8.86) * mm, v(84.75, 7.4) * mm]});
            skFitSpline(sketch, "E927", {"points": [v(84.75, 7.4) * mm, v(84.28, 6.53) * mm, v(84.24, 4.92) * mm, v(84.75, 4.4) * mm]});
            skFitSpline(sketch, "E928", {"points": [v(84.75, 4.4) * mm, v(85.26, 3.9) * mm, v(87.36, 5.17) * mm, v(88.25, 4.4) * mm]});
            skFitSpline(sketch, "E929", {"points": [v(88.25, 4.4) * mm, v(89, 3.76) * mm, v(88.76, 1.92) * mm, v(88.25, 1.4) * mm]});
            skFitSpline(sketch, "E930", {"points": [v(88.25, 1.4) * mm, v(87.74, 0.9) * mm, v(85.26, 1.92) * mm, v(84.75, 1.4) * mm]});
            skFitSpline(sketch, "E931", {"points": [v(84.75, 1.4) * mm, v(84.24, 0.9) * mm, v(84.24, -1.08) * mm, v(84.75, -1.6) * mm]});
            skFitSpline(sketch, "E932", {"points": [v(84.75, -1.6) * mm, v(85.26, -2.1) * mm, v(94.24, -1.08) * mm, v(94.75, -1.6) * mm]});
            skFitSpline(sketch, "E933", {"points": [v(94.75, -1.6) * mm, v(95.26, -2.1) * mm, v(95.26, -4.58) * mm, v(94.75, -5.1) * mm]});
            skFitSpline(sketch, "E934", {"points": [v(94.75, -5.1) * mm, v(94.24, -5.6) * mm, v(88.3, -4.27) * mm, v(85.25, -5.1) * mm]});
            skFitSpline(sketch, "E935", {"points": [v(85.25, -5.1) * mm, v(83.66, -5.52) * mm, v(83.3, -8.05) * mm, v(81.75, -8.6) * mm]});
            skFitSpline(sketch, "E936", {"points": [v(81.75, -8.6) * mm, v(79.7, -9.3) * mm, v(77.3, -7.88) * mm, v(75.25, -8.6) * mm]});
            skFitSpline(sketch, "E937", {"points": [v(75.25, -8.6) * mm, v(73.7, -9.14) * mm, v(72.49, -10.62) * mm, v(71.75, -12.1) * mm]});
            skFitSpline(sketch, "E938", {"points": [v(71.75, -12.1) * mm, v(70.26, -15.06) * mm, v(70.67, -18.88) * mm, v(68.75, -21.6) * mm]});
            skFitSpline(sketch, "E939", {"points": [v(68.75, -21.6) * mm, v(65.2, -26.59) * mm, v(60.56, -30.8) * mm, v(55.75, -34.6) * mm]});
            skFitSpline(sketch, "E940", {"points": [v(55.75, -34.6) * mm, v(54.83, -35.31) * mm, v(53.3, -34.1) * mm, v(52.25, -34.6) * mm]});
            skFitSpline(sketch, "E941", {"points": [v(52.25, -34.6) * mm, v(50.97, -35.18) * mm, v(49.84, -36.3) * mm, v(49.25, -37.6) * mm]});
            skFitSpline(sketch, "E942", {"points": [v(49.25, -37.6) * mm, v(48.76, -38.65) * mm, v(49.77, -40.05) * mm, v(49.25, -41.1) * mm]});
            skFitSpline(sketch, "E943", {"points": [v(49.25, -41.1) * mm, v(48.51, -42.57) * mm, v(46.17, -43) * mm, v(45.75, -44.6) * mm]});
            skFitSpline(sketch, "E944", {"points": [v(45.75, -44.6) * mm, v(44.92, -47.71) * mm, v(45.15, -53.88) * mm, v(45.75, -54.29) * mm]});
            skFitSpline(sketch, "E945", {"points": [v(45.75, -54.29) * mm, v(46.35, -54.7) * mm, v(52.28, -52.24) * mm, v(55.25, -50.6) * mm]});
            skFitSpline(sketch, "E946", {"points": [v(55.25, -50.6) * mm, v(56.7, -49.8) * mm, v(57.97, -48.54) * mm, v(58.75, -47.1) * mm]});
            skFitSpline(sketch, "E947", {"points": [v(58.75, -47.1) * mm, v(59.22, -46.21) * mm, v(58.28, -44.97) * mm, v(58.75, -44.1) * mm]});
            skFitSpline(sketch, "E948", {"points": [v(58.75, -44.1) * mm, v(59.53, -42.64) * mm, v(60.8, -41.37) * mm, v(62.25, -40.6) * mm]});
            skFitSpline(sketch, "E949", {"points": [v(62.25, -40.6) * mm, v(63.13, -40.12) * mm, v(64.42, -41.16) * mm, v(65.25, -40.6) * mm]});
            skFitSpline(sketch, "E950", {"points": [v(65.25, -40.6) * mm, v(67.78, -38.86) * mm, v(70.6, -36.93) * mm, v(71.75, -34.1) * mm]});
            skFitSpline(sketch, "E951", {"points": [v(71.75, -34.1) * mm, v(72.94, -31.16) * mm, v(70.93, -27.65) * mm, v(71.75, -24.6) * mm]});
            skFitSpline(sketch, "E952", {"points": [v(71.75, -24.6) * mm, v(72.18, -23) * mm, v(74.58, -20.81) * mm, v(75.25, -21.1) * mm]});
            skFitSpline(sketch, "E953", {"points": [v(75.25, -21.1) * mm, v(75.92, -21.37) * mm, v(74.74, -27.58) * mm, v(75.25, -28.1) * mm]});
            skFitSpline(sketch, "E954", {"points": [v(75.25, -28.1) * mm, v(75.76, -28.6) * mm, v(79.49, -29.04) * mm, v(81.25, -28.1) * mm]});
            skFitSpline(sketch, "E955", {"points": [v(81.25, -28.1) * mm, v(84.16, -26.53) * mm, v(86.73, -24.02) * mm, v(88.25, -21.1) * mm]});
            skFitSpline(sketch, "E956", {"points": [v(88.25, -21.1) * mm, v(89.25, -19.17) * mm, v(87.6, -16.66) * mm, v(88.25, -14.6) * mm]});
            skFitSpline(sketch, "E957", {"points": [v(88.25, -14.6) * mm, v(88.68, -13.24) * mm, v(89.9, -12) * mm, v(91.25, -11.6) * mm]});
            skFitSpline(sketch, "E958", {"points": [v(91.25, -11.6) * mm, v(93.48, -10.92) * mm, v(96.01, -12.26) * mm, v(98.25, -11.6) * mm]});
            skFitSpline(sketch, "E959", {"points": [v(98.25, -11.6) * mm, v(99.6, -11.18) * mm, v(100.93, -9.97) * mm, v(101.25, -8.6) * mm]});
            skFitSpline(sketch, "E960", {"points": [v(101.25, -8.6) * mm, v(102, -5.34) * mm, v(100.4, -1.81) * mm, v(101.25, 1.4) * mm]});
            skFitSpline(sketch, "E961", {"points": [v(101.25, 1.4) * mm, v(101.69, 3.05) * mm, v(104.2, 5.33) * mm, v(104.86, 5.02) * mm]});
            skFitSpline(sketch, "E962", {"points": [v(104.86, 5.02) * mm, v(105.52, 4.7) * mm, v(103.71, -1.05) * mm, v(104.2, -1.6) * mm]});
            skFitSpline(sketch, "E963", {"points": [v(104.2, -1.6) * mm, v(104.69, -2.13) * mm, v(110.74, -2.1) * mm, v(111.25, -1.6) * mm]});
            skFitSpline(sketch, "E964", {"points": [v(111.25, -1.6) * mm, v(111.76, -1.08) * mm, v(111.25, 0.4) * mm, v(111.25, 1.4) * mm]});
            skFitSpline(sketch, "E965", {"points": [v(111.25, -1.6) * mm, v(111.25, -0.6) * mm, v(111.25, 0.41) * mm, v(111.25, 1.4) * mm]});
            skFitSpline(sketch, "E966", {"points": [v(-123.75, 79.4) * mm, v(-124.26, 78.9) * mm, v(-123.24, 76.42) * mm, v(-123.75, 75.9) * mm]});
            skFitSpline(sketch, "E967", {"points": [v(-123.75, 75.9) * mm, v(-124.26, 75.4) * mm, v(-126.74, 76.42) * mm, v(-127.25, 75.9) * mm]});
            skFitSpline(sketch, "E968", {"points": [v(-127.25, 75.9) * mm, v(-127.76, 75.4) * mm, v(-127.76, 69.92) * mm, v(-127.25, 69.4) * mm]});
            skFitSpline(sketch, "E969", {"points": [v(-127.25, 69.4) * mm, v(-126.74, 68.9) * mm, v(-121.26, 68.9) * mm, v(-120.75, 69.4) * mm]});
            skFitSpline(sketch, "E970", {"points": [v(-120.75, 69.4) * mm, v(-120.24, 69.92) * mm, v(-121.26, 75.4) * mm, v(-120.75, 75.9) * mm]});
            skFitSpline(sketch, "E971", {"points": [v(-120.75, 75.9) * mm, v(-120.24, 76.42) * mm, v(-118.26, 76.42) * mm, v(-117.75, 75.9) * mm]});
            skFitSpline(sketch, "E972", {"points": [v(-117.75, 75.9) * mm, v(-117.24, 75.4) * mm, v(-118.26, 69.92) * mm, v(-117.75, 69.4) * mm]});
            skFitSpline(sketch, "E973", {"points": [v(-117.75, 69.4) * mm, v(-117.24, 68.9) * mm, v(-111.76, 68.9) * mm, v(-111.25, 69.4) * mm]});
            skFitSpline(sketch, "E974", {"points": [v(-111.25, 69.4) * mm, v(-110.74, 69.92) * mm, v(-111.76, 75.4) * mm, v(-111.25, 75.9) * mm]});
            skFitSpline(sketch, "E975", {"points": [v(-111.25, 75.9) * mm, v(-110.74, 76.42) * mm, v(-108.26, 76.42) * mm, v(-107.75, 75.9) * mm]});
            skFitSpline(sketch, "E976", {"points": [v(-107.75, 75.9) * mm, v(-107.24, 75.4) * mm, v(-108.26, 69.92) * mm, v(-107.75, 69.4) * mm]});
            skFitSpline(sketch, "E977", {"points": [v(-107.75, 69.4) * mm, v(-107.24, 68.9) * mm, v(-105.26, 68.9) * mm, v(-104.75, 69.4) * mm]});
            skFitSpline(sketch, "E978", {"points": [v(-104.75, 69.4) * mm, v(-104.24, 69.92) * mm, v(-105.26, 75.4) * mm, v(-104.75, 75.9) * mm]});
            skFitSpline(sketch, "E979", {"points": [v(-104.75, 75.9) * mm, v(-104.24, 76.42) * mm, v(-101.76, 76.42) * mm, v(-101.25, 75.9) * mm]});
            skFitSpline(sketch, "E980", {"points": [v(-101.25, 75.9) * mm, v(-100.74, 75.4) * mm, v(-101.76, 69.92) * mm, v(-101.25, 69.4) * mm]});
            skFitSpline(sketch, "E981", {"points": [v(-101.25, 69.4) * mm, v(-100.74, 68.9) * mm, v(-95.26, 68.9) * mm, v(-94.75, 69.4) * mm]});
            skFitSpline(sketch, "E982", {"points": [v(-94.75, 69.4) * mm, v(-94.24, 69.92) * mm, v(-94.24, 72.4) * mm, v(-94.75, 72.9) * mm]});
            skFitSpline(sketch, "E983", {"points": [v(-94.75, 72.9) * mm, v(-95.26, 73.42) * mm, v(-97.36, 72.15) * mm, v(-98.25, 72.9) * mm]});
            skFitSpline(sketch, "E984", {"points": [v(-98.25, 72.9) * mm, v(-99, 73.56) * mm, v(-98.76, 75.4) * mm, v(-98.25, 75.9) * mm]});
            skFitSpline(sketch, "E985", {"points": [v(-98.25, 75.9) * mm, v(-97.74, 76.42) * mm, v(-95.03, 75.24) * mm, v(-94.75, 75.9) * mm]});
            skFitSpline(sketch, "E986", {"points": [v(-94.75, 75.9) * mm, v(-94.47, 76.58) * mm, v(-96.61, 79.21) * mm, v(-98.25, 79.4) * mm]});
            skFitSpline(sketch, "E987", {"points": [v(-98.25, 79.4) * mm, v(-106.69, 80.43) * mm, v(-123.24, 79.92) * mm, v(-123.75, 79.4) * mm]});
            skFitSpline(sketch, "E988", {"points": [v(123.75, 79.4) * mm, v(124.26, 78.9) * mm, v(123.24, 76.42) * mm, v(123.75, 75.9) * mm]});
            skFitSpline(sketch, "E989", {"points": [v(123.75, 75.9) * mm, v(124.26, 75.4) * mm, v(126.74, 76.42) * mm, v(127.25, 75.9) * mm]});
            skFitSpline(sketch, "E990", {"points": [v(127.25, 75.9) * mm, v(127.76, 75.4) * mm, v(127.76, 69.92) * mm, v(127.25, 69.4) * mm]});
            skFitSpline(sketch, "E991", {"points": [v(127.25, 69.4) * mm, v(126.74, 68.9) * mm, v(121.26, 68.9) * mm, v(120.75, 69.4) * mm]});
            skFitSpline(sketch, "E992", {"points": [v(120.75, 69.4) * mm, v(120.24, 69.92) * mm, v(121.26, 75.4) * mm, v(120.75, 75.9) * mm]});
            skFitSpline(sketch, "E993", {"points": [v(120.75, 75.9) * mm, v(120.24, 76.42) * mm, v(118.26, 76.42) * mm, v(117.75, 75.9) * mm]});
            skFitSpline(sketch, "E994", {"points": [v(117.75, 75.9) * mm, v(117.24, 75.4) * mm, v(118.26, 69.92) * mm, v(117.75, 69.4) * mm]});
            skFitSpline(sketch, "E995", {"points": [v(117.75, 69.4) * mm, v(117.24, 68.9) * mm, v(111.76, 68.9) * mm, v(111.25, 69.4) * mm]});
            skFitSpline(sketch, "E996", {"points": [v(111.25, 69.4) * mm, v(110.74, 69.92) * mm, v(111.76, 75.4) * mm, v(111.25, 75.9) * mm]});
            skFitSpline(sketch, "E997", {"points": [v(111.25, 75.9) * mm, v(110.74, 76.42) * mm, v(108.26, 76.42) * mm, v(107.75, 75.9) * mm]});
            skFitSpline(sketch, "E998", {"points": [v(107.75, 75.9) * mm, v(107.24, 75.4) * mm, v(108.26, 69.92) * mm, v(107.75, 69.4) * mm]});
            skFitSpline(sketch, "E999", {"points": [v(107.75, 69.4) * mm, v(107.24, 68.9) * mm, v(105.26, 68.9) * mm, v(104.75, 69.4) * mm]});
            skFitSpline(sketch, "E1000", {"points": [v(104.75, 69.4) * mm, v(104.24, 69.92) * mm, v(105.26, 75.4) * mm, v(104.75, 75.9) * mm]});
            skFitSpline(sketch, "E1001", {"points": [v(104.75, 75.9) * mm, v(104.24, 76.42) * mm, v(101.76, 76.42) * mm, v(101.25, 75.9) * mm]});
            skFitSpline(sketch, "E1002", {"points": [v(101.25, 75.9) * mm, v(100.74, 75.4) * mm, v(101.76, 69.92) * mm, v(101.25, 69.4) * mm]});
            skFitSpline(sketch, "E1003", {"points": [v(101.25, 69.4) * mm, v(100.74, 68.9) * mm, v(95.26, 68.9) * mm, v(94.75, 69.4) * mm]});
            skFitSpline(sketch, "E1004", {"points": [v(94.75, 69.4) * mm, v(94.24, 69.92) * mm, v(94.24, 72.4) * mm, v(94.75, 72.9) * mm]});
            skFitSpline(sketch, "E1005", {"points": [v(94.75, 72.9) * mm, v(95.26, 73.42) * mm, v(97.74, 72.4) * mm, v(98.25, 72.9) * mm]});
            skFitSpline(sketch, "E1006", {"points": [v(98.25, 72.9) * mm, v(98.76, 73.42) * mm, v(99, 75.26) * mm, v(98.25, 75.9) * mm]});
            skFitSpline(sketch, "E1007", {"points": [v(98.25, 75.9) * mm, v(97.36, 76.67) * mm, v(95.03, 75.24) * mm, v(94.75, 75.9) * mm]});
            skFitSpline(sketch, "E1008", {"points": [v(94.75, 75.9) * mm, v(94.47, 76.58) * mm, v(96.61, 79.21) * mm, v(98.25, 79.4) * mm]});
            skFitSpline(sketch, "E1009", {"points": [v(98.25, 79.4) * mm, v(106.69, 80.43) * mm, v(123.24, 79.92) * mm, v(123.75, 79.4) * mm]});
            skFitSpline(sketch, "E1010", {"points": [v(-117.75, 56.4) * mm, v(-118.26, 55.9) * mm, v(-118.26, 53.92) * mm, v(-117.75, 53.4) * mm]});
            skFitSpline(sketch, "E1011", {"points": [v(-117.75, 53.4) * mm, v(-117.24, 52.9) * mm, v(-111.76, 52.9) * mm, v(-111.25, 53.4) * mm]});
            skFitSpline(sketch, "E1012", {"points": [v(-111.25, 53.4) * mm, v(-110.74, 53.92) * mm, v(-110.74, 55.9) * mm, v(-111.25, 56.4) * mm]});
            skFitSpline(sketch, "E1013", {"points": [v(-111.25, 56.4) * mm, v(-111.76, 56.92) * mm, v(-117.24, 56.92) * mm, v(-117.75, 56.4) * mm]});
            skFitSpline(sketch, "E1014", {"points": [v(111.25, 56.4) * mm, v(110.74, 55.9) * mm, v(110.74, 53.92) * mm, v(111.25, 53.4) * mm]});
            skFitSpline(sketch, "E1015", {"points": [v(111.25, 53.4) * mm, v(111.76, 52.9) * mm, v(117.24, 52.9) * mm, v(117.75, 53.4) * mm]});
            skFitSpline(sketch, "E1016", {"points": [v(117.75, 53.4) * mm, v(118.26, 53.92) * mm, v(118.26, 55.9) * mm, v(117.75, 56.4) * mm]});
            skFitSpline(sketch, "E1017", {"points": [v(117.75, 56.4) * mm, v(117.24, 56.92) * mm, v(111.76, 56.92) * mm, v(111.25, 56.4) * mm]});
            skFitSpline(sketch, "E1018", {"points": [v(-104.25, 36.9) * mm, v(-104.76, 36.4) * mm, v(-104.76, 30.92) * mm, v(-104.25, 30.4) * mm]});
            skFitSpline(sketch, "E1019", {"points": [v(-104.25, 30.4) * mm, v(-103.74, 29.9) * mm, v(-92.64, 29.64) * mm, v(-91.8, 30.4) * mm]});
            skFitSpline(sketch, "E1020", {"points": [v(-91.8, 30.4) * mm, v(-90.95, 31.18) * mm, v(-90.71, 36.37) * mm, v(-91.2, 36.9) * mm]});
            skFitSpline(sketch, "E1021", {"points": [v(-91.2, 36.9) * mm, v(-91.7, 37.45) * mm, v(-103.74, 37.42) * mm, v(-104.25, 36.9) * mm]});
            skFitSpline(sketch, "E1022", {"points": [v(-55.25, 36.9) * mm, v(-55.76, 36.4) * mm, v(-55.76, 30.92) * mm, v(-55.25, 30.4) * mm]});
            skFitSpline(sketch, "E1023", {"points": [v(-55.25, 30.4) * mm, v(-54.74, 29.9) * mm, v(-50.14, 29.64) * mm, v(-49.3, 30.4) * mm]});
            skFitSpline(sketch, "E1024", {"points": [v(-49.3, 30.4) * mm, v(-48.45, 31.18) * mm, v(-48.21, 36.37) * mm, v(-48.7, 36.9) * mm]});
            skFitSpline(sketch, "E1025", {"points": [v(-48.7, 36.9) * mm, v(-49.2, 37.45) * mm, v(-54.74, 37.42) * mm, v(-55.25, 36.9) * mm]});
            skFitSpline(sketch, "E1026", {"points": [v(-32.25, 36.9) * mm, v(-32.76, 36.4) * mm, v(-32.76, 30.92) * mm, v(-32.25, 30.4) * mm]});
            skFitSpline(sketch, "E1027", {"points": [v(-32.25, 30.4) * mm, v(-31.74, 29.9) * mm, v(-26.76, 29.9) * mm, v(-26.25, 30.4) * mm]});
            skFitSpline(sketch, "E1028", {"points": [v(-26.25, 30.4) * mm, v(-25.74, 30.92) * mm, v(-25.74, 36.4) * mm, v(-26.25, 36.9) * mm]});
            skFitSpline(sketch, "E1029", {"points": [v(-26.25, 36.9) * mm, v(-26.76, 37.42) * mm, v(-31.74, 37.42) * mm, v(-32.25, 36.9) * mm]});
            skFitSpline(sketch, "E1030", {"points": [v(26.25, 36.9) * mm, v(25.74, 36.4) * mm, v(25.74, 30.92) * mm, v(26.25, 30.4) * mm]});
            skFitSpline(sketch, "E1031", {"points": [v(26.25, 30.4) * mm, v(26.76, 29.9) * mm, v(31.36, 29.64) * mm, v(32.2, 30.4) * mm]});
            skFitSpline(sketch, "E1032", {"points": [v(32.2, 30.4) * mm, v(33.05, 31.18) * mm, v(33.28, 36.37) * mm, v(32.8, 36.9) * mm]});
            skFitSpline(sketch, "E1033", {"points": [v(32.8, 36.9) * mm, v(32.3, 37.45) * mm, v(26.76, 37.42) * mm, v(26.25, 36.9) * mm]});
            skFitSpline(sketch, "E1034", {"points": [v(49.25, 36.9) * mm, v(48.74, 36.4) * mm, v(48.74, 30.92) * mm, v(49.25, 30.4) * mm]});
            skFitSpline(sketch, "E1035", {"points": [v(49.25, 30.4) * mm, v(49.76, 29.9) * mm, v(54.74, 29.9) * mm, v(55.25, 30.4) * mm]});
            skFitSpline(sketch, "E1036", {"points": [v(55.25, 30.4) * mm, v(55.76, 30.92) * mm, v(55.76, 36.4) * mm, v(55.25, 36.9) * mm]});
            skFitSpline(sketch, "E1037", {"points": [v(55.25, 36.9) * mm, v(54.74, 37.42) * mm, v(49.76, 37.42) * mm, v(49.25, 36.9) * mm]});
            skFitSpline(sketch, "E1038", {"points": [v(104.25, 36.9) * mm, v(104.76, 36.4) * mm, v(104.76, 30.92) * mm, v(104.25, 30.4) * mm]});
            skFitSpline(sketch, "E1039", {"points": [v(104.25, 30.4) * mm, v(103.74, 29.9) * mm, v(91.7, 29.87) * mm, v(91.2, 30.4) * mm]});
            skFitSpline(sketch, "E1040", {"points": [v(91.2, 30.4) * mm, v(90.72, 30.94) * mm, v(90.93, 36.16) * mm, v(91.75, 36.9) * mm]});
            skFitSpline(sketch, "E1041", {"points": [v(91.75, 36.9) * mm, v(92.57, 37.66) * mm, v(103.74, 37.42) * mm, v(104.25, 36.9) * mm]});
            skFitSpline(sketch, "E1042", {"points": [v(-45.75, 33.9) * mm, v(-46.26, 33.4) * mm, v(-46.26, 30.92) * mm, v(-45.75, 30.4) * mm]});
            skFitSpline(sketch, "E1043", {"points": [v(-45.75, 30.4) * mm, v(-45.24, 29.9) * mm, v(-42.76, 29.9) * mm, v(-42.25, 30.4) * mm]});
            skFitSpline(sketch, "E1044", {"points": [v(-42.25, 30.4) * mm, v(-41.74, 30.92) * mm, v(-41.74, 33.4) * mm, v(-42.25, 33.9) * mm]});
            skFitSpline(sketch, "E1045", {"points": [v(-42.25, 33.9) * mm, v(-42.76, 34.42) * mm, v(-45.24, 34.42) * mm, v(-45.75, 33.9) * mm]});
            skFitSpline(sketch, "E1046", {"points": [v(-39.25, 33.9) * mm, v(-39.76, 33.4) * mm, v(-39.76, 30.92) * mm, v(-39.25, 30.4) * mm]});
            skFitSpline(sketch, "E1047", {"points": [v(-39.25, 30.4) * mm, v(-38.74, 29.9) * mm, v(-36.76, 29.9) * mm, v(-36.25, 30.4) * mm]});
            skFitSpline(sketch, "E1048", {"points": [v(-36.25, 30.4) * mm, v(-35.74, 30.92) * mm, v(-35.74, 33.4) * mm, v(-36.25, 33.9) * mm]});
            skFitSpline(sketch, "E1049", {"points": [v(-36.25, 33.9) * mm, v(-36.76, 34.42) * mm, v(-38.74, 34.42) * mm, v(-39.25, 33.9) * mm]});
            skFitSpline(sketch, "E1050", {"points": [v(-9.75, 33.9) * mm, v(-10.26, 33.4) * mm, v(-10.26, 11.42) * mm, v(-9.75, 10.9) * mm]});
            skFitSpline(sketch, "E1051", {"points": [v(-9.75, 10.9) * mm, v(-9.24, 10.4) * mm, v(-7.26, 10.4) * mm, v(-6.75, 10.9) * mm]});
            skFitSpline(sketch, "E1052", {"points": [v(-6.75, 10.9) * mm, v(-6.24, 11.42) * mm, v(-6.24, 33.4) * mm, v(-6.75, 33.9) * mm]});
            skFitSpline(sketch, "E1053", {"points": [v(-6.75, 33.9) * mm, v(-7.26, 34.42) * mm, v(-9.24, 34.42) * mm, v(-9.75, 33.9) * mm]});
            skFitSpline(sketch, "E1054", {"points": [v(6.75, 33.9) * mm, v(6.24, 33.4) * mm, v(6.24, 11.42) * mm, v(6.75, 10.9) * mm]});
            skFitSpline(sketch, "E1055", {"points": [v(6.75, 10.9) * mm, v(7.26, 10.4) * mm, v(9.24, 10.4) * mm, v(9.75, 10.9) * mm]});
            skFitSpline(sketch, "E1056", {"points": [v(9.75, 10.9) * mm, v(10.26, 11.42) * mm, v(10.26, 33.4) * mm, v(9.75, 33.9) * mm]});
            skFitSpline(sketch, "E1057", {"points": [v(9.75, 33.9) * mm, v(9.24, 34.42) * mm, v(7.26, 34.42) * mm, v(6.75, 33.9) * mm]});
            skFitSpline(sketch, "E1058", {"points": [v(36.25, 33.9) * mm, v(35.74, 33.4) * mm, v(35.74, 30.92) * mm, v(36.25, 30.4) * mm]});
            skFitSpline(sketch, "E1059", {"points": [v(36.25, 30.4) * mm, v(36.76, 29.9) * mm, v(38.74, 29.9) * mm, v(39.25, 30.4) * mm]});
            skFitSpline(sketch, "E1060", {"points": [v(39.25, 30.4) * mm, v(39.76, 30.92) * mm, v(39.76, 33.4) * mm, v(39.25, 33.9) * mm]});
            skFitSpline(sketch, "E1061", {"points": [v(39.25, 33.9) * mm, v(38.74, 34.42) * mm, v(36.76, 34.42) * mm, v(36.25, 33.9) * mm]});
            skFitSpline(sketch, "E1062", {"points": [v(42.25, 33.9) * mm, v(41.74, 33.4) * mm, v(41.74, 30.92) * mm, v(42.25, 30.4) * mm]});
            skFitSpline(sketch, "E1063", {"points": [v(42.25, 30.4) * mm, v(42.76, 29.9) * mm, v(45.24, 29.9) * mm, v(45.75, 30.4) * mm]});
            skFitSpline(sketch, "E1064", {"points": [v(45.75, 30.4) * mm, v(46.26, 30.92) * mm, v(46.26, 33.4) * mm, v(45.75, 33.9) * mm]});
            skFitSpline(sketch, "E1065", {"points": [v(45.75, 33.9) * mm, v(45.24, 34.42) * mm, v(42.76, 34.42) * mm, v(42.25, 33.9) * mm]});
            skFitSpline(sketch, "E1066", {"points": [v(101.75, -79.6) * mm, v(99.43, -79.77) * mm, v(95.26, -80.1) * mm, v(94.75, -79.6) * mm]});
            skFitSpline(sketch, "E1067", {"points": [v(94.75, -79.6) * mm, v(94.24, -79.08) * mm, v(94.24, -77.1) * mm, v(94.75, -76.6) * mm]});
            skFitSpline(sketch, "E1068", {"points": [v(94.75, -76.6) * mm, v(95.26, -76.08) * mm, v(97.27, -77.23) * mm, v(98.25, -76.6) * mm]});
            skFitSpline(sketch, "E1069", {"points": [v(98.25, -76.6) * mm, v(100.82, -74.92) * mm, v(102, -71.46) * mm, v(104.75, -70.1) * mm]});
            skFitSpline(sketch, "E1070", {"points": [v(104.75, -70.1) * mm, v(106.69, -69.12) * mm, v(109.31, -71.06) * mm, v(111.25, -70.1) * mm]});
            skFitSpline(sketch, "E1071", {"points": [v(111.25, -70.1) * mm, v(114, -68.72) * mm, v(114.7, -63.95) * mm, v(117.75, -63.6) * mm]});
            skFitSpline(sketch, "E1072", {"points": [v(117.75, -63.6) * mm, v(133.97, -61.7) * mm, v(166.24, -64.1) * mm, v(166.75, -63.6) * mm]});
            skFitSpline(sketch, "E1073", {"points": [v(166.75, -63.6) * mm, v(167.26, -63.08) * mm, v(167.26, -60.6) * mm, v(166.75, -60.1) * mm]});
            skFitSpline(sketch, "E1074", {"points": [v(166.75, -60.1) * mm, v(166.24, -59.58) * mm, v(154.53, -60.76) * mm, v(154.25, -60.1) * mm]});
            skFitSpline(sketch, "E1075", {"points": [v(154.25, -60.1) * mm, v(153.97, -59.42) * mm, v(155.93, -57.6) * mm, v(157.25, -57.1) * mm]});
            skFitSpline(sketch, "E1076", {"points": [v(157.25, -57.1) * mm, v(159.6, -56.2) * mm, v(162.34, -56.85) * mm, v(164.75, -56.1) * mm]});
            skFitSpline(sketch, "E1077", {"points": [v(164.75, -56.1) * mm, v(165.65, -55.8) * mm, v(166.53, -55) * mm, v(166.75, -54.1) * mm]});
            skFitSpline(sketch, "E1078", {"points": [v(166.75, -54.1) * mm, v(167.25, -51.98) * mm, v(167.26, -48.1) * mm, v(166.75, -47.6) * mm]});
            skFitSpline(sketch, "E1079", {"points": [v(166.75, -47.6) * mm, v(166.24, -47.08) * mm, v(163.76, -47.08) * mm, v(163.25, -47.6) * mm]});
            skFitSpline(sketch, "E1080", {"points": [v(163.25, -47.6) * mm, v(162.74, -48.1) * mm, v(163.72, -49.71) * mm, v(163.25, -50.6) * mm]});
            skFitSpline(sketch, "E1081", {"points": [v(163.25, -50.6) * mm, v(162.47, -52.04) * mm, v(161.2, -53.3) * mm, v(159.75, -54.1) * mm]});
            skFitSpline(sketch, "E1082", {"points": [v(159.75, -54.1) * mm, v(158.87, -54.56) * mm, v(157.26, -54.6) * mm, v(156.75, -54.1) * mm]});
            skFitSpline(sketch, "E1083", {"points": [v(156.75, -54.1) * mm, v(156.24, -53.58) * mm, v(156.24, -51.1) * mm, v(156.75, -50.6) * mm]});
            skFitSpline(sketch, "E1084", {"points": [v(156.75, -50.6) * mm, v(157.26, -50.08) * mm, v(159.74, -51.1) * mm, v(160.25, -50.6) * mm]});
            skFitSpline(sketch, "E1085", {"points": [v(160.25, -50.6) * mm, v(160.76, -50.08) * mm, v(161, -48.24) * mm, v(160.25, -47.6) * mm]});
            skFitSpline(sketch, "E1086", {"points": [v(160.25, -47.6) * mm, v(159.36, -46.83) * mm, v(157.57, -48.42) * mm, v(156.75, -47.6) * mm]});
            skFitSpline(sketch, "E1087", {"points": [v(156.75, -47.6) * mm, v(155.92, -46.77) * mm, v(156.24, -44.6) * mm, v(156.75, -44.1) * mm]});
            skFitSpline(sketch, "E1088", {"points": [v(156.75, -44.1) * mm, v(157.26, -43.58) * mm, v(166.24, -44.6) * mm, v(166.75, -44.1) * mm]});
            skFitSpline(sketch, "E1089", {"points": [v(166.75, -44.1) * mm, v(167.26, -43.58) * mm, v(167.57, -41.42) * mm, v(166.75, -40.6) * mm]});
            skFitSpline(sketch, "E1090", {"points": [v(166.75, -40.6) * mm, v(165.92, -39.77) * mm, v(164.14, -41.35) * mm, v(163.25, -40.6) * mm]});
            skFitSpline(sketch, "E1091", {"points": [v(163.25, -40.6) * mm, v(162.5, -39.94) * mm, v(162.74, -38.1) * mm, v(163.25, -37.6) * mm]});
            skFitSpline(sketch, "E1092", {"points": [v(163.25, -37.6) * mm, v(163.76, -37.08) * mm, v(166.24, -38.1) * mm, v(166.75, -37.6) * mm]});
            skFitSpline(sketch, "E1093", {"points": [v(166.75, -37.6) * mm, v(167.26, -37.08) * mm, v(167.26, -35.1) * mm, v(166.75, -34.6) * mm]});
            skFitSpline(sketch, "E1094", {"points": [v(166.75, -34.6) * mm, v(166.24, -34.08) * mm, v(161.87, -33.61) * mm, v(159.75, -34.6) * mm]});
            skFitSpline(sketch, "E1095", {"points": [v(159.75, -34.6) * mm, v(157.18, -35.78) * mm, v(154.6, -37.9) * mm, v(153.75, -40.6) * mm]});
            skFitSpline(sketch, "E1096", {"points": [v(153.75, -40.6) * mm, v(152.44, -44.72) * mm, v(155.12, -49.48) * mm, v(153.75, -53.6) * mm]});
            skFitSpline(sketch, "E1097", {"points": [v(153.75, -53.6) * mm, v(152.78, -56.5) * mm, v(150, -58.72) * mm, v(147.25, -60.1) * mm]});
            skFitSpline(sketch, "E1098", {"points": [v(147.25, -60.1) * mm, v(145.31, -61.06) * mm, v(141.26, -60.6) * mm, v(140.75, -60.1) * mm]});
            skFitSpline(sketch, "E1099", {"points": [v(140.75, -60.1) * mm, v(140.24, -59.58) * mm, v(140.24, -57.6) * mm, v(140.75, -57.1) * mm]});
            skFitSpline(sketch, "E1100", {"points": [v(140.75, -57.1) * mm, v(141.26, -56.58) * mm, v(143.04, -57.8) * mm, v(143.75, -57.1) * mm]});
            skFitSpline(sketch, "E1101", {"points": [v(143.75, -57.1) * mm, v(144.46, -56.38) * mm, v(144.46, -54.8) * mm, v(143.75, -54.1) * mm]});
            skFitSpline(sketch, "E1102", {"points": [v(143.75, -54.1) * mm, v(143.04, -53.38) * mm, v(141.26, -54.6) * mm, v(140.75, -54.1) * mm]});
            skFitSpline(sketch, "E1103", {"points": [v(140.75, -54.1) * mm, v(140.24, -53.58) * mm, v(141.26, -44.6) * mm, v(140.75, -44.1) * mm]});
            skFitSpline(sketch, "E1104", {"points": [v(140.75, -44.1) * mm, v(140.24, -43.58) * mm, v(137.76, -43.58) * mm, v(137.25, -44.1) * mm]});
            skFitSpline(sketch, "E1105", {"points": [v(137.25, -44.1) * mm, v(136.74, -44.6) * mm, v(137.76, -59.58) * mm, v(137.25, -60.1) * mm]});
            skFitSpline(sketch, "E1106", {"points": [v(137.25, -60.1) * mm, v(136.74, -60.6) * mm, v(134.26, -60.6) * mm, v(133.75, -60.1) * mm]});
            skFitSpline(sketch, "E1107", {"points": [v(133.75, -60.1) * mm, v(133.24, -59.58) * mm, v(134.46, -57.8) * mm, v(133.75, -57.1) * mm]});
            skFitSpline(sketch, "E1108", {"points": [v(133.75, -57.1) * mm, v(133.04, -56.38) * mm, v(131.26, -56.58) * mm, v(130.75, -57.1) * mm]});
            skFitSpline(sketch, "E1109", {"points": [v(130.75, -57.1) * mm, v(130.24, -57.6) * mm, v(131.5, -59.44) * mm, v(130.75, -60.1) * mm]});
            skFitSpline(sketch, "E1110", {"points": [v(130.75, -60.1) * mm, v(129.86, -60.85) * mm, v(127.76, -60.6) * mm, v(127.25, -60.1) * mm]});
            skFitSpline(sketch, "E1111", {"points": [v(127.25, -60.1) * mm, v(126.74, -59.58) * mm, v(127.76, -48.1) * mm, v(127.25, -47.6) * mm]});
            skFitSpline(sketch, "E1112", {"points": [v(127.25, -47.6) * mm, v(126.74, -47.08) * mm, v(124.76, -47.08) * mm, v(124.25, -47.6) * mm]});
            skFitSpline(sketch, "E1113", {"points": [v(124.25, -47.6) * mm, v(123.74, -48.1) * mm, v(124.76, -56.58) * mm, v(124.25, -57.1) * mm]});
            skFitSpline(sketch, "E1114", {"points": [v(124.25, -57.1) * mm, v(123.74, -57.6) * mm, v(121.73, -56.45) * mm, v(120.75, -57.1) * mm]});
            skFitSpline(sketch, "E1115", {"points": [v(120.75, -57.1) * mm, v(118.18, -58.76) * mm, v(117, -62.22) * mm, v(114.25, -63.6) * mm]});
            skFitSpline(sketch, "E1116", {"points": [v(114.25, -63.6) * mm, v(112.31, -64.56) * mm, v(109.6, -62.47) * mm, v(107.75, -63.6) * mm]});
            skFitSpline(sketch, "E1117", {"points": [v(107.75, -63.6) * mm, v(103.72, -66.03) * mm, v(101.94, -71.44) * mm, v(97.75, -73.6) * mm]});
            skFitSpline(sketch, "E1118", {"points": [v(97.75, -73.6) * mm, v(94.93, -75.04) * mm, v(88.76, -74.1) * mm, v(88.25, -73.6) * mm]});
            skFitSpline(sketch, "E1119", {"points": [v(88.25, -73.6) * mm, v(87.74, -73.08) * mm, v(87.74, -70.6) * mm, v(88.25, -70.1) * mm]});
            skFitSpline(sketch, "E1120", {"points": [v(88.25, -70.1) * mm, v(88.76, -69.58) * mm, v(90.7, -70.58) * mm, v(91.75, -70.1) * mm]});
            skFitSpline(sketch, "E1121", {"points": [v(91.75, -70.1) * mm, v(93.03, -69.5) * mm, v(94.16, -68.37) * mm, v(94.75, -67.1) * mm]});
            skFitSpline(sketch, "E1122", {"points": [v(94.75, -67.1) * mm, v(95.24, -66.03) * mm, v(94.26, -64.65) * mm, v(94.75, -63.6) * mm]});
            skFitSpline(sketch, "E1123", {"points": [v(94.75, -63.6) * mm, v(95.34, -62.3) * mm, v(96.37, -60.9) * mm, v(97.75, -60.6) * mm]});
            skFitSpline(sketch, "E1124", {"points": [v(97.75, -60.6) * mm, v(101, -59.84) * mm, v(104.52, -61.43) * mm, v(107.75, -60.6) * mm]});
            skFitSpline(sketch, "E1125", {"points": [v(107.75, -60.6) * mm, v(109.35, -60.18) * mm, v(110.47, -58.54) * mm, v(111.25, -57.1) * mm]});
            skFitSpline(sketch, "E1126", {"points": [v(111.25, -57.1) * mm, v(111.72, -56.21) * mm, v(110.74, -54.6) * mm, v(111.25, -54.1) * mm]});
            skFitSpline(sketch, "E1127", {"points": [v(111.25, -54.1) * mm, v(111.76, -53.58) * mm, v(120.24, -54.6) * mm, v(120.75, -54.1) * mm]});
            skFitSpline(sketch, "E1128", {"points": [v(120.75, -54.1) * mm, v(121.26, -53.58) * mm, v(121.34, -47.83) * mm, v(120.75, -47.41) * mm]});
            skFitSpline(sketch, "E1129", {"points": [v(120.75, -47.41) * mm, v(120.16, -47) * mm, v(111.84, -51.19) * mm, v(111.25, -50.77) * mm]});
            skFitSpline(sketch, "E1130", {"points": [v(111.25, -50.77) * mm, v(110.66, -50.35) * mm, v(110.42, -44.2) * mm, v(111.25, -41.1) * mm]});
            skFitSpline(sketch, "E1131", {"points": [v(111.25, -41.1) * mm, v(111.67, -39.5) * mm, v(113.2, -38.16) * mm, v(114.75, -37.6) * mm]});
            skFitSpline(sketch, "E1132", {"points": [v(114.75, -37.6) * mm, v(116.63, -36.9) * mm, v(120.24, -37.08) * mm, v(120.75, -37.6) * mm]});
            skFitSpline(sketch, "E1133", {"points": [v(120.75, -37.6) * mm, v(121.26, -38.1) * mm, v(119.92, -40.27) * mm, v(120.75, -41.1) * mm]});
            skFitSpline(sketch, "E1134", {"points": [v(120.75, -41.1) * mm, v(121.57, -41.92) * mm, v(123.74, -41.6) * mm, v(124.25, -41.1) * mm]});
            skFitSpline(sketch, "E1135", {"points": [v(124.25, -41.1) * mm, v(124.76, -40.58) * mm, v(123.74, -38.1) * mm, v(124.25, -37.6) * mm]});
            skFitSpline(sketch, "E1136", {"points": [v(124.25, -37.6) * mm, v(124.76, -37.08) * mm, v(128.37, -36.9) * mm, v(130.25, -37.6) * mm]});
            skFitSpline(sketch, "E1137", {"points": [v(130.25, -37.6) * mm, v(131.8, -38.16) * mm, v(132.12, -40.8) * mm, v(133.75, -41.1) * mm]});
            skFitSpline(sketch, "E1138", {"points": [v(133.75, -41.1) * mm, v(139.17, -42.04) * mm, v(149.74, -41.6) * mm, v(150.25, -41.1) * mm]});
            skFitSpline(sketch, "E1139", {"points": [v(150.25, -41.1) * mm, v(150.76, -40.58) * mm, v(150.76, -38.1) * mm, v(150.25, -37.6) * mm]});
            skFitSpline(sketch, "E1140", {"points": [v(150.25, -37.6) * mm, v(149.74, -37.08) * mm, v(141.5, -38.39) * mm, v(137.25, -37.6) * mm]});
            skFitSpline(sketch, "E1141", {"points": [v(137.25, -37.6) * mm, v(135.86, -37.33) * mm, v(134.3, -35.67) * mm, v(134.25, -34.6) * mm]});
            skFitSpline(sketch, "E1142", {"points": [v(134.25, -34.6) * mm, v(134.2, -33.51) * mm, v(135.77, -31.5) * mm, v(137.25, -31.1) * mm]});
            skFitSpline(sketch, "E1143", {"points": [v(137.25, -31.1) * mm, v(140.3, -30.24) * mm, v(146.24, -30.58) * mm, v(146.75, -31.1) * mm]});
            skFitSpline(sketch, "E1144", {"points": [v(146.75, -31.1) * mm, v(147.26, -31.6) * mm, v(145.92, -33.77) * mm, v(146.75, -34.6) * mm]});
            skFitSpline(sketch, "E1145", {"points": [v(146.75, -34.6) * mm, v(147.57, -35.42) * mm, v(149.74, -35.1) * mm, v(150.25, -34.6) * mm]});
            skFitSpline(sketch, "E1146", {"points": [v(150.25, -34.6) * mm, v(150.76, -34.08) * mm, v(149.74, -31.6) * mm, v(150.25, -31.1) * mm]});
            skFitSpline(sketch, "E1147", {"points": [v(150.25, -31.1) * mm, v(150.76, -30.58) * mm, v(159.32, -31.9) * mm, v(163.75, -31.1) * mm]});
            skFitSpline(sketch, "E1148", {"points": [v(163.75, -31.1) * mm, v(165.14, -30.84) * mm, v(166.16, -29.37) * mm, v(166.75, -28.1) * mm]});
            skFitSpline(sketch, "E1149", {"points": [v(166.75, -28.1) * mm, v(167.24, -27.03) * mm, v(167.26, -25.1) * mm, v(166.75, -24.6) * mm]});
            skFitSpline(sketch, "E1150", {"points": [v(166.75, -24.6) * mm, v(166.24, -24.08) * mm, v(164.3, -24.07) * mm, v(163.25, -24.6) * mm]});
            skFitSpline(sketch, "E1151", {"points": [v(163.25, -24.6) * mm, v(161.77, -25.33) * mm, v(161.3, -27.52) * mm, v(159.75, -28.1) * mm]});
            skFitSpline(sketch, "E1152", {"points": [v(159.75, -28.1) * mm, v(157.87, -28.78) * mm, v(154.26, -28.6) * mm, v(153.75, -28.1) * mm]});
            skFitSpline(sketch, "E1153", {"points": [v(153.75, -28.1) * mm, v(153.24, -27.58) * mm, v(153.26, -25.65) * mm, v(153.75, -24.6) * mm]});
            skFitSpline(sketch, "E1154", {"points": [v(153.75, -24.6) * mm, v(154.34, -23.3) * mm, v(155.4, -22.02) * mm, v(156.75, -21.6) * mm]});
            skFitSpline(sketch, "E1155", {"points": [v(156.75, -21.6) * mm, v(158.82, -20.94) * mm, v(161.2, -22.3) * mm, v(163.25, -21.6) * mm]});
            skFitSpline(sketch, "E1156", {"points": [v(163.25, -21.6) * mm, v(164.8, -21.05) * mm, v(166.2, -19.65) * mm, v(166.75, -18.1) * mm]});
            skFitSpline(sketch, "E1157", {"points": [v(166.75, -18.1) * mm, v(167.47, -16.05) * mm, v(167.26, -12.1) * mm, v(166.75, -11.6) * mm]});
            skFitSpline(sketch, "E1158", {"points": [v(166.75, -11.6) * mm, v(166.24, -11.08) * mm, v(164.3, -11.07) * mm, v(163.25, -11.6) * mm]});
            skFitSpline(sketch, "E1159", {"points": [v(163.25, -11.6) * mm, v(159.82, -13.3) * mm, v(156.14, -15.1) * mm, v(153.75, -18.1) * mm]});
            skFitSpline(sketch, "E1160", {"points": [v(153.75, -18.1) * mm, v(151.53, -20.87) * mm, v(152, -26.74) * mm, v(150.07, -28.1) * mm]});
            skFitSpline(sketch, "E1161", {"points": [v(150.07, -28.1) * mm, v(148.13, -29.44) * mm, v(141.26, -28.6) * mm, v(140.75, -28.1) * mm]});
            skFitSpline(sketch, "E1162", {"points": [v(140.75, -28.1) * mm, v(140.24, -27.58) * mm, v(140.3, -25.66) * mm, v(140.75, -24.6) * mm]});
            skFitSpline(sketch, "E1163", {"points": [v(140.75, -24.6) * mm, v(141.36, -23.18) * mm, v(143.75, -22.63) * mm, v(143.75, -21.1) * mm]});
            skFitSpline(sketch, "E1164", {"points": [v(143.75, -21.1) * mm, v(143.75, -19.68) * mm, v(140.75, -18.82) * mm, v(140.75, -18.1) * mm]});
            skFitSpline(sketch, "E1165", {"points": [v(140.75, -18.1) * mm, v(140.75, -17.36) * mm, v(142.4, -15.52) * mm, v(143.75, -15.1) * mm]});
            skFitSpline(sketch, "E1166", {"points": [v(143.75, -15.1) * mm, v(145.82, -14.44) * mm, v(149.74, -15.6) * mm, v(150.25, -15.1) * mm]});
            skFitSpline(sketch, "E1167", {"points": [v(150.25, -15.1) * mm, v(150.76, -14.58) * mm, v(150.76, -12.1) * mm, v(150.25, -11.6) * mm]});
            skFitSpline(sketch, "E1168", {"points": [v(150.25, -11.6) * mm, v(149.74, -11.08) * mm, v(147.8, -12.08) * mm, v(146.75, -11.6) * mm]});
            skFitSpline(sketch, "E1169", {"points": [v(146.75, -11.6) * mm, v(145.47, -11) * mm, v(144.65, -8.6) * mm, v(143.75, -8.6) * mm]});
            skFitSpline(sketch, "E1170", {"points": [v(143.75, -8.6) * mm, v(142.85, -8.57) * mm, v(139.6, -13.67) * mm, v(136.75, -15.1) * mm]});
            skFitSpline(sketch, "E1171", {"points": [v(136.75, -15.1) * mm, v(134.96, -15.99) * mm, v(131.26, -14.58) * mm, v(130.75, -15.1) * mm]});
            skFitSpline(sketch, "E1172", {"points": [v(130.75, -15.1) * mm, v(130.24, -15.6) * mm, v(130.24, -17.58) * mm, v(130.75, -18.1) * mm]});
            skFitSpline(sketch, "E1173", {"points": [v(130.75, -18.1) * mm, v(131.26, -18.6) * mm, v(136.74, -17.58) * mm, v(137.25, -18.1) * mm]});
            skFitSpline(sketch, "E1174", {"points": [v(137.25, -18.1) * mm, v(137.76, -18.6) * mm, v(138.49, -24.68) * mm, v(137.25, -27.6) * mm]});
            skFitSpline(sketch, "E1175", {"points": [v(137.25, -27.6) * mm, v(135.96, -30.63) * mm, v(133.16, -33.04) * mm, v(130.25, -34.6) * mm]});
            skFitSpline(sketch, "E1176", {"points": [v(130.25, -34.6) * mm, v(128.44, -35.55) * mm, v(124.52, -35.18) * mm, v(124.1, -34.6) * mm]});
            skFitSpline(sketch, "E1177", {"points": [v(124.1, -34.6) * mm, v(123.66, -34) * mm, v(127.34, -28.09) * mm, v(127.25, -24.6) * mm]});
            skFitSpline(sketch, "E1178", {"points": [v(127.25, -24.6) * mm, v(127.2, -22.94) * mm, v(125.2, -21.87) * mm, v(123.75, -21.1) * mm]});
            skFitSpline(sketch, "E1179", {"points": [v(123.75, -21.1) * mm, v(122.87, -20.62) * mm, v(121.26, -20.58) * mm, v(120.75, -21.1) * mm]});
            skFitSpline(sketch, "E1180", {"points": [v(120.75, -21.1) * mm, v(120.24, -21.6) * mm, v(121.26, -34.08) * mm, v(120.75, -34.6) * mm]});
            skFitSpline(sketch, "E1181", {"points": [v(120.75, -34.6) * mm, v(120.24, -35.1) * mm, v(116.63, -35.28) * mm, v(114.75, -34.6) * mm]});
            skFitSpline(sketch, "E1182", {"points": [v(114.75, -34.6) * mm, v(113.2, -34.02) * mm, v(112.73, -31.83) * mm, v(111.25, -31.1) * mm]});
            skFitSpline(sketch, "E1183", {"points": [v(111.25, -31.1) * mm, v(110.2, -30.57) * mm, v(108.26, -30.58) * mm, v(107.75, -31.1) * mm]});
            skFitSpline(sketch, "E1184", {"points": [v(107.75, -31.1) * mm, v(107.24, -31.6) * mm, v(108.26, -43.58) * mm, v(107.75, -44.1) * mm]});
            skFitSpline(sketch, "E1185", {"points": [v(107.75, -44.1) * mm, v(107.24, -44.6) * mm, v(105.07, -43.27) * mm, v(104.25, -44.1) * mm]});
            skFitSpline(sketch, "E1186", {"points": [v(104.25, -44.1) * mm, v(103.42, -44.92) * mm, v(103.42, -46.77) * mm, v(104.25, -47.6) * mm]});
            skFitSpline(sketch, "E1187", {"points": [v(104.25, -47.6) * mm, v(105.07, -48.42) * mm, v(107.24, -47.08) * mm, v(107.75, -47.6) * mm]});
            skFitSpline(sketch, "E1188", {"points": [v(107.75, -47.6) * mm, v(108.26, -48.1) * mm, v(108.26, -53.58) * mm, v(107.75, -54.1) * mm]});
            skFitSpline(sketch, "E1189", {"points": [v(107.75, -54.1) * mm, v(107.24, -54.6) * mm, v(101.76, -54.6) * mm, v(101.25, -54.1) * mm]});
            skFitSpline(sketch, "E1190", {"points": [v(101.25, -54.1) * mm, v(100.74, -53.58) * mm, v(101.76, -48.1) * mm, v(101.25, -47.6) * mm]});
            skFitSpline(sketch, "E1191", {"points": [v(101.25, -47.6) * mm, v(100.74, -47.08) * mm, v(98.76, -47.08) * mm, v(98.25, -47.6) * mm]});
            skFitSpline(sketch, "E1192", {"points": [v(98.25, -47.6) * mm, v(97.74, -48.1) * mm, v(98.76, -50.08) * mm, v(98.25, -50.6) * mm]});
            skFitSpline(sketch, "E1193", {"points": [v(98.25, -50.6) * mm, v(97.74, -51.1) * mm, v(88.53, -51.26) * mm, v(88.25, -50.6) * mm]});
            skFitSpline(sketch, "E1194", {"points": [v(88.25, -50.6) * mm, v(87.97, -49.92) * mm, v(92.18, -45.76) * mm, v(94.75, -44.1) * mm]});
            skFitSpline(sketch, "E1195", {"points": [v(94.75, -44.1) * mm, v(95.73, -43.45) * mm, v(97.45, -44.94) * mm, v(98.25, -44.1) * mm]});
            skFitSpline(sketch, "E1196", {"points": [v(98.25, -44.1) * mm, v(99.1, -43.2) * mm, v(98.85, -40.82) * mm, v(98.25, -40.4) * mm]});
            skFitSpline(sketch, "E1197", {"points": [v(98.25, -40.4) * mm, v(97.65, -40) * mm, v(91.39, -42.42) * mm, v(88.25, -44.1) * mm]});
            skFitSpline(sketch, "E1198", {"points": [v(88.25, -44.1) * mm, v(86.8, -44.87) * mm, v(85.53, -46.14) * mm, v(84.75, -47.6) * mm]});
            skFitSpline(sketch, "E1199", {"points": [v(84.75, -47.6) * mm, v(84.28, -48.47) * mm, v(85.26, -50.08) * mm, v(84.75, -50.6) * mm]});
            skFitSpline(sketch, "E1200", {"points": [v(84.75, -50.6) * mm, v(84.24, -51.1) * mm, v(82.46, -51.3) * mm, v(81.75, -50.6) * mm]});
            skFitSpline(sketch, "E1201", {"points": [v(81.75, -50.6) * mm, v(81.04, -49.88) * mm, v(82.5, -48.24) * mm, v(81.75, -47.6) * mm]});
            skFitSpline(sketch, "E1202", {"points": [v(81.75, -47.6) * mm, v(80.86, -46.83) * mm, v(78.76, -47.08) * mm, v(78.25, -47.6) * mm]});
            skFitSpline(sketch, "E1203", {"points": [v(78.25, -47.6) * mm, v(77.74, -48.1) * mm, v(78.76, -53.58) * mm, v(78.25, -54.1) * mm]});
            skFitSpline(sketch, "E1204", {"points": [v(78.25, -54.1) * mm, v(77.74, -54.6) * mm, v(72.26, -54.6) * mm, v(71.75, -54.1) * mm]});
            skFitSpline(sketch, "E1205", {"points": [v(71.75, -54.1) * mm, v(71.24, -53.58) * mm, v(71.28, -51.97) * mm, v(71.75, -51.1) * mm]});
            skFitSpline(sketch, "E1206", {"points": [v(71.75, -51.1) * mm, v(72.53, -49.64) * mm, v(74.7, -49.15) * mm, v(75.25, -47.6) * mm]});
            skFitSpline(sketch, "E1207", {"points": [v(75.25, -47.6) * mm, v(75.97, -45.55) * mm, v(74.53, -43.14) * mm, v(75.25, -41.1) * mm]});
            skFitSpline(sketch, "E1208", {"points": [v(75.25, -41.1) * mm, v(75.8, -39.53) * mm, v(77.2, -38.14) * mm, v(78.75, -37.6) * mm]});
            skFitSpline(sketch, "E1209", {"points": [v(78.75, -37.6) * mm, v(80.8, -36.88) * mm, v(83.3, -38.53) * mm, v(85.25, -37.6) * mm]});
            skFitSpline(sketch, "E1210", {"points": [v(85.25, -37.6) * mm, v(87.8, -36.37) * mm, v(90.17, -31.63) * mm, v(91.25, -31.6) * mm]});
            skFitSpline(sketch, "E1211", {"points": [v(91.25, -31.6) * mm, v(92.33, -31.55) * mm, v(93.34, -33.99) * mm, v(94.75, -34.6) * mm]});
            skFitSpline(sketch, "E1212", {"points": [v(94.75, -34.6) * mm, v(95.82, -35.05) * mm, v(97.74, -35.1) * mm, v(98.25, -34.6) * mm]});
            skFitSpline(sketch, "E1213", {"points": [v(98.25, -34.6) * mm, v(98.76, -34.08) * mm, v(97.53, -32) * mm, v(98.25, -31.1) * mm]});
            skFitSpline(sketch, "E1214", {"points": [v(98.25, -31.1) * mm, v(102.04, -26.28) * mm, v(105.94, -21.16) * mm, v(111.25, -18.1) * mm]});
            skFitSpline(sketch, "E1215", {"points": [v(111.25, -18.1) * mm, v(114, -16.5) * mm, v(120.24, -18.6) * mm, v(120.75, -18.1) * mm]});
            skFitSpline(sketch, "E1216", {"points": [v(120.75, -18.1) * mm, v(121.26, -17.58) * mm, v(121.26, -15.6) * mm, v(120.75, -15.1) * mm]});
            skFitSpline(sketch, "E1217", {"points": [v(120.75, -15.1) * mm, v(120.24, -14.58) * mm, v(118.61, -15.6) * mm, v(117.75, -15.1) * mm]});
            skFitSpline(sketch, "E1218", {"points": [v(117.75, -15.1) * mm, v(116.42, -14.32) * mm, v(114.7, -12.67) * mm, v(114.75, -11.6) * mm]});
            skFitSpline(sketch, "E1219", {"points": [v(114.75, -11.6) * mm, v(114.8, -10.51) * mm, v(116.4, -9.02) * mm, v(117.75, -8.6) * mm]});
            skFitSpline(sketch, "E1220", {"points": [v(117.75, -8.6) * mm, v(119.82, -7.94) * mm, v(122.2, -9.3) * mm, v(124.25, -8.6) * mm]});
            skFitSpline(sketch, "E1221", {"points": [v(124.25, -8.6) * mm, v(125.8, -8.05) * mm, v(126.11, -5.29) * mm, v(127.75, -5.1) * mm]});
            skFitSpline(sketch, "E1222", {"points": [v(127.75, -5.1) * mm, v(136.36, -4.07) * mm, v(153.24, -4.58) * mm, v(153.75, -5.1) * mm]});
            skFitSpline(sketch, "E1223", {"points": [v(153.75, -5.1) * mm, v(154.26, -5.6) * mm, v(153, -7.7) * mm, v(153.75, -8.6) * mm]});
            skFitSpline(sketch, "E1224", {"points": [v(153.75, -8.6) * mm, v(154.4, -9.35) * mm, v(156.24, -9.1) * mm, v(156.75, -8.6) * mm]});
            skFitSpline(sketch, "E1225", {"points": [v(156.75, -8.6) * mm, v(157.26, -8.08) * mm, v(156.24, -5.6) * mm, v(156.75, -5.1) * mm]});
            skFitSpline(sketch, "E1226", {"points": [v(156.75, -5.1) * mm, v(157.26, -4.58) * mm, v(161.51, -5.76) * mm, v(163.75, -5.1) * mm]});
            skFitSpline(sketch, "E1227", {"points": [v(163.75, -5.1) * mm, v(165.1, -4.68) * mm, v(166.43, -3.47) * mm, v(166.75, -2.1) * mm]});
            skFitSpline(sketch, "E1228", {"points": [v(166.75, -2.1) * mm, v(167.5, 1.16) * mm, v(167.26, 7.4) * mm, v(166.75, 7.9) * mm]});
            skFitSpline(sketch, "E1229", {"points": [v(166.75, 7.9) * mm, v(166.24, 8.42) * mm, v(163.76, 8.42) * mm, v(163.25, 7.9) * mm]});
            skFitSpline(sketch, "E1230", {"points": [v(163.25, 7.9) * mm, v(162.74, 7.4) * mm, v(163.76, 1.92) * mm, v(163.25, 1.4) * mm]});
            skFitSpline(sketch, "E1231", {"points": [v(163.25, 1.4) * mm, v(162.74, 0.9) * mm, v(160.76, 0.9) * mm, v(160.25, 1.4) * mm]});
            skFitSpline(sketch, "E1232", {"points": [v(160.25, 1.4) * mm, v(159.74, 1.92) * mm, v(160.72, 3.53) * mm, v(160.25, 4.4) * mm]});
            skFitSpline(sketch, "E1233", {"points": [v(160.25, 4.4) * mm, v(159.47, 5.86) * mm, v(158.21, 7.14) * mm, v(156.75, 7.9) * mm]});
            skFitSpline(sketch, "E1234", {"points": [v(156.75, 7.9) * mm, v(155.81, 8.4) * mm, v(154, 8.5) * mm, v(153.57, 7.9) * mm]});
            skFitSpline(sketch, "E1235", {"points": [v(153.57, 7.9) * mm, v(153.15, 7.32) * mm, v(157.35, -1) * mm, v(156.93, -1.6) * mm]});
            skFitSpline(sketch, "E1236", {"points": [v(156.93, -1.6) * mm, v(156.5, -2.18) * mm, v(150.76, -2.1) * mm, v(150.25, -1.6) * mm]});
            skFitSpline(sketch, "E1237", {"points": [v(150.25, -1.6) * mm, v(149.74, -1.08) * mm, v(151, 0.76) * mm, v(150.25, 1.4) * mm]});
            skFitSpline(sketch, "E1238", {"points": [v(150.25, 1.4) * mm, v(149.36, 2.17) * mm, v(147.26, 1.92) * mm, v(146.75, 1.4) * mm]});
            skFitSpline(sketch, "E1239", {"points": [v(146.75, 1.4) * mm, v(146.24, 0.9) * mm, v(147.26, -1.08) * mm, v(146.75, -1.6) * mm]});
            skFitSpline(sketch, "E1240", {"points": [v(146.75, -1.6) * mm, v(146.24, -2.1) * mm, v(141.26, -2.1) * mm, v(140.75, -1.6) * mm]});
            skFitSpline(sketch, "E1241", {"points": [v(140.75, -1.6) * mm, v(140.24, -1.08) * mm, v(141.26, 7.4) * mm, v(140.75, 7.9) * mm]});
            skFitSpline(sketch, "E1242", {"points": [v(140.75, 7.9) * mm, v(140.24, 8.42) * mm, v(137.76, 8.42) * mm, v(137.25, 7.9) * mm]});
            skFitSpline(sketch, "E1243", {"points": [v(137.25, 7.9) * mm, v(136.74, 7.4) * mm, v(137.76, -1.08) * mm, v(137.25, -1.6) * mm]});
            skFitSpline(sketch, "E1244", {"points": [v(137.25, -1.6) * mm, v(136.74, -2.1) * mm, v(134.64, -2.35) * mm, v(133.75, -1.6) * mm]});
            skFitSpline(sketch, "E1245", {"points": [v(133.75, -1.6) * mm, v(133, -0.94) * mm, v(134.46, 0.7) * mm, v(133.75, 1.4) * mm]});
            skFitSpline(sketch, "E1246", {"points": [v(133.75, 1.4) * mm, v(133.04, 2.12) * mm, v(131.26, 1.92) * mm, v(130.75, 1.4) * mm]});
            skFitSpline(sketch, "E1247", {"points": [v(130.75, 1.4) * mm, v(130.24, 0.9) * mm, v(131.26, -1.08) * mm, v(130.75, -1.6) * mm]});
            skFitSpline(sketch, "E1248", {"points": [v(130.75, -1.6) * mm, v(130.24, -2.1) * mm, v(124.76, -2.1) * mm, v(124.25, -1.6) * mm]});
            skFitSpline(sketch, "E1249", {"points": [v(124.25, -1.6) * mm, v(123.74, -1.08) * mm, v(123.51, 4.83) * mm, v(124.25, 7.9) * mm]});
            skFitSpline(sketch, "E1250", {"points": [v(124.25, 7.9) * mm, v(124.58, 9.28) * mm, v(125.84, 10.8) * mm, v(127.25, 10.9) * mm]});
            skFitSpline(sketch, "E1251", {"points": [v(127.25, 10.9) * mm, v(139.38, 11.83) * mm, v(151.62, 9.99) * mm, v(163.75, 10.9) * mm]});
            skFitSpline(sketch, "E1252", {"points": [v(163.75, 10.9) * mm, v(165.16, 11.02) * mm, v(166.43, 12.53) * mm, v(166.75, 13.9) * mm]});
            skFitSpline(sketch, "E1253", {"points": [v(166.75, 13.9) * mm, v(167.5, 17.16) * mm, v(167.59, 20.68) * mm, v(166.75, 23.9) * mm]});
            skFitSpline(sketch, "E1254", {"points": [v(166.75, 23.9) * mm, v(166.34, 25.5) * mm, v(164.8, 26.86) * mm, v(163.25, 27.4) * mm]});
            skFitSpline(sketch, "E1255", {"points": [v(163.25, 27.4) * mm, v(161.2, 28.12) * mm, v(158.82, 28.06) * mm, v(156.75, 27.4) * mm]});
            skFitSpline(sketch, "E1256", {"points": [v(156.75, 27.4) * mm, v(155.4, 26.98) * mm, v(154.07, 25.79) * mm, v(153.75, 24.4) * mm]});
            skFitSpline(sketch, "E1257", {"points": [v(153.75, 24.4) * mm, v(153, 21.16) * mm, v(154.26, 14.92) * mm, v(153.75, 14.4) * mm]});
            skFitSpline(sketch, "E1258", {"points": [v(153.75, 14.4) * mm, v(153.24, 13.9) * mm, v(141.26, 13.9) * mm, v(140.75, 14.4) * mm]});
            skFitSpline(sketch, "E1259", {"points": [v(140.75, 14.4) * mm, v(140.24, 14.92) * mm, v(140.24, 23.4) * mm, v(140.75, 23.9) * mm]});
            skFitSpline(sketch, "E1260", {"points": [v(140.75, 23.9) * mm, v(141.26, 24.42) * mm, v(145.31, 22.94) * mm, v(147.25, 23.9) * mm]});
            skFitSpline(sketch, "E1261", {"points": [v(147.25, 23.9) * mm, v(150, 25.28) * mm, v(150.84, 29.44) * mm, v(153.75, 30.4) * mm]});
            skFitSpline(sketch, "E1262", {"points": [v(153.75, 30.4) * mm, v(157.86, 31.78) * mm, v(166.24, 29.9) * mm, v(166.75, 30.4) * mm]});
            skFitSpline(sketch, "E1263", {"points": [v(166.75, 30.4) * mm, v(167.26, 30.92) * mm, v(166.75, 32.74) * mm, v(166.75, 33.9) * mm]});
            skFitSpline(sketch, "E1264", {"points": [v(166.75, 30.4) * mm, v(166.75, 31.58) * mm, v(166.75, 32.74) * mm, v(166.75, 33.9) * mm]});
            skFitSpline(sketch, "E1265", {"points": [v(111.25, 1.4) * mm, v(110.13, 1.08) * mm, v(108.64, 0.65) * mm, v(107.75, 1.4) * mm]});
            skFitSpline(sketch, "E1266", {"points": [v(107.75, 1.4) * mm, v(107, 2.06) * mm, v(107.24, 3.9) * mm, v(107.75, 4.4) * mm]});
            skFitSpline(sketch, "E1267", {"points": [v(107.75, 4.4) * mm, v(108.26, 4.92) * mm, v(110.74, 3.9) * mm, v(111.25, 4.4) * mm]});
            skFitSpline(sketch, "E1268", {"points": [v(111.25, 4.4) * mm, v(111.76, 4.92) * mm, v(110.74, 7.4) * mm, v(111.25, 7.9) * mm]});
            skFitSpline(sketch, "E1269", {"points": [v(111.25, 7.9) * mm, v(111.76, 8.42) * mm, v(113.74, 8.42) * mm, v(114.25, 7.9) * mm]});
            skFitSpline(sketch, "E1270", {"points": [v(114.25, 7.9) * mm, v(114.76, 7.4) * mm, v(113.74, -1.08) * mm, v(114.25, -1.6) * mm]});
            skFitSpline(sketch, "E1271", {"points": [v(114.25, -1.6) * mm, v(114.76, -2.1) * mm, v(120.24, -2.1) * mm, v(120.75, -1.6) * mm]});
            skFitSpline(sketch, "E1272", {"points": [v(120.75, -1.6) * mm, v(121.26, -1.08) * mm, v(120.24, 20.4) * mm, v(120.75, 20.9) * mm]});
            skFitSpline(sketch, "E1273", {"points": [v(120.75, 20.9) * mm, v(121.26, 21.42) * mm, v(123.74, 21.42) * mm, v(124.25, 20.9) * mm]});
            skFitSpline(sketch, "E1274", {"points": [v(124.25, 20.9) * mm, v(124.76, 20.4) * mm, v(123.76, 18.47) * mm, v(124.25, 17.4) * mm]});
            skFitSpline(sketch, "E1275", {"points": [v(124.25, 17.4) * mm, v(124.84, 16.13) * mm, v(125.87, 14.73) * mm, v(127.25, 14.4) * mm]});
            skFitSpline(sketch, "E1276", {"points": [v(127.25, 14.4) * mm, v(130.5, 13.66) * mm, v(136.74, 13.9) * mm, v(137.25, 14.4) * mm]});
            skFitSpline(sketch, "E1277", {"points": [v(137.25, 14.4) * mm, v(137.76, 14.92) * mm, v(137.76, 20.4) * mm, v(137.25, 20.9) * mm]});
            skFitSpline(sketch, "E1278", {"points": [v(137.25, 20.9) * mm, v(136.74, 21.42) * mm, v(127.76, 20.4) * mm, v(127.25, 20.9) * mm]});
            skFitSpline(sketch, "E1279", {"points": [v(127.25, 20.9) * mm, v(126.74, 21.42) * mm, v(126.74, 23.4) * mm, v(127.25, 23.9) * mm]});
            skFitSpline(sketch, "E1280", {"points": [v(127.25, 23.9) * mm, v(127.76, 24.42) * mm, v(131.81, 22.94) * mm, v(133.75, 23.9) * mm]});
            skFitSpline(sketch, "E1281", {"points": [v(133.75, 23.9) * mm, v(136.5, 25.28) * mm, v(137.72, 28.68) * mm, v(140.25, 30.4) * mm]});
            skFitSpline(sketch, "E1282", {"points": [v(140.25, 30.4) * mm, v(141.08, 30.97) * mm, v(142.36, 29.96) * mm, v(143.25, 30.4) * mm]});
            skFitSpline(sketch, "E1283", {"points": [v(143.25, 30.4) * mm, v(144.83, 31.2) * mm, v(145.5, 33.65) * mm, v(147.25, 33.9) * mm]});
            skFitSpline(sketch, "E1284", {"points": [v(147.25, 33.9) * mm, v(153.68, 34.87) * mm, v(160.27, 34.38) * mm, v(166.75, 33.9) * mm]});
            skFitSpline(sketch, "E1285", {"points": [v(-104.25, 26.9) * mm, v(-104.76, 26.4) * mm, v(-104.85, 24.7) * mm, v(-104.25, 23.9) * mm]});
            skFitSpline(sketch, "E1286", {"points": [v(-104.25, 23.9) * mm, v(-101.54, 20.34) * mm, v(-98.78, 16.37) * mm, v(-94.75, 14.4) * mm]});
            skFitSpline(sketch, "E1287", {"points": [v(-94.75, 14.4) * mm, v(-91.75, 12.95) * mm, v(-85.26, 13.9) * mm, v(-84.75, 14.4) * mm]});
            skFitSpline(sketch, "E1288", {"points": [v(-84.75, 14.4) * mm, v(-84.24, 14.92) * mm, v(-84.06, 18.53) * mm, v(-84.75, 20.4) * mm]});
            skFitSpline(sketch, "E1289", {"points": [v(-84.75, 20.4) * mm, v(-85.32, 21.96) * mm, v(-87.47, 22.46) * mm, v(-88.25, 23.9) * mm]});
            skFitSpline(sketch, "E1290", {"points": [v(-88.25, 23.9) * mm, v(-88.72, 24.79) * mm, v(-87.74, 26.4) * mm, v(-88.25, 26.9) * mm]});
            skFitSpline(sketch, "E1291", {"points": [v(-88.25, 26.9) * mm, v(-88.76, 27.42) * mm, v(-103.74, 27.42) * mm, v(-104.25, 26.9) * mm]});
            skFitSpline(sketch, "E1292", {"points": [v(-45.75, 26.9) * mm, v(-46.26, 26.4) * mm, v(-46.24, 25.08) * mm, v(-45.75, 24.4) * mm]});
            skFitSpline(sketch, "E1293", {"points": [v(-45.75, 24.4) * mm, v(-43.8, 21.75) * mm, v(-41.79, 18.7) * mm, v(-38.75, 17.4) * mm]});
            skFitSpline(sketch, "E1294", {"points": [v(-38.75, 17.4) * mm, v(-35.83, 16.17) * mm, v(-29.76, 17.92) * mm, v(-29.25, 17.4) * mm]});
            skFitSpline(sketch, "E1295", {"points": [v(-29.25, 17.4) * mm, v(-28.74, 16.9) * mm, v(-28.74, 14.92) * mm, v(-29.25, 14.4) * mm]});
            skFitSpline(sketch, "E1296", {"points": [v(-29.25, 14.4) * mm, v(-29.76, 13.9) * mm, v(-35.24, 14.92) * mm, v(-35.75, 14.4) * mm]});
            skFitSpline(sketch, "E1297", {"points": [v(-35.75, 14.4) * mm, v(-36.26, 13.9) * mm, v(-36.26, 8.42) * mm, v(-35.75, 7.9) * mm]});
            skFitSpline(sketch, "E1298", {"points": [v(-35.75, 7.9) * mm, v(-35.24, 7.4) * mm, v(-29.76, 8.42) * mm, v(-29.25, 7.9) * mm]});
            skFitSpline(sketch, "E1299", {"points": [v(-29.25, 7.9) * mm, v(-28.74, 7.4) * mm, v(-28.74, 4.92) * mm, v(-29.25, 4.4) * mm]});
            skFitSpline(sketch, "E1300", {"points": [v(-29.25, 4.4) * mm, v(-29.76, 3.9) * mm, v(-35.24, 4.92) * mm, v(-35.75, 4.4) * mm]});
            skFitSpline(sketch, "E1301", {"points": [v(-35.75, 4.4) * mm, v(-36.26, 3.9) * mm, v(-36.57, -2.03) * mm, v(-35.75, -5.1) * mm]});
            skFitSpline(sketch, "E1302", {"points": [v(-35.75, -5.1) * mm, v(-35.32, -6.68) * mm, v(-33.7, -7.8) * mm, v(-32.25, -8.6) * mm]});
            skFitSpline(sketch, "E1303", {"points": [v(-32.25, -8.6) * mm, v(-31.37, -9.06) * mm, v(-30.08, -8.03) * mm, v(-29.25, -8.6) * mm]});
            skFitSpline(sketch, "E1304", {"points": [v(-29.25, -8.6) * mm, v(-26.72, -10.32) * mm, v(-25.28, -13.36) * mm, v(-22.75, -15.1) * mm]});
            skFitSpline(sketch, "E1305", {"points": [v(-22.75, -15.1) * mm, v(-21.92, -15.66) * mm, v(-20.26, -15.6) * mm, v(-19.75, -15.1) * mm]});
            skFitSpline(sketch, "E1306", {"points": [v(-19.75, -15.1) * mm, v(-19.24, -14.58) * mm, v(-19.24, -2.6) * mm, v(-19.75, -2.1) * mm]});
            skFitSpline(sketch, "E1307", {"points": [v(-19.75, -2.1) * mm, v(-20.26, -1.58) * mm, v(-28.74, -2.6) * mm, v(-29.25, -2.1) * mm]});
            skFitSpline(sketch, "E1308", {"points": [v(-29.25, -2.1) * mm, v(-29.76, -1.58) * mm, v(-29.76, 0.9) * mm, v(-29.25, 1.4) * mm]});
            skFitSpline(sketch, "E1309", {"points": [v(-29.25, 1.4) * mm, v(-28.74, 1.92) * mm, v(-24.4, -0.08) * mm, v(-22.92, 1.4) * mm]});
            skFitSpline(sketch, "E1310", {"points": [v(-22.92, 1.4) * mm, v(-20.56, 3.77) * mm, v(-19.8, 7.57) * mm, v(-19.75, 10.9) * mm]});
            skFitSpline(sketch, "E1311", {"points": [v(-19.75, 10.9) * mm, v(-19.73, 12.32) * mm, v(-22.16, 12.63) * mm, v(-22.75, 13.9) * mm]});
            skFitSpline(sketch, "E1312", {"points": [v(-22.75, 13.9) * mm, v(-23.24, 14.97) * mm, v(-23.26, 16.9) * mm, v(-22.75, 17.4) * mm]});
            skFitSpline(sketch, "E1313", {"points": [v(-22.75, 17.4) * mm, v(-22.24, 17.92) * mm, v(-16.76, 16.9) * mm, v(-16.25, 17.4) * mm]});
            skFitSpline(sketch, "E1314", {"points": [v(-16.25, 17.4) * mm, v(-15.74, 17.92) * mm, v(-15.6, 21.84) * mm, v(-16.25, 23.9) * mm]});
            skFitSpline(sketch, "E1315", {"points": [v(-16.25, 23.9) * mm, v(-16.68, 25.26) * mm, v(-17.9, 26.5) * mm, v(-19.25, 26.9) * mm]});
            skFitSpline(sketch, "E1316", {"points": [v(-19.25, 26.9) * mm, v(-21.48, 27.58) * mm, v(-24.02, 27.58) * mm, v(-26.25, 26.9) * mm]});
            skFitSpline(sketch, "E1317", {"points": [v(-26.25, 26.9) * mm, v(-27.6, 26.5) * mm, v(-27.97, 24.5) * mm, v(-29.25, 23.9) * mm]});
            skFitSpline(sketch, "E1318", {"points": [v(-29.25, 23.9) * mm, v(-30.3, 23.42) * mm, v(-31.7, 23.42) * mm, v(-32.75, 23.9) * mm]});
            skFitSpline(sketch, "E1319", {"points": [v(-32.75, 23.9) * mm, v(-34.03, 24.5) * mm, v(-34.37, 26.6) * mm, v(-35.75, 26.9) * mm]});
            skFitSpline(sketch, "E1320", {"points": [v(-35.75, 26.9) * mm, v(-39, 27.66) * mm, v(-45.24, 27.42) * mm, v(-45.75, 26.9) * mm]});
            skFitSpline(sketch, "E1321", {"points": [v(45.75, 26.9) * mm, v(46.26, 26.4) * mm, v(46.24, 25.08) * mm, v(45.75, 24.4) * mm]});
            skFitSpline(sketch, "E1322", {"points": [v(45.75, 24.4) * mm, v(43.8, 21.75) * mm, v(41.79, 18.7) * mm, v(38.75, 17.4) * mm]});
            skFitSpline(sketch, "E1323", {"points": [v(38.75, 17.4) * mm, v(35.83, 16.17) * mm, v(29.76, 17.92) * mm, v(29.25, 17.4) * mm]});
            skFitSpline(sketch, "E1324", {"points": [v(29.25, 17.4) * mm, v(28.74, 16.9) * mm, v(28.74, 14.92) * mm, v(29.25, 14.4) * mm]});
            skFitSpline(sketch, "E1325", {"points": [v(29.25, 14.4) * mm, v(29.76, 13.9) * mm, v(35.24, 14.92) * mm, v(35.75, 14.4) * mm]});
            skFitSpline(sketch, "E1326", {"points": [v(35.75, 14.4) * mm, v(36.26, 13.9) * mm, v(36.26, 8.42) * mm, v(35.75, 7.9) * mm]});
            skFitSpline(sketch, "E1327", {"points": [v(35.75, 7.9) * mm, v(35.24, 7.4) * mm, v(29.76, 8.42) * mm, v(29.25, 7.9) * mm]});
            skFitSpline(sketch, "E1328", {"points": [v(29.25, 7.9) * mm, v(28.74, 7.4) * mm, v(28.74, 4.92) * mm, v(29.25, 4.4) * mm]});
            skFitSpline(sketch, "E1329", {"points": [v(29.25, 4.4) * mm, v(29.76, 3.9) * mm, v(35.24, 4.92) * mm, v(35.75, 4.4) * mm]});
            skFitSpline(sketch, "E1330", {"points": [v(35.75, 4.4) * mm, v(36.26, 3.9) * mm, v(36.57, -2.03) * mm, v(35.75, -5.1) * mm]});
            skFitSpline(sketch, "E1331", {"points": [v(35.75, -5.1) * mm, v(35.32, -6.68) * mm, v(33.7, -7.8) * mm, v(32.25, -8.6) * mm]});
            skFitSpline(sketch, "E1332", {"points": [v(32.25, -8.6) * mm, v(31.37, -9.06) * mm, v(30.08, -8.03) * mm, v(29.25, -8.6) * mm]});
            skFitSpline(sketch, "E1333", {"points": [v(29.25, -8.6) * mm, v(26.72, -10.32) * mm, v(25.28, -13.36) * mm, v(22.75, -15.1) * mm]});
            skFitSpline(sketch, "E1334", {"points": [v(22.75, -15.1) * mm, v(21.92, -15.66) * mm, v(20.26, -15.6) * mm, v(19.75, -15.1) * mm]});
            skFitSpline(sketch, "E1335", {"points": [v(19.75, -15.1) * mm, v(19.24, -14.58) * mm, v(19.24, -2.6) * mm, v(19.75, -2.1) * mm]});
            skFitSpline(sketch, "E1336", {"points": [v(19.75, -2.1) * mm, v(20.26, -1.58) * mm, v(28.74, -2.6) * mm, v(29.25, -2.1) * mm]});
            skFitSpline(sketch, "E1337", {"points": [v(29.25, -2.1) * mm, v(29.76, -1.58) * mm, v(29.76, 0.9) * mm, v(29.25, 1.4) * mm]});
            skFitSpline(sketch, "E1338", {"points": [v(29.25, 1.4) * mm, v(28.74, 1.92) * mm, v(24.4, -0.08) * mm, v(22.92, 1.4) * mm]});
            skFitSpline(sketch, "E1339", {"points": [v(22.92, 1.4) * mm, v(20.56, 3.77) * mm, v(19.8, 7.57) * mm, v(19.75, 10.9) * mm]});
            skFitSpline(sketch, "E1340", {"points": [v(19.75, 10.9) * mm, v(19.73, 12.32) * mm, v(22.16, 12.63) * mm, v(22.75, 13.9) * mm]});
            skFitSpline(sketch, "E1341", {"points": [v(22.75, 13.9) * mm, v(23.24, 14.97) * mm, v(23.26, 16.9) * mm, v(22.75, 17.4) * mm]});
            skFitSpline(sketch, "E1342", {"points": [v(22.75, 17.4) * mm, v(22.24, 17.92) * mm, v(16.76, 16.9) * mm, v(16.25, 17.4) * mm]});
            skFitSpline(sketch, "E1343", {"points": [v(16.25, 17.4) * mm, v(15.74, 17.92) * mm, v(15.6, 21.84) * mm, v(16.25, 23.9) * mm]});
            skFitSpline(sketch, "E1344", {"points": [v(16.25, 23.9) * mm, v(16.68, 25.26) * mm, v(17.9, 26.5) * mm, v(19.25, 26.9) * mm]});
            skFitSpline(sketch, "E1345", {"points": [v(19.25, 26.9) * mm, v(21.48, 27.58) * mm, v(24.02, 27.58) * mm, v(26.25, 26.9) * mm]});
            skFitSpline(sketch, "E1346", {"points": [v(26.25, 26.9) * mm, v(27.6, 26.5) * mm, v(27.97, 24.5) * mm, v(29.25, 23.9) * mm]});
            skFitSpline(sketch, "E1347", {"points": [v(29.25, 23.9) * mm, v(30.3, 23.42) * mm, v(31.7, 23.42) * mm, v(32.75, 23.9) * mm]});
            skFitSpline(sketch, "E1348", {"points": [v(32.75, 23.9) * mm, v(34.03, 24.5) * mm, v(34.37, 26.6) * mm, v(35.75, 26.9) * mm]});
            skFitSpline(sketch, "E1349", {"points": [v(35.75, 26.9) * mm, v(39, 27.66) * mm, v(45.24, 27.42) * mm, v(45.75, 26.9) * mm]});
            skFitSpline(sketch, "E1350", {"points": [v(88.25, 26.9) * mm, v(87.74, 26.4) * mm, v(88.72, 24.79) * mm, v(88.25, 23.9) * mm]});
            skFitSpline(sketch, "E1351", {"points": [v(88.25, 23.9) * mm, v(87.47, 22.46) * mm, v(85.32, 21.96) * mm, v(84.75, 20.4) * mm]});
            skFitSpline(sketch, "E1352", {"points": [v(84.75, 20.4) * mm, v(84.06, 18.53) * mm, v(84.24, 14.92) * mm, v(84.75, 14.4) * mm]});
            skFitSpline(sketch, "E1353", {"points": [v(84.75, 14.4) * mm, v(85.26, 13.9) * mm, v(91.75, 12.95) * mm, v(94.75, 14.4) * mm]});
            skFitSpline(sketch, "E1354", {"points": [v(94.75, 14.4) * mm, v(98.78, 16.37) * mm, v(101.54, 20.34) * mm, v(104.25, 23.9) * mm]});
            skFitSpline(sketch, "E1355", {"points": [v(104.25, 23.9) * mm, v(104.85, 24.7) * mm, v(104.76, 26.4) * mm, v(104.25, 26.9) * mm]});
            skFitSpline(sketch, "E1356", {"points": [v(104.25, 26.9) * mm, v(103.74, 27.42) * mm, v(88.76, 27.42) * mm, v(88.25, 26.9) * mm]});
            skFitSpline(sketch, "E1357", {"points": [v(-163.25, 20.9) * mm, v(-163.76, 20.4) * mm, v(-163.74, 18.47) * mm, v(-163.25, 17.4) * mm]});
            skFitSpline(sketch, "E1358", {"points": [v(-163.25, 17.4) * mm, v(-162.66, 16.13) * mm, v(-161.53, 15) * mm, v(-160.25, 14.4) * mm]});
            skFitSpline(sketch, "E1359", {"points": [v(-160.25, 14.4) * mm, v(-159.2, 13.92) * mm, v(-157.26, 13.9) * mm, v(-156.75, 14.4) * mm]});
            skFitSpline(sketch, "E1360", {"points": [v(-156.75, 14.4) * mm, v(-156.24, 14.92) * mm, v(-156.24, 20.4) * mm, v(-156.75, 20.9) * mm]});
            skFitSpline(sketch, "E1361", {"points": [v(-156.75, 20.9) * mm, v(-157.26, 21.42) * mm, v(-162.74, 21.42) * mm, v(-163.25, 20.9) * mm]});
            skFitSpline(sketch, "E1362", {"points": [v(156.75, 20.9) * mm, v(156.24, 20.4) * mm, v(156.24, 14.92) * mm, v(156.75, 14.4) * mm]});
            skFitSpline(sketch, "E1363", {"points": [v(156.75, 14.4) * mm, v(157.26, 13.9) * mm, v(159.2, 13.92) * mm, v(160.25, 14.4) * mm]});
            skFitSpline(sketch, "E1364", {"points": [v(160.25, 14.4) * mm, v(161.53, 15) * mm, v(162.66, 16.13) * mm, v(163.25, 17.4) * mm]});
            skFitSpline(sketch, "E1365", {"points": [v(163.25, 17.4) * mm, v(163.74, 18.47) * mm, v(163.76, 20.4) * mm, v(163.25, 20.9) * mm]});
            skFitSpline(sketch, "E1366", {"points": [v(163.25, 20.9) * mm, v(162.74, 21.42) * mm, v(157.26, 21.42) * mm, v(156.75, 20.9) * mm]});
            skFitSpline(sketch, "E1367", {"points": [v(-9.75, 7.4) * mm, v(-10.26, 6.9) * mm, v(-10.26, -30.58) * mm, v(-9.75, -31.1) * mm]});
            skFitSpline(sketch, "E1368", {"points": [v(-9.75, -31.1) * mm, v(-9.24, -31.6) * mm, v(-7.63, -31.56) * mm, v(-6.75, -31.1) * mm]});
            skFitSpline(sketch, "E1369", {"points": [v(-6.75, -31.1) * mm, v(-5.3, -30.3) * mm, v(-3.41, -29.23) * mm, v(-3.25, -27.6) * mm]});
            skFitSpline(sketch, "E1370", {"points": [v(-3.25, -27.6) * mm, v(-2.2, -16.98) * mm, v(-2.34, -6.22) * mm, v(-3.25, 4.4) * mm]});
            skFitSpline(sketch, "E1371", {"points": [v(-3.25, 4.4) * mm, v(-3.37, 5.82) * mm, v(-4.97, 6.82) * mm, v(-6.25, 7.4) * mm]});
            skFitSpline(sketch, "E1372", {"points": [v(-6.25, 7.4) * mm, v(-7.3, 7.9) * mm, v(-9.24, 7.92) * mm, v(-9.75, 7.4) * mm]});
            skFitSpline(sketch, "E1373", {"points": [v(9.75, 7.4) * mm, v(10.26, 6.9) * mm, v(10.26, -30.58) * mm, v(9.75, -31.1) * mm]});
            skFitSpline(sketch, "E1374", {"points": [v(9.75, -31.1) * mm, v(9.24, -31.6) * mm, v(7.63, -31.56) * mm, v(6.75, -31.1) * mm]});
            skFitSpline(sketch, "E1375", {"points": [v(6.75, -31.1) * mm, v(5.3, -30.3) * mm, v(3.41, -29.23) * mm, v(3.25, -27.6) * mm]});
            skFitSpline(sketch, "E1376", {"points": [v(3.25, -27.6) * mm, v(2.2, -16.98) * mm, v(2.34, -6.22) * mm, v(3.25, 4.4) * mm]});
            skFitSpline(sketch, "E1377", {"points": [v(3.25, 4.4) * mm, v(3.37, 5.82) * mm, v(4.97, 6.82) * mm, v(6.25, 7.4) * mm]});
            skFitSpline(sketch, "E1378", {"points": [v(6.25, 7.4) * mm, v(7.3, 7.9) * mm, v(9.24, 7.92) * mm, v(9.75, 7.4) * mm]});
            skFitSpline(sketch, "E1379", {"points": [v(-111.25, -5.1) * mm, v(-111.76, -5.6) * mm, v(-111.76, -14.58) * mm, v(-111.25, -15.1) * mm]});
            skFitSpline(sketch, "E1380", {"points": [v(-111.25, -15.1) * mm, v(-110.74, -15.6) * mm, v(-104.72, -15.62) * mm, v(-104.22, -15.1) * mm]});
            skFitSpline(sketch, "E1381", {"points": [v(-104.22, -15.1) * mm, v(-103.72, -14.56) * mm, v(-104.06, -5.77) * mm, v(-104.78, -5.1) * mm]});
            skFitSpline(sketch, "E1382", {"points": [v(-104.78, -5.1) * mm, v(-105.5, -4.42) * mm, v(-110.74, -4.58) * mm, v(-111.25, -5.1) * mm]});
            skFitSpline(sketch, "E1383", {"points": [v(111.25, -5.1) * mm, v(111.76, -5.6) * mm, v(111.76, -14.58) * mm, v(111.25, -15.1) * mm]});
            skFitSpline(sketch, "E1384", {"points": [v(111.25, -15.1) * mm, v(110.74, -15.6) * mm, v(104.72, -15.62) * mm, v(104.22, -15.1) * mm]});
            skFitSpline(sketch, "E1385", {"points": [v(104.22, -15.1) * mm, v(103.72, -14.56) * mm, v(104.06, -5.77) * mm, v(104.78, -5.1) * mm]});
            skFitSpline(sketch, "E1386", {"points": [v(104.78, -5.1) * mm, v(105.5, -4.42) * mm, v(110.74, -4.58) * mm, v(111.25, -5.1) * mm]});
            skFitSpline(sketch, "E1387", {"points": [v(-61.75, -11.6) * mm, v(-62.26, -12.1) * mm, v(-62.26, -17.58) * mm, v(-61.75, -18.1) * mm]});
            skFitSpline(sketch, "E1388", {"points": [v(-61.75, -18.1) * mm, v(-61.24, -18.6) * mm, v(-55.76, -18.6) * mm, v(-55.25, -18.1) * mm]});
            skFitSpline(sketch, "E1389", {"points": [v(-55.25, -18.1) * mm, v(-54.74, -17.58) * mm, v(-54.81, -16.3) * mm, v(-55.25, -15.6) * mm]});
            skFitSpline(sketch, "E1390", {"points": [v(-55.25, -15.6) * mm, v(-56.24, -13.98) * mm, v(-57.64, -12.58) * mm, v(-59.25, -11.6) * mm]});
            skFitSpline(sketch, "E1391", {"points": [v(-59.25, -11.6) * mm, v(-59.96, -11.15) * mm, v(-61.24, -11.08) * mm, v(-61.75, -11.6) * mm]});
            skFitSpline(sketch, "E1392", {"points": [v(61.75, -11.6) * mm, v(62.26, -12.1) * mm, v(62.26, -17.58) * mm, v(61.75, -18.1) * mm]});
            skFitSpline(sketch, "E1393", {"points": [v(61.75, -18.1) * mm, v(61.24, -18.6) * mm, v(55.76, -18.6) * mm, v(55.25, -18.1) * mm]});
            skFitSpline(sketch, "E1394", {"points": [v(55.25, -18.1) * mm, v(54.74, -17.58) * mm, v(54.81, -16.3) * mm, v(55.25, -15.6) * mm]});
            skFitSpline(sketch, "E1395", {"points": [v(55.25, -15.6) * mm, v(56.24, -13.98) * mm, v(57.64, -12.58) * mm, v(59.25, -11.6) * mm]});
            skFitSpline(sketch, "E1396", {"points": [v(59.25, -11.6) * mm, v(59.96, -11.15) * mm, v(61.24, -11.08) * mm, v(61.75, -11.6) * mm]});
            skFitSpline(sketch, "E1397", {"points": [v(-101.25, -15.1) * mm, v(-101.76, -15.6) * mm, v(-101.94, -19.21) * mm, v(-101.25, -21.1) * mm]});
            skFitSpline(sketch, "E1398", {"points": [v(-101.25, -21.1) * mm, v(-100.68, -22.64) * mm, v(-99.3, -24.05) * mm, v(-97.75, -24.6) * mm]});
            skFitSpline(sketch, "E1399", {"points": [v(-97.75, -24.6) * mm, v(-95.66, -25.31) * mm, v(-91.54, -25.17) * mm, v(-91.1, -24.6) * mm]});
            skFitSpline(sketch, "E1400", {"points": [v(-91.1, -24.6) * mm, v(-90.67, -24.01) * mm, v(-91.42, -21.7) * mm, v(-92.25, -20.6) * mm]});
            skFitSpline(sketch, "E1401", {"points": [v(-92.25, -20.6) * mm, v(-93.88, -18.42) * mm, v(-95.93, -16.5) * mm, v(-98.25, -15.1) * mm]});
            skFitSpline(sketch, "E1402", {"points": [v(-98.25, -15.1) * mm, v(-99.1, -14.57) * mm, v(-100.74, -14.58) * mm, v(-101.25, -15.1) * mm]});
            skFitSpline(sketch, "E1403", {"points": [v(32.75, -15.1) * mm, v(33.26, -15.6) * mm, v(33.26, -24.08) * mm, v(32.75, -24.6) * mm]});
            skFitSpline(sketch, "E1404", {"points": [v(32.75, -24.6) * mm, v(32.24, -25.1) * mm, v(26.76, -25.1) * mm, v(26.25, -24.6) * mm]});
            skFitSpline(sketch, "E1405", {"points": [v(26.25, -24.6) * mm, v(25.74, -24.08) * mm, v(25.6, -20.16) * mm, v(26.25, -18.1) * mm]});
            skFitSpline(sketch, "E1406", {"points": [v(26.25, -18.1) * mm, v(26.68, -16.74) * mm, v(27.97, -15.68) * mm, v(29.25, -15.1) * mm]});
            skFitSpline(sketch, "E1407", {"points": [v(29.25, -15.1) * mm, v(30.3, -14.6) * mm, v(32.24, -14.58) * mm, v(32.75, -15.1) * mm]});
            skFitSpline(sketch, "E1408", {"points": [v(101.25, -15.1) * mm, v(101.76, -15.6) * mm, v(101.94, -19.21) * mm, v(101.25, -21.1) * mm]});
            skFitSpline(sketch, "E1409", {"points": [v(101.25, -21.1) * mm, v(100.68, -22.64) * mm, v(99.3, -24.05) * mm, v(97.75, -24.6) * mm]});
            skFitSpline(sketch, "E1410", {"points": [v(97.75, -24.6) * mm, v(95.7, -25.3) * mm, v(91.76, -25.1) * mm, v(91.25, -24.6) * mm]});
            skFitSpline(sketch, "E1411", {"points": [v(91.25, -24.6) * mm, v(90.74, -24.08) * mm, v(90.66, -22.4) * mm, v(91.25, -21.6) * mm]});
            skFitSpline(sketch, "E1412", {"points": [v(91.25, -21.6) * mm, v(93.14, -19.03) * mm, v(95.58, -16.83) * mm, v(98.25, -15.1) * mm]});
            skFitSpline(sketch, "E1413", {"points": [v(98.25, -15.1) * mm, v(99.09, -14.55) * mm, v(100.74, -14.58) * mm, v(101.25, -15.1) * mm]});
            skFitSpline(sketch, "E1414", {"points": [v(-29.25, -15.1) * mm, v(-27.99, -15.72) * mm, v(-26.68, -16.74) * mm, v(-26.25, -18.1) * mm]});
            skFitSpline(sketch, "E1415", {"points": [v(-26.25, -18.1) * mm, v(-25.6, -20.16) * mm, v(-25.74, -24.08) * mm, v(-26.25, -24.6) * mm]});
            skFitSpline(sketch, "E1416", {"points": [v(-26.25, -24.6) * mm, v(-26.76, -25.1) * mm, v(-32.28, -25.12) * mm, v(-32.78, -24.6) * mm]});
            skFitSpline(sketch, "E1417", {"points": [v(-32.78, -24.6) * mm, v(-33.28, -24.06) * mm, v(-32.96, -15.77) * mm, v(-32.25, -15.1) * mm]});
            skFitSpline(sketch, "E1418", {"points": [v(-32.25, -15.1) * mm, v(-31.54, -14.42) * mm, v(-30.14, -14.64) * mm, v(-29.25, -15.1) * mm]});
            skFitSpline(sketch, "E1419", {"points": [v(-29.25, -28.1) * mm, v(-27.99, -28.72) * mm, v(-26.58, -29.72) * mm, v(-26.25, -31.1) * mm]});
            skFitSpline(sketch, "E1420", {"points": [v(-26.25, -31.1) * mm, v(-25.51, -34.17) * mm, v(-25.74, -40.08) * mm, v(-26.25, -40.6) * mm]});
            skFitSpline(sketch, "E1421", {"points": [v(-26.25, -40.6) * mm, v(-26.76, -41.1) * mm, v(-28.7, -41.08) * mm, v(-29.75, -40.6) * mm]});
            skFitSpline(sketch, "E1422", {"points": [v(-29.75, -40.6) * mm, v(-31.03, -40) * mm, v(-32.47, -38.98) * mm, v(-32.75, -37.6) * mm]});
            skFitSpline(sketch, "E1423", {"points": [v(-32.75, -37.6) * mm, v(-33.37, -34.48) * mm, v(-32.95, -28.76) * mm, v(-32.25, -28.1) * mm]});
            skFitSpline(sketch, "E1424", {"points": [v(-32.25, -28.1) * mm, v(-31.55, -27.42) * mm, v(-30.14, -27.64) * mm, v(-29.25, -28.1) * mm]});
            skFitSpline(sketch, "E1425", {"points": [v(29.25, -28.1) * mm, v(27.96, -28.68) * mm, v(26.58, -29.72) * mm, v(26.25, -31.1) * mm]});
            skFitSpline(sketch, "E1426", {"points": [v(26.25, -31.1) * mm, v(25.51, -34.17) * mm, v(25.74, -40.08) * mm, v(26.25, -40.6) * mm]});
            skFitSpline(sketch, "E1427", {"points": [v(26.25, -40.6) * mm, v(26.76, -41.1) * mm, v(28.67, -41.04) * mm, v(29.75, -40.6) * mm]});
            skFitSpline(sketch, "E1428", {"points": [v(29.75, -40.6) * mm, v(30.84, -40.14) * mm, v(31.97, -39.24) * mm, v(32.25, -38.1) * mm]});
            skFitSpline(sketch, "E1429", {"points": [v(32.25, -38.1) * mm, v(33.04, -34.85) * mm, v(33.28, -28.62) * mm, v(32.78, -28.1) * mm]});
            skFitSpline(sketch, "E1430", {"points": [v(32.78, -28.1) * mm, v(32.28, -27.56) * mm, v(30.32, -27.6) * mm, v(29.25, -28.1) * mm]});
            skFitSpline(sketch, "E1431", {"points": [v(-9.75, -34.6) * mm, v(-10.26, -35.1) * mm, v(-10.26, -40.08) * mm, v(-9.75, -40.6) * mm]});
            skFitSpline(sketch, "E1432", {"points": [v(-9.75, -40.6) * mm, v(-9.24, -41.1) * mm, v(-3.76, -41.1) * mm, v(-3.25, -40.6) * mm]});
            skFitSpline(sketch, "E1433", {"points": [v(-3.25, -40.6) * mm, v(-2.74, -40.08) * mm, v(-2.74, -35.1) * mm, v(-3.25, -34.6) * mm]});
            skFitSpline(sketch, "E1434", {"points": [v(-3.25, -34.6) * mm, v(-3.76, -34.08) * mm, v(-9.24, -34.08) * mm, v(-9.75, -34.6) * mm]});
            skFitSpline(sketch, "E1435", {"points": [v(3.25, -34.6) * mm, v(2.74, -35.1) * mm, v(2.74, -40.08) * mm, v(3.25, -40.6) * mm]});
            skFitSpline(sketch, "E1436", {"points": [v(3.25, -40.6) * mm, v(3.76, -41.1) * mm, v(9.24, -41.1) * mm, v(9.75, -40.6) * mm]});
            skFitSpline(sketch, "E1437", {"points": [v(9.75, -40.6) * mm, v(10.26, -40.08) * mm, v(10.26, -35.1) * mm, v(9.75, -34.6) * mm]});
            skFitSpline(sketch, "E1438", {"points": [v(9.75, -34.6) * mm, v(9.24, -34.08) * mm, v(3.76, -34.08) * mm, v(3.25, -34.6) * mm]});
            skFitSpline(sketch, "E1439", {"points": [v(-81.75, -54.1) * mm, v(-81.24, -54.6) * mm, v(-81.24, -66.58) * mm, v(-81.75, -67.1) * mm]});
            skFitSpline(sketch, "E1440", {"points": [v(-81.75, -67.1) * mm, v(-82.26, -67.6) * mm, v(-83.87, -67.56) * mm, v(-84.75, -67.1) * mm]});
            skFitSpline(sketch, "E1441", {"points": [v(-84.75, -67.1) * mm, v(-86.2, -66.3) * mm, v(-87.7, -65.15) * mm, v(-88.25, -63.6) * mm]});
            skFitSpline(sketch, "E1442", {"points": [v(-88.25, -63.6) * mm, v(-88.97, -61.55) * mm, v(-87.74, -57.6) * mm, v(-88.25, -57.1) * mm]});
            skFitSpline(sketch, "E1443", {"points": [v(-88.25, -57.1) * mm, v(-88.76, -56.58) * mm, v(-91.43, -56.52) * mm, v(-91.87, -57.1) * mm]});
            skFitSpline(sketch, "E1444", {"points": [v(-91.87, -57.1) * mm, v(-92.32, -57.66) * mm, v(-90.68, -59.52) * mm, v(-91.12, -60.1) * mm]});
            skFitSpline(sketch, "E1445", {"points": [v(-91.12, -60.1) * mm, v(-91.57, -60.66) * mm, v(-93.8, -60.85) * mm, v(-94.75, -60.1) * mm]});
            skFitSpline(sketch, "E1446", {"points": [v(-94.75, -60.1) * mm, v(-96.6, -58.6) * mm, v(-98.92, -54.73) * mm, v(-98.57, -54.1) * mm]});
            skFitSpline(sketch, "E1447", {"points": [v(-98.57, -54.1) * mm, v(-98.22, -53.45) * mm, v(-82.26, -53.58) * mm, v(-81.75, -54.1) * mm]});
            skFitSpline(sketch, "E1448", {"points": [v(-68.75, -54.1) * mm, v(-69.26, -54.6) * mm, v(-69.26, -59.58) * mm, v(-68.75, -60.1) * mm]});
            skFitSpline(sketch, "E1449", {"points": [v(-68.75, -60.1) * mm, v(-68.24, -60.6) * mm, v(-64.38, -60.8) * mm, v(-62.37, -60.1) * mm]});
            skFitSpline(sketch, "E1450", {"points": [v(-62.37, -60.1) * mm, v(-61.57, -59.8) * mm, v(-61.38, -58.37) * mm, v(-61.75, -57.6) * mm]});
            skFitSpline(sketch, "E1451", {"points": [v(-61.75, -57.6) * mm, v(-62.46, -56.1) * mm, v(-63.77, -54.83) * mm, v(-65.25, -54.1) * mm]});
            skFitSpline(sketch, "E1452", {"points": [v(-65.25, -54.1) * mm, v(-66.3, -53.57) * mm, v(-68.24, -53.58) * mm, v(-68.75, -54.1) * mm]});
            skFitSpline(sketch, "E1453", {"points": [v(68.75, -54.1) * mm, v(69.26, -54.6) * mm, v(69.26, -59.58) * mm, v(68.75, -60.1) * mm]});
            skFitSpline(sketch, "E1454", {"points": [v(68.75, -60.1) * mm, v(68.24, -60.6) * mm, v(64.38, -60.8) * mm, v(62.37, -60.1) * mm]});
            skFitSpline(sketch, "E1455", {"points": [v(62.37, -60.1) * mm, v(61.57, -59.8) * mm, v(61.38, -58.37) * mm, v(61.75, -57.6) * mm]});
            skFitSpline(sketch, "E1456", {"points": [v(61.75, -57.6) * mm, v(62.46, -56.1) * mm, v(63.77, -54.83) * mm, v(65.25, -54.1) * mm]});
            skFitSpline(sketch, "E1457", {"points": [v(65.25, -54.1) * mm, v(66.3, -53.57) * mm, v(68.24, -53.58) * mm, v(68.75, -54.1) * mm]});
            skFitSpline(sketch, "E1458", {"points": [v(81.75, -54.1) * mm, v(81.24, -54.6) * mm, v(81.24, -66.58) * mm, v(81.75, -67.1) * mm]});
            skFitSpline(sketch, "E1459", {"points": [v(81.75, -67.1) * mm, v(82.26, -67.6) * mm, v(83.87, -67.56) * mm, v(84.75, -67.1) * mm]});
            skFitSpline(sketch, "E1460", {"points": [v(84.75, -67.1) * mm, v(86.2, -66.3) * mm, v(87.7, -65.15) * mm, v(88.25, -63.6) * mm]});
            skFitSpline(sketch, "E1461", {"points": [v(88.25, -63.6) * mm, v(88.97, -61.55) * mm, v(87.74, -57.6) * mm, v(88.25, -57.1) * mm]});
            skFitSpline(sketch, "E1462", {"points": [v(88.25, -57.1) * mm, v(88.76, -56.58) * mm, v(91.43, -56.52) * mm, v(91.87, -57.1) * mm]});
            skFitSpline(sketch, "E1463", {"points": [v(91.87, -57.1) * mm, v(92.32, -57.66) * mm, v(90.68, -59.52) * mm, v(91.12, -60.1) * mm]});
            skFitSpline(sketch, "E1464", {"points": [v(91.12, -60.1) * mm, v(91.57, -60.66) * mm, v(93.8, -60.85) * mm, v(94.75, -60.1) * mm]});
            skFitSpline(sketch, "E1465", {"points": [v(94.75, -60.1) * mm, v(96.6, -58.6) * mm, v(98.92, -54.73) * mm, v(98.57, -54.1) * mm]});
            skFitSpline(sketch, "E1466", {"points": [v(98.57, -54.1) * mm, v(98.22, -53.45) * mm, v(82.26, -53.58) * mm, v(81.75, -54.1) * mm]});
            skFitSpline(sketch, "E1467", {"points": [v(-78.25, -57.1) * mm, v(-78.76, -57.6) * mm, v(-78.76, -59.58) * mm, v(-78.25, -60.1) * mm]});
            skFitSpline(sketch, "E1468", {"points": [v(-78.25, -60.1) * mm, v(-77.74, -60.6) * mm, v(-72.26, -60.6) * mm, v(-71.75, -60.1) * mm]});
            skFitSpline(sketch, "E1469", {"points": [v(-71.75, -60.1) * mm, v(-71.24, -59.58) * mm, v(-71.24, -57.6) * mm, v(-71.75, -57.1) * mm]});
            skFitSpline(sketch, "E1470", {"points": [v(-71.75, -57.1) * mm, v(-72.26, -56.58) * mm, v(-77.74, -56.58) * mm, v(-78.25, -57.1) * mm]});
            skFitSpline(sketch, "E1471", {"points": [v(71.75, -57.1) * mm, v(71.24, -57.6) * mm, v(71.24, -59.58) * mm, v(71.75, -60.1) * mm]});
            skFitSpline(sketch, "E1472", {"points": [v(71.75, -60.1) * mm, v(72.26, -60.6) * mm, v(77.74, -60.6) * mm, v(78.25, -60.1) * mm]});
            skFitSpline(sketch, "E1473", {"points": [v(78.25, -60.1) * mm, v(78.76, -59.58) * mm, v(78.76, -57.6) * mm, v(78.25, -57.1) * mm]});
            skFitSpline(sketch, "E1474", {"points": [v(78.25, -57.1) * mm, v(77.74, -56.58) * mm, v(72.26, -56.58) * mm, v(71.75, -57.1) * mm]});
            skFitSpline(sketch, "E1475", {"points": [v(-78.25, -63.6) * mm, v(-78.76, -64.1) * mm, v(-78.76, -66.58) * mm, v(-78.25, -67.1) * mm]});
            skFitSpline(sketch, "E1476", {"points": [v(-78.25, -67.1) * mm, v(-77.74, -67.6) * mm, v(-75.8, -66.6) * mm, v(-74.75, -67.1) * mm]});
            skFitSpline(sketch, "E1477", {"points": [v(-74.75, -67.1) * mm, v(-73.47, -67.68) * mm, v(-73.1, -69.66) * mm, v(-71.75, -70.1) * mm]});
            skFitSpline(sketch, "E1478", {"points": [v(-71.75, -70.1) * mm, v(-69.68, -70.74) * mm, v(-65.76, -70.6) * mm, v(-65.25, -70.1) * mm]});
            skFitSpline(sketch, "E1479", {"points": [v(-65.25, -70.1) * mm, v(-64.74, -69.58) * mm, v(-64.78, -67.97) * mm, v(-65.25, -67.1) * mm]});
            skFitSpline(sketch, "E1480", {"points": [v(-65.25, -67.1) * mm, v(-66.03, -65.64) * mm, v(-67.16, -64.02) * mm, v(-68.75, -63.6) * mm]});
            skFitSpline(sketch, "E1481", {"points": [v(-68.75, -63.6) * mm, v(-71.8, -62.77) * mm, v(-77.74, -63.08) * mm, v(-78.25, -63.6) * mm]});
            skFitSpline(sketch, "E1482", {"points": [v(78.25, -63.6) * mm, v(78.76, -64.1) * mm, v(78.76, -66.58) * mm, v(78.25, -67.1) * mm]});
            skFitSpline(sketch, "E1483", {"points": [v(78.25, -67.1) * mm, v(77.74, -67.6) * mm, v(75.8, -66.6) * mm, v(74.75, -67.1) * mm]});
            skFitSpline(sketch, "E1484", {"points": [v(74.75, -67.1) * mm, v(73.47, -67.68) * mm, v(73.1, -69.66) * mm, v(71.75, -70.1) * mm]});
            skFitSpline(sketch, "E1485", {"points": [v(71.75, -70.1) * mm, v(69.68, -70.74) * mm, v(65.76, -70.6) * mm, v(65.25, -70.1) * mm]});
            skFitSpline(sketch, "E1486", {"points": [v(65.25, -70.1) * mm, v(64.74, -69.58) * mm, v(64.78, -67.97) * mm, v(65.25, -67.1) * mm]});
            skFitSpline(sketch, "E1487", {"points": [v(65.25, -67.1) * mm, v(66.03, -65.64) * mm, v(67.16, -64.02) * mm, v(68.75, -63.6) * mm]});
            skFitSpline(sketch, "E1488", {"points": [v(68.75, -63.6) * mm, v(71.8, -62.77) * mm, v(77.74, -63.08) * mm, v(78.25, -63.6) * mm]});
            skFitSpline(sketch, "E1489", {"points": [v(153.25, -73.6) * mm, v(153.45, -73.47) * mm, v(153.72, -73.32) * mm, v(153.75, -73.1) * mm]});
            skFitSpline(sketch, "E1490", {"points": [v(153.75, -73.1) * mm, v(153.9, -72.1) * mm, v(153.24, -70.6) * mm, v(153.75, -70.1) * mm]});
            skFitSpline(sketch, "E1491", {"points": [v(153.75, -70.1) * mm, v(154.26, -69.58) * mm, v(156.24, -69.58) * mm, v(156.75, -70.1) * mm]});
            skFitSpline(sketch, "E1492", {"points": [v(156.75, -70.1) * mm, v(157.26, -70.6) * mm, v(156.24, -73.08) * mm, v(156.75, -73.6) * mm]});
            skFitSpline(sketch, "E1493", {"points": [v(156.75, -73.6) * mm, v(157.26, -74.1) * mm, v(161.2, -74.3) * mm, v(163.25, -73.6) * mm]});
            skFitSpline(sketch, "E1494", {"points": [v(163.25, -73.6) * mm, v(164.8, -73.05) * mm, v(165.97, -71.54) * mm, v(166.75, -70.1) * mm]});
            skFitSpline(sketch, "E1495", {"points": [v(166.75, -70.1) * mm, v(167.22, -69.21) * mm, v(167.26, -67.6) * mm, v(166.75, -67.1) * mm]});
            skFitSpline(sketch, "E1496", {"points": [v(166.75, -67.1) * mm, v(166.24, -66.58) * mm, v(137.96, -65.22) * mm, v(123.75, -67.1) * mm]});
            skFitSpline(sketch, "E1497", {"points": [v(123.75, -67.1) * mm, v(120.71, -67.49) * mm, v(119.82, -71.92) * mm, v(117.25, -73.6) * mm]});
            skFitSpline(sketch, "E1498", {"points": [v(117.25, -73.6) * mm, v(116.27, -74.23) * mm, v(114.74, -72.97) * mm, v(113.75, -73.6) * mm]});
            skFitSpline(sketch, "E1499", {"points": [v(113.75, -73.6) * mm, v(111.36, -75.1) * mm, v(108.48, -79.6) * mm, v(107.75, -79.6) * mm]});
            skFitSpline(sketch, "E1500", {"points": [v(107.75, -79.6) * mm, v(107.02, -79.6) * mm, v(105.48, -76.6) * mm, v(104.75, -76.6) * mm]});
            skFitSpline(sketch, "E1501", {"points": [v(104.75, -76.6) * mm, v(104.02, -76.6) * mm, v(102.6, -78.47) * mm, v(101.75, -79.6) * mm]});
            skSolve(sketch);
        }
        {
            var Q0;
            Q0 = qSketchRegion(id + "F0", true);
            extrude(context, id + "F1", {"entities" : qUnion([Q0]), "depth" : 101.6 * mm, "offsetDistance" : 25.4 * mm});
        }
    });
